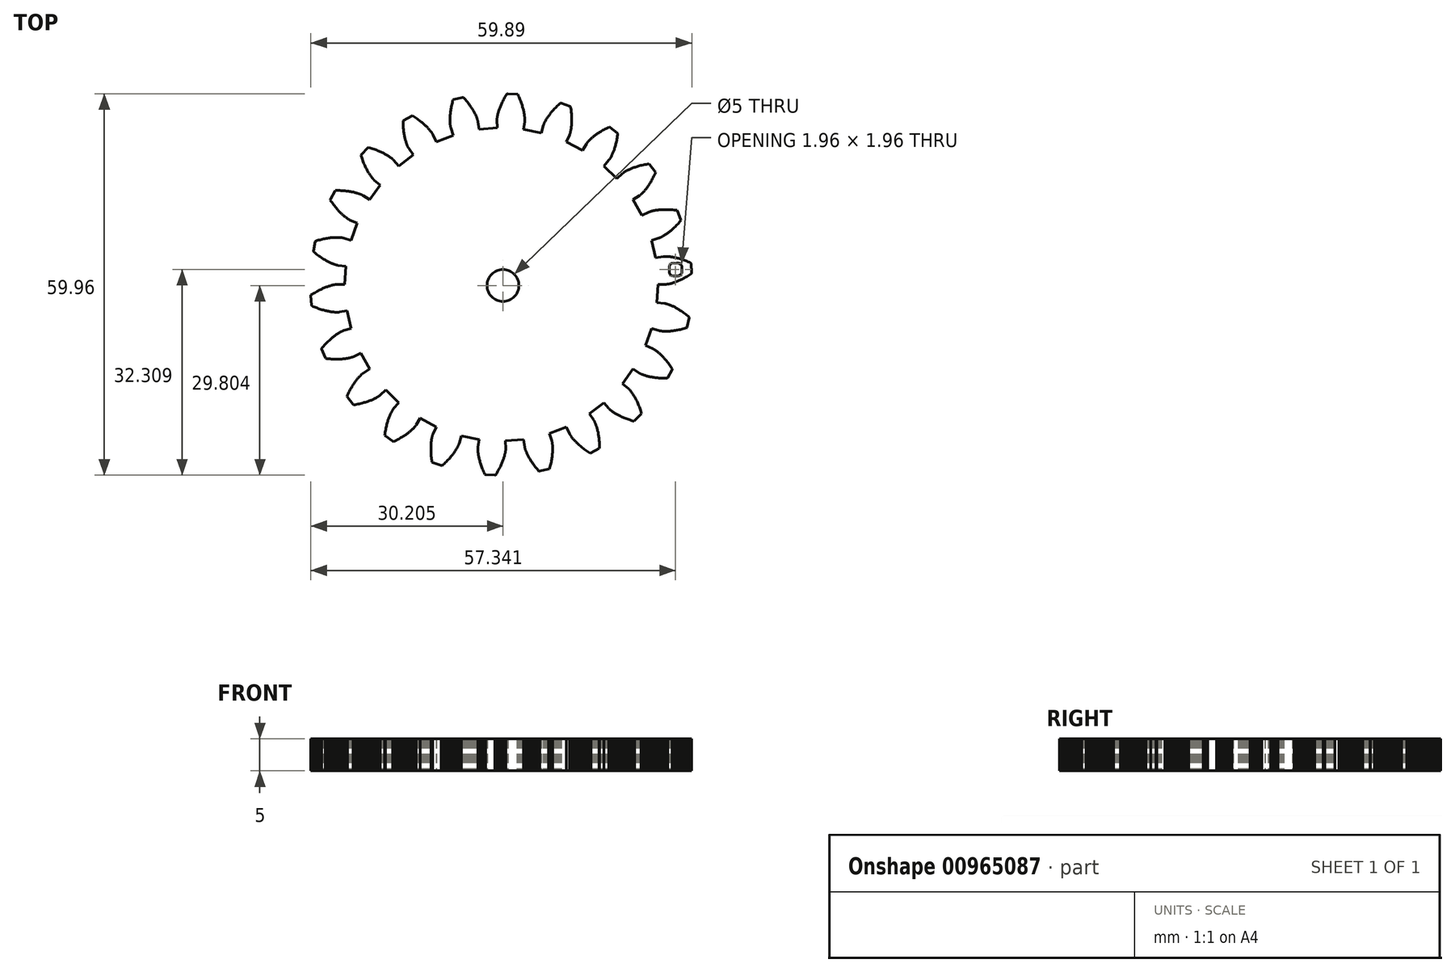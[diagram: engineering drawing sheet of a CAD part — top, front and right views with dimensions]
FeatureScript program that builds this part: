
annotation { "Feature Type Name" : "Feature", "Feature Type Description" : "" }
export const myFeature = defineFeature(function(context is Context, id is Id, definition is map)
    precondition{}
    {
        {
            var Q0;
            Q0=qCreatedBy(makeId("Top.planeOp"),FACE);
            var sketch = newSketch(context, id + "F0", { "sketchPlane" : qUnion([Q0])});
            skLineSegment(sketch, "E0", {"start": v(26.57, 2.43) * mm, "end": v(27.79, 2.43) * mm});
            skLineSegment(sketch, "E1", {"start": v(27.79, 2.43) * mm, "end": v(27.8, 2.43) * mm});
            skLineSegment(sketch, "E2", {"start": v(27.8, 2.43) * mm, "end": v(27.81, 2.43) * mm});
            skLineSegment(sketch, "E3", {"start": v(27.81, 2.43) * mm, "end": v(27.84, 2.43) * mm});
            skLineSegment(sketch, "E4", {"start": v(27.84, 2.43) * mm, "end": v(27.87, 2.43) * mm});
            skLineSegment(sketch, "E5", {"start": v(27.87, 2.43) * mm, "end": v(27.9, 2.44) * mm});
            skLineSegment(sketch, "E6", {"start": v(27.9, 2.44) * mm, "end": v(27.95, 2.44) * mm});
            skLineSegment(sketch, "E7", {"start": v(27.95, 2.44) * mm, "end": v(28, 2.45) * mm});
            skLineSegment(sketch, "E8", {"start": v(28, 2.45) * mm, "end": v(28.05, 2.46) * mm});
            skLineSegment(sketch, "E9", {"start": v(28.05, 2.46) * mm, "end": v(28.11, 2.47) * mm});
            skLineSegment(sketch, "E10", {"start": v(28.11, 2.47) * mm, "end": v(28.18, 2.48) * mm});
            skLineSegment(sketch, "E11", {"start": v(28.18, 2.48) * mm, "end": v(28.25, 2.5) * mm});
            skLineSegment(sketch, "E12", {"start": v(28.25, 2.5) * mm, "end": v(28.33, 2.5) * mm});
            skLineSegment(sketch, "E13", {"start": v(28.33, 2.5) * mm, "end": v(28.42, 2.53) * mm});
            skLineSegment(sketch, "E14", {"start": v(28.42, 2.53) * mm, "end": v(28.51, 2.55) * mm});
            skLineSegment(sketch, "E15", {"start": v(28.51, 2.55) * mm, "end": v(28.61, 2.57) * mm});
            skLineSegment(sketch, "E16", {"start": v(28.61, 2.57) * mm, "end": v(28.72, 2.6) * mm});
            skLineSegment(sketch, "E17", {"start": v(28.72, 2.6) * mm, "end": v(28.83, 2.63) * mm});
            skLineSegment(sketch, "E18", {"start": v(28.83, 2.63) * mm, "end": v(28.94, 2.67) * mm});
            skLineSegment(sketch, "E19", {"start": v(28.94, 2.67) * mm, "end": v(29.06, 2.7) * mm});
            skLineSegment(sketch, "E20", {"start": v(29.06, 2.7) * mm, "end": v(29.19, 2.75) * mm});
            skLineSegment(sketch, "E21", {"start": v(29.19, 2.75) * mm, "end": v(29.32, 2.8) * mm});
            skLineSegment(sketch, "E22", {"start": v(29.32, 2.8) * mm, "end": v(29.46, 2.85) * mm});
            skLineSegment(sketch, "E23", {"start": v(29.46, 2.85) * mm, "end": v(29.6, 2.9) * mm});
            skLineSegment(sketch, "E24", {"start": v(29.6, 2.9) * mm, "end": v(29.75, 2.97) * mm});
            skLineSegment(sketch, "E25", {"start": v(29.75, 2.97) * mm, "end": v(29.9, 3.03) * mm});
            skLineSegment(sketch, "E26", {"start": v(29.9, 3.03) * mm, "end": v(30.06, 3.1) * mm});
            skLineSegment(sketch, "E27", {"start": v(30.06, 3.1) * mm, "end": v(30.22, 3.18) * mm});
            skLineSegment(sketch, "E28", {"start": v(30.22, 3.18) * mm, "end": v(30.4, 3.26) * mm});
            skLineSegment(sketch, "E29", {"start": v(30.4, 3.26) * mm, "end": v(30.56, 3.35) * mm});
            skLineSegment(sketch, "E30", {"start": v(30.56, 3.35) * mm, "end": v(30.74, 3.44) * mm});
            skLineSegment(sketch, "E31", {"start": v(30.74, 3.44) * mm, "end": v(30.92, 3.54) * mm});
            skLineSegment(sketch, "E32", {"start": v(30.92, 3.54) * mm, "end": v(31.1, 3.64) * mm});
            skLineSegment(sketch, "E33", {"start": v(31.1, 3.64) * mm, "end": v(31.3, 3.76) * mm});
            skLineSegment(sketch, "E34", {"start": v(31.3, 3.76) * mm, "end": v(31.48, 3.87) * mm});
            skLineSegment(sketch, "E35", {"start": v(31.48, 3.87) * mm, "end": v(31.68, 4) * mm});
            skLineSegment(sketch, "E36", {"start": v(31.68, 4) * mm, "end": v(31.88, 4.13) * mm});
            skLineSegment(sketch, "E37", {"start": v(31.88, 4.13) * mm, "end": v(31.89, 4.25) * mm});
            skLineSegment(sketch, "E38", {"start": v(31.89, 4.25) * mm, "end": v(31.76, 5.69) * mm});
            skLineSegment(sketch, "E39", {"start": v(31.76, 5.69) * mm, "end": v(31.74, 5.81) * mm});
            skLineSegment(sketch, "E40", {"start": v(31.74, 5.81) * mm, "end": v(31.52, 5.9) * mm});
            skLineSegment(sketch, "E41", {"start": v(31.52, 5.9) * mm, "end": v(31.3, 6) * mm});
            skLineSegment(sketch, "E42", {"start": v(31.3, 6) * mm, "end": v(31.1, 6.08) * mm});
            skLineSegment(sketch, "E43", {"start": v(31.1, 6.08) * mm, "end": v(30.9, 6.16) * mm});
            skLineSegment(sketch, "E44", {"start": v(30.9, 6.16) * mm, "end": v(30.7, 6.23) * mm});
            skLineSegment(sketch, "E45", {"start": v(30.7, 6.23) * mm, "end": v(30.5, 6.3) * mm});
            skLineSegment(sketch, "E46", {"start": v(30.5, 6.3) * mm, "end": v(30.3, 6.36) * mm});
            skLineSegment(sketch, "E47", {"start": v(30.3, 6.36) * mm, "end": v(30.12, 6.41) * mm});
            skLineSegment(sketch, "E48", {"start": v(30.12, 6.41) * mm, "end": v(29.94, 6.47) * mm});
            skLineSegment(sketch, "E49", {"start": v(29.94, 6.47) * mm, "end": v(29.77, 6.51) * mm});
            skLineSegment(sketch, "E50", {"start": v(29.77, 6.51) * mm, "end": v(29.6, 6.56) * mm});
            skLineSegment(sketch, "E51", {"start": v(29.6, 6.56) * mm, "end": v(29.44, 6.6) * mm});
            skLineSegment(sketch, "E52", {"start": v(29.44, 6.6) * mm, "end": v(29.29, 6.63) * mm});
            skLineSegment(sketch, "E53", {"start": v(29.29, 6.63) * mm, "end": v(29.14, 6.66) * mm});
            skLineSegment(sketch, "E54", {"start": v(29.14, 6.66) * mm, "end": v(29, 6.7) * mm});
            skLineSegment(sketch, "E55", {"start": v(29, 6.7) * mm, "end": v(28.85, 6.71) * mm});
            skLineSegment(sketch, "E56", {"start": v(28.85, 6.71) * mm, "end": v(28.72, 6.74) * mm});
            skLineSegment(sketch, "E57", {"start": v(28.72, 6.74) * mm, "end": v(28.6, 6.75) * mm});
            skLineSegment(sketch, "E58", {"start": v(28.6, 6.75) * mm, "end": v(28.47, 6.77) * mm});
            skLineSegment(sketch, "E59", {"start": v(28.47, 6.77) * mm, "end": v(28.36, 6.78) * mm});
            skLineSegment(sketch, "E60", {"start": v(28.36, 6.78) * mm, "end": v(28.25, 6.8) * mm});
            skLineSegment(sketch, "E61", {"start": v(28.25, 6.8) * mm, "end": v(28.15, 6.8) * mm});
            skLineSegment(sketch, "E62", {"start": v(28.15, 6.8) * mm, "end": v(28.06, 6.8) * mm});
            skLineSegment(sketch, "E63", {"start": v(28.06, 6.8) * mm, "end": v(27.97, 6.8) * mm});
            skLineSegment(sketch, "E64", {"start": v(27.97, 6.8) * mm, "end": v(27.89, 6.81) * mm});
            skLineSegment(sketch, "E65", {"start": v(27.89, 6.81) * mm, "end": v(27.81, 6.81) * mm});
            skLineSegment(sketch, "E66", {"start": v(27.81, 6.81) * mm, "end": v(27.74, 6.81) * mm});
            skLineSegment(sketch, "E67", {"start": v(27.74, 6.81) * mm, "end": v(27.68, 6.81) * mm});
            skLineSegment(sketch, "E68", {"start": v(27.68, 6.81) * mm, "end": v(27.62, 6.8) * mm});
            skLineSegment(sketch, "E69", {"start": v(27.62, 6.8) * mm, "end": v(27.57, 6.8) * mm});
            skLineSegment(sketch, "E70", {"start": v(27.57, 6.8) * mm, "end": v(27.53, 6.8) * mm});
            skLineSegment(sketch, "E71", {"start": v(27.53, 6.8) * mm, "end": v(27.5, 6.8) * mm});
            skLineSegment(sketch, "E72", {"start": v(27.5, 6.8) * mm, "end": v(27.47, 6.8) * mm});
            skLineSegment(sketch, "E73", {"start": v(27.47, 6.8) * mm, "end": v(27.44, 6.8) * mm});
            skLineSegment(sketch, "E74", {"start": v(27.44, 6.8) * mm, "end": v(27.43, 6.8) * mm});
            skLineSegment(sketch, "E75", {"start": v(27.43, 6.8) * mm, "end": v(27.42, 6.8) * mm});
            skLineSegment(sketch, "E76", {"start": v(27.42, 6.8) * mm, "end": v(26.21, 6.59) * mm});
            skLineSegment(sketch, "E77", {"start": v(26.21, 6.59) * mm, "end": v(25.57, 9.37) * mm});
            skLineSegment(sketch, "E78", {"start": v(25.57, 9.37) * mm, "end": v(26.74, 9.71) * mm});
            skLineSegment(sketch, "E79", {"start": v(26.74, 9.71) * mm, "end": v(26.75, 9.72) * mm});
            skLineSegment(sketch, "E80", {"start": v(26.75, 9.72) * mm, "end": v(26.76, 9.72) * mm});
            skLineSegment(sketch, "E81", {"start": v(26.76, 9.72) * mm, "end": v(26.79, 9.73) * mm});
            skLineSegment(sketch, "E82", {"start": v(26.79, 9.73) * mm, "end": v(26.81, 9.74) * mm});
            skLineSegment(sketch, "E83", {"start": v(26.81, 9.74) * mm, "end": v(26.85, 9.75) * mm});
            skLineSegment(sketch, "E84", {"start": v(26.85, 9.75) * mm, "end": v(26.89, 9.77) * mm});
            skLineSegment(sketch, "E85", {"start": v(26.89, 9.77) * mm, "end": v(26.93, 9.79) * mm});
            skLineSegment(sketch, "E86", {"start": v(26.93, 9.79) * mm, "end": v(26.99, 9.81) * mm});
            skLineSegment(sketch, "E87", {"start": v(26.99, 9.81) * mm, "end": v(27.04, 9.84) * mm});
            skLineSegment(sketch, "E88", {"start": v(27.04, 9.84) * mm, "end": v(27.1, 9.87) * mm});
            skLineSegment(sketch, "E89", {"start": v(27.1, 9.87) * mm, "end": v(27.17, 9.9) * mm});
            skLineSegment(sketch, "E90", {"start": v(27.17, 9.9) * mm, "end": v(27.24, 9.94) * mm});
            skLineSegment(sketch, "E91", {"start": v(27.24, 9.94) * mm, "end": v(27.32, 9.98) * mm});
            skLineSegment(sketch, "E92", {"start": v(27.32, 9.98) * mm, "end": v(27.4, 10.03) * mm});
            skLineSegment(sketch, "E93", {"start": v(27.4, 10.03) * mm, "end": v(27.5, 10.08) * mm});
            skLineSegment(sketch, "E94", {"start": v(27.5, 10.08) * mm, "end": v(27.58, 10.14) * mm});
            skLineSegment(sketch, "E95", {"start": v(27.58, 10.14) * mm, "end": v(27.68, 10.2) * mm});
            skLineSegment(sketch, "E96", {"start": v(27.68, 10.2) * mm, "end": v(27.78, 10.27) * mm});
            skLineSegment(sketch, "E97", {"start": v(27.78, 10.27) * mm, "end": v(27.89, 10.34) * mm});
            skLineSegment(sketch, "E98", {"start": v(27.89, 10.34) * mm, "end": v(28, 10.41) * mm});
            skLineSegment(sketch, "E99", {"start": v(28, 10.41) * mm, "end": v(28.1, 10.5) * mm});
            skLineSegment(sketch, "E100", {"start": v(28.1, 10.5) * mm, "end": v(28.23, 10.58) * mm});
            skLineSegment(sketch, "E101", {"start": v(28.23, 10.58) * mm, "end": v(28.35, 10.68) * mm});
            skLineSegment(sketch, "E102", {"start": v(28.35, 10.68) * mm, "end": v(28.47, 10.78) * mm});
            skLineSegment(sketch, "E103", {"start": v(28.47, 10.78) * mm, "end": v(28.6, 10.89) * mm});
            skLineSegment(sketch, "E104", {"start": v(28.6, 10.89) * mm, "end": v(28.73, 11) * mm});
            skLineSegment(sketch, "E105", {"start": v(28.73, 11) * mm, "end": v(28.87, 11.12) * mm});
            skLineSegment(sketch, "E106", {"start": v(28.87, 11.12) * mm, "end": v(29, 11.24) * mm});
            skLineSegment(sketch, "E107", {"start": v(29, 11.24) * mm, "end": v(29.15, 11.37) * mm});
            skLineSegment(sketch, "E108", {"start": v(29.15, 11.37) * mm, "end": v(29.29, 11.51) * mm});
            skLineSegment(sketch, "E109", {"start": v(29.29, 11.51) * mm, "end": v(29.43, 11.66) * mm});
            skLineSegment(sketch, "E110", {"start": v(29.43, 11.66) * mm, "end": v(29.58, 11.81) * mm});
            skLineSegment(sketch, "E111", {"start": v(29.58, 11.81) * mm, "end": v(29.73, 11.97) * mm});
            skLineSegment(sketch, "E112", {"start": v(29.73, 11.97) * mm, "end": v(29.88, 12.14) * mm});
            skLineSegment(sketch, "E113", {"start": v(29.88, 12.14) * mm, "end": v(30.03, 12.31) * mm});
            skLineSegment(sketch, "E114", {"start": v(30.03, 12.31) * mm, "end": v(30.19, 12.5) * mm});
            skLineSegment(sketch, "E115", {"start": v(30.19, 12.5) * mm, "end": v(30.16, 12.62) * mm});
            skLineSegment(sketch, "E116", {"start": v(30.16, 12.62) * mm, "end": v(29.64, 13.96) * mm});
            skLineSegment(sketch, "E117", {"start": v(29.64, 13.96) * mm, "end": v(29.58, 14.07) * mm});
            skLineSegment(sketch, "E118", {"start": v(29.58, 14.07) * mm, "end": v(29.34, 14.1) * mm});
            skLineSegment(sketch, "E119", {"start": v(29.34, 14.1) * mm, "end": v(29.1, 14.12) * mm});
            skLineSegment(sketch, "E120", {"start": v(29.1, 14.12) * mm, "end": v(28.89, 14.14) * mm});
            skLineSegment(sketch, "E121", {"start": v(28.89, 14.14) * mm, "end": v(28.67, 14.16) * mm});
            skLineSegment(sketch, "E122", {"start": v(28.67, 14.16) * mm, "end": v(28.46, 14.17) * mm});
            skLineSegment(sketch, "E123", {"start": v(28.46, 14.17) * mm, "end": v(28.25, 14.18) * mm});
            skLineSegment(sketch, "E124", {"start": v(28.25, 14.18) * mm, "end": v(28.05, 14.2) * mm});
            skLineSegment(sketch, "E125", {"start": v(28.05, 14.2) * mm, "end": v(27.86, 14.2) * mm});
            skLineSegment(sketch, "E126", {"start": v(27.86, 14.2) * mm, "end": v(27.67, 14.2) * mm});
            skLineSegment(sketch, "E127", {"start": v(27.67, 14.2) * mm, "end": v(27.5, 14.19) * mm});
            skLineSegment(sketch, "E128", {"start": v(27.5, 14.19) * mm, "end": v(27.32, 14.18) * mm});
            skLineSegment(sketch, "E129", {"start": v(27.32, 14.18) * mm, "end": v(27.15, 14.18) * mm});
            skLineSegment(sketch, "E130", {"start": v(27.15, 14.18) * mm, "end": v(27, 14.17) * mm});
            skLineSegment(sketch, "E131", {"start": v(27, 14.17) * mm, "end": v(26.84, 14.15) * mm});
            skLineSegment(sketch, "E132", {"start": v(26.84, 14.15) * mm, "end": v(26.7, 14.14) * mm});
            skLineSegment(sketch, "E133", {"start": v(26.7, 14.14) * mm, "end": v(26.56, 14.12) * mm});
            skLineSegment(sketch, "E134", {"start": v(26.56, 14.12) * mm, "end": v(26.42, 14.1) * mm});
            skLineSegment(sketch, "E135", {"start": v(26.42, 14.1) * mm, "end": v(26.3, 14.09) * mm});
            skLineSegment(sketch, "E136", {"start": v(26.3, 14.09) * mm, "end": v(26.18, 14.07) * mm});
            skLineSegment(sketch, "E137", {"start": v(26.18, 14.07) * mm, "end": v(26.06, 14.05) * mm});
            skLineSegment(sketch, "E138", {"start": v(26.06, 14.05) * mm, "end": v(25.96, 14.03) * mm});
            skLineSegment(sketch, "E139", {"start": v(25.96, 14.03) * mm, "end": v(25.86, 14) * mm});
            skLineSegment(sketch, "E140", {"start": v(25.86, 14) * mm, "end": v(25.77, 13.99) * mm});
            skLineSegment(sketch, "E141", {"start": v(25.77, 13.99) * mm, "end": v(25.68, 13.96) * mm});
            skLineSegment(sketch, "E142", {"start": v(25.68, 13.96) * mm, "end": v(25.6, 13.94) * mm});
            skLineSegment(sketch, "E143", {"start": v(25.6, 13.94) * mm, "end": v(25.53, 13.92) * mm});
            skLineSegment(sketch, "E144", {"start": v(25.53, 13.92) * mm, "end": v(25.46, 13.9) * mm});
            skLineSegment(sketch, "E145", {"start": v(25.46, 13.9) * mm, "end": v(25.4, 13.89) * mm});
            skLineSegment(sketch, "E146", {"start": v(25.4, 13.89) * mm, "end": v(25.35, 13.87) * mm});
            skLineSegment(sketch, "E147", {"start": v(25.35, 13.87) * mm, "end": v(25.3, 13.85) * mm});
            skLineSegment(sketch, "E148", {"start": v(25.3, 13.85) * mm, "end": v(25.26, 13.84) * mm});
            skLineSegment(sketch, "E149", {"start": v(25.26, 13.84) * mm, "end": v(25.23, 13.82) * mm});
            skLineSegment(sketch, "E150", {"start": v(25.23, 13.82) * mm, "end": v(25.2, 13.81) * mm});
            skLineSegment(sketch, "E151", {"start": v(25.2, 13.81) * mm, "end": v(25.18, 13.8) * mm});
            skLineSegment(sketch, "E152", {"start": v(25.18, 13.8) * mm, "end": v(25.16, 13.8) * mm});
            skLineSegment(sketch, "E153", {"start": v(25.16, 13.8) * mm, "end": v(25.15, 13.8) * mm});
            skLineSegment(sketch, "E154", {"start": v(25.15, 13.8) * mm, "end": v(24.06, 13.26) * mm});
            skLineSegment(sketch, "E155", {"start": v(24.06, 13.26) * mm, "end": v(22.66, 15.74) * mm});
            skLineSegment(sketch, "E156", {"start": v(22.66, 15.74) * mm, "end": v(23.68, 16.4) * mm});
            skLineSegment(sketch, "E157", {"start": v(23.68, 16.4) * mm, "end": v(23.7, 16.4) * mm});
            skLineSegment(sketch, "E158", {"start": v(23.7, 16.4) * mm, "end": v(23.7, 16.42) * mm});
            skLineSegment(sketch, "E159", {"start": v(23.7, 16.42) * mm, "end": v(23.72, 16.43) * mm});
            skLineSegment(sketch, "E160", {"start": v(23.72, 16.43) * mm, "end": v(23.75, 16.45) * mm});
            skLineSegment(sketch, "E161", {"start": v(23.75, 16.45) * mm, "end": v(23.78, 16.47) * mm});
            skLineSegment(sketch, "E162", {"start": v(23.78, 16.47) * mm, "end": v(23.81, 16.5) * mm});
            skLineSegment(sketch, "E163", {"start": v(23.81, 16.5) * mm, "end": v(23.85, 16.53) * mm});
            skLineSegment(sketch, "E164", {"start": v(23.85, 16.53) * mm, "end": v(23.9, 16.57) * mm});
            skLineSegment(sketch, "E165", {"start": v(23.9, 16.57) * mm, "end": v(23.94, 16.6) * mm});
            skLineSegment(sketch, "E166", {"start": v(23.94, 16.6) * mm, "end": v(23.99, 16.66) * mm});
            skLineSegment(sketch, "E167", {"start": v(23.99, 16.66) * mm, "end": v(24.04, 16.7) * mm});
            skLineSegment(sketch, "E168", {"start": v(24.04, 16.7) * mm, "end": v(24.1, 16.76) * mm});
            skLineSegment(sketch, "E169", {"start": v(24.1, 16.76) * mm, "end": v(24.16, 16.83) * mm});
            skLineSegment(sketch, "E170", {"start": v(24.16, 16.83) * mm, "end": v(24.23, 16.9) * mm});
            skLineSegment(sketch, "E171", {"start": v(24.23, 16.9) * mm, "end": v(24.3, 16.97) * mm});
            skLineSegment(sketch, "E172", {"start": v(24.3, 16.97) * mm, "end": v(24.37, 17.05) * mm});
            skLineSegment(sketch, "E173", {"start": v(24.37, 17.05) * mm, "end": v(24.45, 17.14) * mm});
            skLineSegment(sketch, "E174", {"start": v(24.45, 17.14) * mm, "end": v(24.53, 17.23) * mm});
            skLineSegment(sketch, "E175", {"start": v(24.53, 17.23) * mm, "end": v(24.6, 17.33) * mm});
            skLineSegment(sketch, "E176", {"start": v(24.6, 17.33) * mm, "end": v(24.7, 17.43) * mm});
            skLineSegment(sketch, "E177", {"start": v(24.7, 17.43) * mm, "end": v(24.78, 17.54) * mm});
            skLineSegment(sketch, "E178", {"start": v(24.78, 17.54) * mm, "end": v(24.86, 17.66) * mm});
            skLineSegment(sketch, "E179", {"start": v(24.86, 17.66) * mm, "end": v(24.95, 17.78) * mm});
            skLineSegment(sketch, "E180", {"start": v(24.95, 17.78) * mm, "end": v(25.05, 17.92) * mm});
            skLineSegment(sketch, "E181", {"start": v(25.05, 17.92) * mm, "end": v(25.14, 18.05) * mm});
            skLineSegment(sketch, "E182", {"start": v(25.14, 18.05) * mm, "end": v(25.23, 18.2) * mm});
            skLineSegment(sketch, "E183", {"start": v(25.23, 18.2) * mm, "end": v(25.33, 18.35) * mm});
            skLineSegment(sketch, "E184", {"start": v(25.33, 18.35) * mm, "end": v(25.43, 18.51) * mm});
            skLineSegment(sketch, "E185", {"start": v(25.43, 18.51) * mm, "end": v(25.52, 18.68) * mm});
            skLineSegment(sketch, "E186", {"start": v(25.52, 18.68) * mm, "end": v(25.62, 18.85) * mm});
            skLineSegment(sketch, "E187", {"start": v(25.62, 18.85) * mm, "end": v(25.72, 19.03) * mm});
            skLineSegment(sketch, "E188", {"start": v(25.72, 19.03) * mm, "end": v(25.82, 19.22) * mm});
            skLineSegment(sketch, "E189", {"start": v(25.82, 19.22) * mm, "end": v(25.92, 19.41) * mm});
            skLineSegment(sketch, "E190", {"start": v(25.92, 19.41) * mm, "end": v(26.01, 19.62) * mm});
            skLineSegment(sketch, "E191", {"start": v(26.01, 19.62) * mm, "end": v(26.11, 19.83) * mm});
            skLineSegment(sketch, "E192", {"start": v(26.11, 19.83) * mm, "end": v(26.2, 20.04) * mm});
            skLineSegment(sketch, "E193", {"start": v(26.2, 20.04) * mm, "end": v(26.15, 20.15) * mm});
            skLineSegment(sketch, "E194", {"start": v(26.15, 20.15) * mm, "end": v(25.27, 21.3) * mm});
            skLineSegment(sketch, "E195", {"start": v(25.27, 21.3) * mm, "end": v(25.18, 21.38) * mm});
            skLineSegment(sketch, "E196", {"start": v(25.18, 21.38) * mm, "end": v(24.94, 21.34) * mm});
            skLineSegment(sketch, "E197", {"start": v(24.94, 21.34) * mm, "end": v(24.71, 21.3) * mm});
            skLineSegment(sketch, "E198", {"start": v(24.71, 21.3) * mm, "end": v(24.5, 21.26) * mm});
            skLineSegment(sketch, "E199", {"start": v(24.5, 21.26) * mm, "end": v(24.28, 21.22) * mm});
            skLineSegment(sketch, "E200", {"start": v(24.28, 21.22) * mm, "end": v(24.07, 21.17) * mm});
            skLineSegment(sketch, "E201", {"start": v(24.07, 21.17) * mm, "end": v(23.87, 21.12) * mm});
            skLineSegment(sketch, "E202", {"start": v(23.87, 21.12) * mm, "end": v(23.68, 21.07) * mm});
            skLineSegment(sketch, "E203", {"start": v(23.68, 21.07) * mm, "end": v(23.5, 21.02) * mm});
            skLineSegment(sketch, "E204", {"start": v(23.5, 21.02) * mm, "end": v(23.32, 20.97) * mm});
            skLineSegment(sketch, "E205", {"start": v(23.32, 20.97) * mm, "end": v(23.15, 20.91) * mm});
            skLineSegment(sketch, "E206", {"start": v(23.15, 20.91) * mm, "end": v(22.98, 20.86) * mm});
            skLineSegment(sketch, "E207", {"start": v(22.98, 20.86) * mm, "end": v(22.82, 20.8) * mm});
            skLineSegment(sketch, "E208", {"start": v(22.82, 20.8) * mm, "end": v(22.67, 20.75) * mm});
            skLineSegment(sketch, "E209", {"start": v(22.67, 20.75) * mm, "end": v(22.53, 20.7) * mm});
            skLineSegment(sketch, "E210", {"start": v(22.53, 20.7) * mm, "end": v(22.4, 20.64) * mm});
            skLineSegment(sketch, "E211", {"start": v(22.4, 20.64) * mm, "end": v(22.26, 20.58) * mm});
            skLineSegment(sketch, "E212", {"start": v(22.26, 20.58) * mm, "end": v(22.14, 20.53) * mm});
            skLineSegment(sketch, "E213", {"start": v(22.14, 20.53) * mm, "end": v(22.03, 20.48) * mm});
            skLineSegment(sketch, "E214", {"start": v(22.03, 20.48) * mm, "end": v(21.92, 20.43) * mm});
            skLineSegment(sketch, "E215", {"start": v(21.92, 20.43) * mm, "end": v(21.81, 20.37) * mm});
            skLineSegment(sketch, "E216", {"start": v(21.81, 20.37) * mm, "end": v(21.72, 20.32) * mm});
            skLineSegment(sketch, "E217", {"start": v(21.72, 20.32) * mm, "end": v(21.63, 20.28) * mm});
            skLineSegment(sketch, "E218", {"start": v(21.63, 20.28) * mm, "end": v(21.55, 20.23) * mm});
            skLineSegment(sketch, "E219", {"start": v(21.55, 20.23) * mm, "end": v(21.47, 20.19) * mm});
            skLineSegment(sketch, "E220", {"start": v(21.47, 20.19) * mm, "end": v(21.4, 20.14) * mm});
            skLineSegment(sketch, "E221", {"start": v(21.4, 20.14) * mm, "end": v(21.33, 20.1) * mm});
            skLineSegment(sketch, "E222", {"start": v(21.33, 20.1) * mm, "end": v(21.28, 20.07) * mm});
            skLineSegment(sketch, "E223", {"start": v(21.28, 20.07) * mm, "end": v(21.22, 20.03) * mm});
            skLineSegment(sketch, "E224", {"start": v(21.22, 20.03) * mm, "end": v(21.18, 20) * mm});
            skLineSegment(sketch, "E225", {"start": v(21.18, 20) * mm, "end": v(21.14, 19.97) * mm});
            skLineSegment(sketch, "E226", {"start": v(21.14, 19.97) * mm, "end": v(21.1, 19.95) * mm});
            skLineSegment(sketch, "E227", {"start": v(21.1, 19.95) * mm, "end": v(21.08, 19.92) * mm});
            skLineSegment(sketch, "E228", {"start": v(21.08, 19.92) * mm, "end": v(21.05, 19.9) * mm});
            skLineSegment(sketch, "E229", {"start": v(21.05, 19.9) * mm, "end": v(21.03, 19.9) * mm});
            skLineSegment(sketch, "E230", {"start": v(21.03, 19.9) * mm, "end": v(21.02, 19.88) * mm});
            skLineSegment(sketch, "E231", {"start": v(21.02, 19.88) * mm, "end": v(21.01, 19.87) * mm});
            skLineSegment(sketch, "E232", {"start": v(21.01, 19.87) * mm, "end": v(20.11, 19.05) * mm});
            skLineSegment(sketch, "E233", {"start": v(20.11, 19.05) * mm, "end": v(18.07, 21.04) * mm});
            skLineSegment(sketch, "E234", {"start": v(18.07, 21.04) * mm, "end": v(18.87, 21.96) * mm});
            skLineSegment(sketch, "E235", {"start": v(18.87, 21.96) * mm, "end": v(18.87, 21.97) * mm});
            skLineSegment(sketch, "E236", {"start": v(18.87, 21.97) * mm, "end": v(18.88, 21.98) * mm});
            skLineSegment(sketch, "E237", {"start": v(18.88, 21.98) * mm, "end": v(18.9, 22) * mm});
            skLineSegment(sketch, "E238", {"start": v(18.9, 22) * mm, "end": v(18.91, 22.03) * mm});
            skLineSegment(sketch, "E239", {"start": v(18.91, 22.03) * mm, "end": v(18.94, 22.06) * mm});
            skLineSegment(sketch, "E240", {"start": v(18.94, 22.06) * mm, "end": v(18.96, 22.1) * mm});
            skLineSegment(sketch, "E241", {"start": v(18.96, 22.1) * mm, "end": v(18.99, 22.13) * mm});
            skLineSegment(sketch, "E242", {"start": v(18.99, 22.13) * mm, "end": v(19.02, 22.18) * mm});
            skLineSegment(sketch, "E243", {"start": v(19.02, 22.18) * mm, "end": v(19.05, 22.23) * mm});
            skLineSegment(sketch, "E244", {"start": v(19.05, 22.23) * mm, "end": v(19.09, 22.3) * mm});
            skLineSegment(sketch, "E245", {"start": v(19.09, 22.3) * mm, "end": v(19.13, 22.36) * mm});
            skLineSegment(sketch, "E246", {"start": v(19.13, 22.36) * mm, "end": v(19.17, 22.43) * mm});
            skLineSegment(sketch, "E247", {"start": v(19.17, 22.43) * mm, "end": v(19.2, 22.5) * mm});
            skLineSegment(sketch, "E248", {"start": v(19.2, 22.5) * mm, "end": v(19.25, 22.59) * mm});
            skLineSegment(sketch, "E249", {"start": v(19.25, 22.59) * mm, "end": v(19.3, 22.68) * mm});
            skLineSegment(sketch, "E250", {"start": v(19.3, 22.68) * mm, "end": v(19.35, 22.78) * mm});
            skLineSegment(sketch, "E251", {"start": v(19.35, 22.78) * mm, "end": v(19.4, 22.88) * mm});
            skLineSegment(sketch, "E252", {"start": v(19.4, 22.88) * mm, "end": v(19.44, 23) * mm});
            skLineSegment(sketch, "E253", {"start": v(19.44, 23) * mm, "end": v(19.5, 23.1) * mm});
            skLineSegment(sketch, "E254", {"start": v(19.5, 23.1) * mm, "end": v(19.54, 23.23) * mm});
            skLineSegment(sketch, "E255", {"start": v(19.54, 23.23) * mm, "end": v(19.6, 23.36) * mm});
            skLineSegment(sketch, "E256", {"start": v(19.6, 23.36) * mm, "end": v(19.65, 23.5) * mm});
            skLineSegment(sketch, "E257", {"start": v(19.65, 23.5) * mm, "end": v(19.7, 23.65) * mm});
            skLineSegment(sketch, "E258", {"start": v(19.7, 23.65) * mm, "end": v(19.75, 23.8) * mm});
            skLineSegment(sketch, "E259", {"start": v(19.75, 23.8) * mm, "end": v(19.8, 23.96) * mm});
            skLineSegment(sketch, "E260", {"start": v(19.8, 23.96) * mm, "end": v(19.85, 24.12) * mm});
            skLineSegment(sketch, "E261", {"start": v(19.85, 24.12) * mm, "end": v(19.9, 24.3) * mm});
            skLineSegment(sketch, "E262", {"start": v(19.9, 24.3) * mm, "end": v(19.94, 24.48) * mm});
            skLineSegment(sketch, "E263", {"start": v(19.94, 24.48) * mm, "end": v(20, 24.66) * mm});
            skLineSegment(sketch, "E264", {"start": v(20, 24.66) * mm, "end": v(20.04, 24.86) * mm});
            skLineSegment(sketch, "E265", {"start": v(20.04, 24.86) * mm, "end": v(20.08, 25.06) * mm});
            skLineSegment(sketch, "E266", {"start": v(20.08, 25.06) * mm, "end": v(20.12, 25.27) * mm});
            skLineSegment(sketch, "E267", {"start": v(20.12, 25.27) * mm, "end": v(20.16, 25.48) * mm});
            skLineSegment(sketch, "E268", {"start": v(20.16, 25.48) * mm, "end": v(20.2, 25.7) * mm});
            skLineSegment(sketch, "E269", {"start": v(20.2, 25.7) * mm, "end": v(20.23, 25.93) * mm});
            skLineSegment(sketch, "E270", {"start": v(20.23, 25.93) * mm, "end": v(20.26, 26.17) * mm});
            skLineSegment(sketch, "E271", {"start": v(20.26, 26.17) * mm, "end": v(20.17, 26.25) * mm});
            skLineSegment(sketch, "E272", {"start": v(20.17, 26.25) * mm, "end": v(19, 27.1) * mm});
            skLineSegment(sketch, "E273", {"start": v(19, 27.1) * mm, "end": v(18.9, 27.16) * mm});
            skLineSegment(sketch, "E274", {"start": v(18.9, 27.16) * mm, "end": v(18.68, 27.06) * mm});
            skLineSegment(sketch, "E275", {"start": v(18.68, 27.06) * mm, "end": v(18.47, 26.96) * mm});
            skLineSegment(sketch, "E276", {"start": v(18.47, 26.96) * mm, "end": v(18.28, 26.85) * mm});
            skLineSegment(sketch, "E277", {"start": v(18.28, 26.85) * mm, "end": v(18.08, 26.75) * mm});
            skLineSegment(sketch, "E278", {"start": v(18.08, 26.75) * mm, "end": v(17.9, 26.65) * mm});
            skLineSegment(sketch, "E279", {"start": v(17.9, 26.65) * mm, "end": v(17.72, 26.54) * mm});
            skLineSegment(sketch, "E280", {"start": v(17.72, 26.54) * mm, "end": v(17.55, 26.44) * mm});
            skLineSegment(sketch, "E281", {"start": v(17.55, 26.44) * mm, "end": v(17.39, 26.34) * mm});
            skLineSegment(sketch, "E282", {"start": v(17.39, 26.34) * mm, "end": v(17.23, 26.24) * mm});
            skLineSegment(sketch, "E283", {"start": v(17.23, 26.24) * mm, "end": v(17.08, 26.14) * mm});
            skLineSegment(sketch, "E284", {"start": v(17.08, 26.14) * mm, "end": v(16.94, 26.04) * mm});
            skLineSegment(sketch, "E285", {"start": v(16.94, 26.04) * mm, "end": v(16.8, 25.94) * mm});
            skLineSegment(sketch, "E286", {"start": v(16.8, 25.94) * mm, "end": v(16.67, 25.85) * mm});
            skLineSegment(sketch, "E287", {"start": v(16.67, 25.85) * mm, "end": v(16.55, 25.75) * mm});
            skLineSegment(sketch, "E288", {"start": v(16.55, 25.75) * mm, "end": v(16.44, 25.66) * mm});
            skLineSegment(sketch, "E289", {"start": v(16.44, 25.66) * mm, "end": v(16.33, 25.57) * mm});
            skLineSegment(sketch, "E290", {"start": v(16.33, 25.57) * mm, "end": v(16.22, 25.49) * mm});
            skLineSegment(sketch, "E291", {"start": v(16.22, 25.49) * mm, "end": v(16.13, 25.4) * mm});
            skLineSegment(sketch, "E292", {"start": v(16.13, 25.4) * mm, "end": v(16.04, 25.32) * mm});
            skLineSegment(sketch, "E293", {"start": v(16.04, 25.32) * mm, "end": v(15.95, 25.25) * mm});
            skLineSegment(sketch, "E294", {"start": v(15.95, 25.25) * mm, "end": v(15.88, 25.17) * mm});
            skLineSegment(sketch, "E295", {"start": v(15.88, 25.17) * mm, "end": v(15.8, 25.1) * mm});
            skLineSegment(sketch, "E296", {"start": v(15.8, 25.1) * mm, "end": v(15.74, 25.03) * mm});
            skLineSegment(sketch, "E297", {"start": v(15.74, 25.03) * mm, "end": v(15.68, 24.97) * mm});
            skLineSegment(sketch, "E298", {"start": v(15.68, 24.97) * mm, "end": v(15.62, 24.9) * mm});
            skLineSegment(sketch, "E299", {"start": v(15.62, 24.9) * mm, "end": v(15.57, 24.85) * mm});
            skLineSegment(sketch, "E300", {"start": v(15.57, 24.85) * mm, "end": v(15.52, 24.8) * mm});
            skLineSegment(sketch, "E301", {"start": v(15.52, 24.8) * mm, "end": v(15.48, 24.75) * mm});
            skLineSegment(sketch, "E302", {"start": v(15.48, 24.75) * mm, "end": v(15.45, 24.7) * mm});
            skLineSegment(sketch, "E303", {"start": v(15.45, 24.7) * mm, "end": v(15.42, 24.67) * mm});
            skLineSegment(sketch, "E304", {"start": v(15.42, 24.67) * mm, "end": v(15.4, 24.64) * mm});
            skLineSegment(sketch, "E305", {"start": v(15.4, 24.64) * mm, "end": v(15.37, 24.6) * mm});
            skLineSegment(sketch, "E306", {"start": v(15.37, 24.6) * mm, "end": v(15.35, 24.58) * mm});
            skLineSegment(sketch, "E307", {"start": v(15.35, 24.58) * mm, "end": v(15.34, 24.56) * mm});
            skLineSegment(sketch, "E308", {"start": v(15.34, 24.56) * mm, "end": v(15.33, 24.55) * mm});
            skLineSegment(sketch, "E309", {"start": v(15.33, 24.55) * mm, "end": v(15.33, 24.54) * mm});
            skLineSegment(sketch, "E310", {"start": v(15.33, 24.54) * mm, "end": v(14.7, 23.5) * mm});
            skLineSegment(sketch, "E311", {"start": v(14.7, 23.5) * mm, "end": v(12.17, 24.83) * mm});
            skLineSegment(sketch, "E312", {"start": v(12.17, 24.83) * mm, "end": v(12.68, 25.94) * mm});
            skLineSegment(sketch, "E313", {"start": v(12.68, 25.94) * mm, "end": v(12.68, 25.95) * mm});
            skLineSegment(sketch, "E314", {"start": v(12.68, 25.95) * mm, "end": v(12.69, 25.97) * mm});
            skLineSegment(sketch, "E315", {"start": v(12.69, 25.97) * mm, "end": v(12.7, 25.99) * mm});
            skLineSegment(sketch, "E316", {"start": v(12.7, 25.99) * mm, "end": v(12.7, 26.02) * mm});
            skLineSegment(sketch, "E317", {"start": v(12.7, 26.02) * mm, "end": v(12.72, 26.05) * mm});
            skLineSegment(sketch, "E318", {"start": v(12.72, 26.05) * mm, "end": v(12.73, 26.1) * mm});
            skLineSegment(sketch, "E319", {"start": v(12.73, 26.1) * mm, "end": v(12.75, 26.14) * mm});
            skLineSegment(sketch, "E320", {"start": v(12.75, 26.14) * mm, "end": v(12.76, 26.2) * mm});
            skLineSegment(sketch, "E321", {"start": v(12.76, 26.2) * mm, "end": v(12.78, 26.25) * mm});
            skLineSegment(sketch, "E322", {"start": v(12.78, 26.25) * mm, "end": v(12.8, 26.32) * mm});
            skLineSegment(sketch, "E323", {"start": v(12.8, 26.32) * mm, "end": v(12.82, 26.4) * mm});
            skLineSegment(sketch, "E324", {"start": v(12.82, 26.4) * mm, "end": v(12.83, 26.47) * mm});
            skLineSegment(sketch, "E325", {"start": v(12.83, 26.47) * mm, "end": v(12.85, 26.56) * mm});
            skLineSegment(sketch, "E326", {"start": v(12.85, 26.56) * mm, "end": v(12.87, 26.65) * mm});
            skLineSegment(sketch, "E327", {"start": v(12.87, 26.65) * mm, "end": v(12.9, 26.75) * mm});
            skLineSegment(sketch, "E328", {"start": v(12.9, 26.75) * mm, "end": v(12.9, 26.86) * mm});
            skLineSegment(sketch, "E329", {"start": v(12.9, 26.86) * mm, "end": v(12.92, 26.97) * mm});
            skLineSegment(sketch, "E330", {"start": v(12.92, 26.97) * mm, "end": v(12.94, 27.1) * mm});
            skLineSegment(sketch, "E331", {"start": v(12.94, 27.1) * mm, "end": v(12.96, 27.22) * mm});
            skLineSegment(sketch, "E332", {"start": v(12.96, 27.22) * mm, "end": v(12.97, 27.35) * mm});
            skLineSegment(sketch, "E333", {"start": v(12.97, 27.35) * mm, "end": v(12.98, 27.49) * mm});
            skLineSegment(sketch, "E334", {"start": v(12.98, 27.49) * mm, "end": v(13, 27.64) * mm});
            skLineSegment(sketch, "E335", {"start": v(13, 27.64) * mm, "end": v(13, 27.8) * mm});
            skLineSegment(sketch, "E336", {"start": v(13, 27.8) * mm, "end": v(13, 27.95) * mm});
            skLineSegment(sketch, "E337", {"start": v(13, 27.95) * mm, "end": v(13, 28.12) * mm});
            skLineSegment(sketch, "E338", {"start": v(13, 28.12) * mm, "end": v(13.01, 28.29) * mm});
            skLineSegment(sketch, "E339", {"start": v(13.01, 28.29) * mm, "end": v(13, 28.47) * mm});
            skLineSegment(sketch, "E340", {"start": v(13, 28.47) * mm, "end": v(13, 28.66) * mm});
            skLineSegment(sketch, "E341", {"start": v(13, 28.66) * mm, "end": v(13, 28.85) * mm});
            skLineSegment(sketch, "E342", {"start": v(13, 28.85) * mm, "end": v(12.98, 29.05) * mm});
            skLineSegment(sketch, "E343", {"start": v(12.98, 29.05) * mm, "end": v(12.97, 29.25) * mm});
            skLineSegment(sketch, "E344", {"start": v(12.97, 29.25) * mm, "end": v(12.95, 29.46) * mm});
            skLineSegment(sketch, "E345", {"start": v(12.95, 29.46) * mm, "end": v(12.93, 29.68) * mm});
            skLineSegment(sketch, "E346", {"start": v(12.93, 29.68) * mm, "end": v(12.9, 29.9) * mm});
            skLineSegment(sketch, "E347", {"start": v(12.9, 29.9) * mm, "end": v(12.87, 30.13) * mm});
            skLineSegment(sketch, "E348", {"start": v(12.87, 30.13) * mm, "end": v(12.83, 30.37) * mm});
            skLineSegment(sketch, "E349", {"start": v(12.83, 30.37) * mm, "end": v(12.72, 30.43) * mm});
            skLineSegment(sketch, "E350", {"start": v(12.72, 30.43) * mm, "end": v(11.37, 30.91) * mm});
            skLineSegment(sketch, "E351", {"start": v(11.37, 30.91) * mm, "end": v(11.24, 30.94) * mm});
            skLineSegment(sketch, "E352", {"start": v(11.24, 30.94) * mm, "end": v(11.07, 30.78) * mm});
            skLineSegment(sketch, "E353", {"start": v(11.07, 30.78) * mm, "end": v(10.9, 30.62) * mm});
            skLineSegment(sketch, "E354", {"start": v(10.9, 30.62) * mm, "end": v(10.73, 30.47) * mm});
            skLineSegment(sketch, "E355", {"start": v(10.73, 30.47) * mm, "end": v(10.58, 30.31) * mm});
            skLineSegment(sketch, "E356", {"start": v(10.58, 30.31) * mm, "end": v(10.43, 30.16) * mm});
            skLineSegment(sketch, "E357", {"start": v(10.43, 30.16) * mm, "end": v(10.29, 30.01) * mm});
            skLineSegment(sketch, "E358", {"start": v(10.29, 30.01) * mm, "end": v(10.15, 29.87) * mm});
            skLineSegment(sketch, "E359", {"start": v(10.15, 29.87) * mm, "end": v(10.02, 29.72) * mm});
            skLineSegment(sketch, "E360", {"start": v(10.02, 29.72) * mm, "end": v(9.9, 29.58) * mm});
            skLineSegment(sketch, "E361", {"start": v(9.9, 29.58) * mm, "end": v(9.79, 29.44) * mm});
            skLineSegment(sketch, "E362", {"start": v(9.79, 29.44) * mm, "end": v(9.68, 29.3) * mm});
            skLineSegment(sketch, "E363", {"start": v(9.68, 29.3) * mm, "end": v(9.58, 29.18) * mm});
            skLineSegment(sketch, "E364", {"start": v(9.58, 29.18) * mm, "end": v(9.48, 29.05) * mm});
            skLineSegment(sketch, "E365", {"start": v(9.48, 29.05) * mm, "end": v(9.39, 28.93) * mm});
            skLineSegment(sketch, "E366", {"start": v(9.39, 28.93) * mm, "end": v(9.3, 28.8) * mm});
            skLineSegment(sketch, "E367", {"start": v(9.3, 28.8) * mm, "end": v(9.22, 28.7) * mm});
            skLineSegment(sketch, "E368", {"start": v(9.22, 28.7) * mm, "end": v(9.15, 28.58) * mm});
            skLineSegment(sketch, "E369", {"start": v(9.15, 28.58) * mm, "end": v(9.08, 28.47) * mm});
            skLineSegment(sketch, "E370", {"start": v(9.08, 28.47) * mm, "end": v(9.02, 28.37) * mm});
            skLineSegment(sketch, "E371", {"start": v(9.02, 28.37) * mm, "end": v(8.96, 28.27) * mm});
            skLineSegment(sketch, "E372", {"start": v(8.96, 28.27) * mm, "end": v(8.9, 28.18) * mm});
            skLineSegment(sketch, "E373", {"start": v(8.9, 28.18) * mm, "end": v(8.85, 28.09) * mm});
            skLineSegment(sketch, "E374", {"start": v(8.85, 28.09) * mm, "end": v(8.81, 28) * mm});
            skLineSegment(sketch, "E375", {"start": v(8.81, 28) * mm, "end": v(8.77, 27.93) * mm});
            skLineSegment(sketch, "E376", {"start": v(8.77, 27.93) * mm, "end": v(8.73, 27.85) * mm});
            skLineSegment(sketch, "E377", {"start": v(8.73, 27.85) * mm, "end": v(8.7, 27.78) * mm});
            skLineSegment(sketch, "E378", {"start": v(8.7, 27.78) * mm, "end": v(8.67, 27.72) * mm});
            skLineSegment(sketch, "E379", {"start": v(8.67, 27.72) * mm, "end": v(8.65, 27.66) * mm});
            skLineSegment(sketch, "E380", {"start": v(8.65, 27.66) * mm, "end": v(8.63, 27.61) * mm});
            skLineSegment(sketch, "E381", {"start": v(8.63, 27.61) * mm, "end": v(8.6, 27.57) * mm});
            skLineSegment(sketch, "E382", {"start": v(8.6, 27.57) * mm, "end": v(8.6, 27.53) * mm});
            skLineSegment(sketch, "E383", {"start": v(8.6, 27.53) * mm, "end": v(8.58, 27.5) * mm});
            skLineSegment(sketch, "E384", {"start": v(8.58, 27.5) * mm, "end": v(8.57, 27.46) * mm});
            skLineSegment(sketch, "E385", {"start": v(8.57, 27.46) * mm, "end": v(8.56, 27.44) * mm});
            skLineSegment(sketch, "E386", {"start": v(8.56, 27.44) * mm, "end": v(8.56, 27.42) * mm});
            skLineSegment(sketch, "E387", {"start": v(8.56, 27.42) * mm, "end": v(8.55, 27.42) * mm});
            skLineSegment(sketch, "E388", {"start": v(8.55, 27.42) * mm, "end": v(8.24, 26.24) * mm});
            skLineSegment(sketch, "E389", {"start": v(8.24, 26.24) * mm, "end": v(5.44, 26.8) * mm});
            skLineSegment(sketch, "E390", {"start": v(5.44, 26.8) * mm, "end": v(5.62, 28.01) * mm});
            skLineSegment(sketch, "E391", {"start": v(5.62, 28.01) * mm, "end": v(5.62, 28.02) * mm});
            skLineSegment(sketch, "E392", {"start": v(5.62, 28.02) * mm, "end": v(5.62, 28.04) * mm});
            skLineSegment(sketch, "E393", {"start": v(5.62, 28.04) * mm, "end": v(5.62, 28.06) * mm});
            skLineSegment(sketch, "E394", {"start": v(5.62, 28.06) * mm, "end": v(5.63, 28.1) * mm});
            skLineSegment(sketch, "E395", {"start": v(5.63, 28.1) * mm, "end": v(5.63, 28.13) * mm});
            skLineSegment(sketch, "E396", {"start": v(5.63, 28.13) * mm, "end": v(5.63, 28.17) * mm});
            skLineSegment(sketch, "E397", {"start": v(5.63, 28.17) * mm, "end": v(5.63, 28.22) * mm});
            skLineSegment(sketch, "E398", {"start": v(5.63, 28.22) * mm, "end": v(5.63, 28.28) * mm});
            skLineSegment(sketch, "E399", {"start": v(5.63, 28.28) * mm, "end": v(5.63, 28.34) * mm});
            skLineSegment(sketch, "E400", {"start": v(5.63, 28.34) * mm, "end": v(5.63, 28.4) * mm});
            skLineSegment(sketch, "E401", {"start": v(5.63, 28.4) * mm, "end": v(5.62, 28.48) * mm});
            skLineSegment(sketch, "E402", {"start": v(5.62, 28.48) * mm, "end": v(5.62, 28.57) * mm});
            skLineSegment(sketch, "E403", {"start": v(5.62, 28.57) * mm, "end": v(5.61, 28.65) * mm});
            skLineSegment(sketch, "E404", {"start": v(5.61, 28.65) * mm, "end": v(5.6, 28.75) * mm});
            skLineSegment(sketch, "E405", {"start": v(5.6, 28.75) * mm, "end": v(5.6, 28.85) * mm});
            skLineSegment(sketch, "E406", {"start": v(5.6, 28.85) * mm, "end": v(5.58, 28.96) * mm});
            skLineSegment(sketch, "E407", {"start": v(5.58, 28.96) * mm, "end": v(5.57, 29.07) * mm});
            skLineSegment(sketch, "E408", {"start": v(5.57, 29.07) * mm, "end": v(5.55, 29.2) * mm});
            skLineSegment(sketch, "E409", {"start": v(5.55, 29.2) * mm, "end": v(5.53, 29.32) * mm});
            skLineSegment(sketch, "E410", {"start": v(5.53, 29.32) * mm, "end": v(5.5, 29.45) * mm});
            skLineSegment(sketch, "E411", {"start": v(5.5, 29.45) * mm, "end": v(5.47, 29.59) * mm});
            skLineSegment(sketch, "E412", {"start": v(5.47, 29.59) * mm, "end": v(5.44, 29.73) * mm});
            skLineSegment(sketch, "E413", {"start": v(5.44, 29.73) * mm, "end": v(5.4, 29.88) * mm});
            skLineSegment(sketch, "E414", {"start": v(5.4, 29.88) * mm, "end": v(5.37, 30.03) * mm});
            skLineSegment(sketch, "E415", {"start": v(5.37, 30.03) * mm, "end": v(5.32, 30.2) * mm});
            skLineSegment(sketch, "E416", {"start": v(5.32, 30.2) * mm, "end": v(5.28, 30.36) * mm});
            skLineSegment(sketch, "E417", {"start": v(5.28, 30.36) * mm, "end": v(5.22, 30.53) * mm});
            skLineSegment(sketch, "E418", {"start": v(5.22, 30.53) * mm, "end": v(5.17, 30.7) * mm});
            skLineSegment(sketch, "E419", {"start": v(5.17, 30.7) * mm, "end": v(5.1, 30.9) * mm});
            skLineSegment(sketch, "E420", {"start": v(5.1, 30.9) * mm, "end": v(5.04, 31.08) * mm});
            skLineSegment(sketch, "E421", {"start": v(5.04, 31.08) * mm, "end": v(4.97, 31.27) * mm});
            skLineSegment(sketch, "E422", {"start": v(4.97, 31.27) * mm, "end": v(4.89, 31.47) * mm});
            skLineSegment(sketch, "E423", {"start": v(4.89, 31.47) * mm, "end": v(4.8, 31.67) * mm});
            skLineSegment(sketch, "E424", {"start": v(4.8, 31.67) * mm, "end": v(4.72, 31.88) * mm});
            skLineSegment(sketch, "E425", {"start": v(4.72, 31.88) * mm, "end": v(4.62, 32.09) * mm});
            skLineSegment(sketch, "E426", {"start": v(4.62, 32.09) * mm, "end": v(4.52, 32.3) * mm});
            skLineSegment(sketch, "E427", {"start": v(4.52, 32.3) * mm, "end": v(4.4, 32.33) * mm});
            skLineSegment(sketch, "E428", {"start": v(4.4, 32.33) * mm, "end": v(2.96, 32.41) * mm});
            skLineSegment(sketch, "E429", {"start": v(2.96, 32.41) * mm, "end": v(2.83, 32.4) * mm});
            skLineSegment(sketch, "E430", {"start": v(2.83, 32.4) * mm, "end": v(2.7, 32.2) * mm});
            skLineSegment(sketch, "E431", {"start": v(2.7, 32.2) * mm, "end": v(2.6, 32) * mm});
            skLineSegment(sketch, "E432", {"start": v(2.6, 32) * mm, "end": v(2.48, 31.8) * mm});
            skLineSegment(sketch, "E433", {"start": v(2.48, 31.8) * mm, "end": v(2.37, 31.62) * mm});
            skLineSegment(sketch, "E434", {"start": v(2.37, 31.62) * mm, "end": v(2.27, 31.43) * mm});
            skLineSegment(sketch, "E435", {"start": v(2.27, 31.43) * mm, "end": v(2.18, 31.25) * mm});
            skLineSegment(sketch, "E436", {"start": v(2.18, 31.25) * mm, "end": v(2.1, 31.07) * mm});
            skLineSegment(sketch, "E437", {"start": v(2.1, 31.07) * mm, "end": v(2, 30.9) * mm});
            skLineSegment(sketch, "E438", {"start": v(2, 30.9) * mm, "end": v(1.93, 30.72) * mm});
            skLineSegment(sketch, "E439", {"start": v(1.93, 30.72) * mm, "end": v(1.86, 30.56) * mm});
            skLineSegment(sketch, "E440", {"start": v(1.86, 30.56) * mm, "end": v(1.8, 30.4) * mm});
            skLineSegment(sketch, "E441", {"start": v(1.8, 30.4) * mm, "end": v(1.73, 30.25) * mm});
            skLineSegment(sketch, "E442", {"start": v(1.73, 30.25) * mm, "end": v(1.67, 30.1) * mm});
            skLineSegment(sketch, "E443", {"start": v(1.67, 30.1) * mm, "end": v(1.62, 29.95) * mm});
            skLineSegment(sketch, "E444", {"start": v(1.62, 29.95) * mm, "end": v(1.57, 29.81) * mm});
            skLineSegment(sketch, "E445", {"start": v(1.57, 29.81) * mm, "end": v(1.53, 29.68) * mm});
            skLineSegment(sketch, "E446", {"start": v(1.53, 29.68) * mm, "end": v(1.49, 29.55) * mm});
            skLineSegment(sketch, "E447", {"start": v(1.49, 29.55) * mm, "end": v(1.45, 29.43) * mm});
            skLineSegment(sketch, "E448", {"start": v(1.45, 29.43) * mm, "end": v(1.42, 29.31) * mm});
            skLineSegment(sketch, "E449", {"start": v(1.42, 29.31) * mm, "end": v(1.4, 29.2) * mm});
            skLineSegment(sketch, "E450", {"start": v(1.4, 29.2) * mm, "end": v(1.37, 29.1) * mm});
            skLineSegment(sketch, "E451", {"start": v(1.37, 29.1) * mm, "end": v(1.35, 29) * mm});
            skLineSegment(sketch, "E452", {"start": v(1.35, 29) * mm, "end": v(1.33, 28.9) * mm});
            skLineSegment(sketch, "E453", {"start": v(1.33, 28.9) * mm, "end": v(1.31, 28.82) * mm});
            skLineSegment(sketch, "E454", {"start": v(1.31, 28.82) * mm, "end": v(1.3, 28.74) * mm});
            skLineSegment(sketch, "E455", {"start": v(1.3, 28.74) * mm, "end": v(1.28, 28.66) * mm});
            skLineSegment(sketch, "E456", {"start": v(1.28, 28.66) * mm, "end": v(1.27, 28.6) * mm});
            skLineSegment(sketch, "E457", {"start": v(1.27, 28.6) * mm, "end": v(1.27, 28.53) * mm});
            skLineSegment(sketch, "E458", {"start": v(1.27, 28.53) * mm, "end": v(1.26, 28.48) * mm});
            skLineSegment(sketch, "E459", {"start": v(1.26, 28.48) * mm, "end": v(1.26, 28.43) * mm});
            skLineSegment(sketch, "E460", {"start": v(1.26, 28.43) * mm, "end": v(1.25, 28.38) * mm});
            skLineSegment(sketch, "E461", {"start": v(1.25, 28.38) * mm, "end": v(1.25, 28.35) * mm});
            skLineSegment(sketch, "E462", {"start": v(1.25, 28.35) * mm, "end": v(1.25, 28.32) * mm});
            skLineSegment(sketch, "E463", {"start": v(1.25, 28.32) * mm, "end": v(1.25, 28.3) * mm});
            skLineSegment(sketch, "E464", {"start": v(1.25, 28.3) * mm, "end": v(1.25, 28.28) * mm});
            skLineSegment(sketch, "E465", {"start": v(1.25, 28.28) * mm, "end": v(1.25, 28.27) * mm});
            skLineSegment(sketch, "E466", {"start": v(1.25, 28.27) * mm, "end": v(1.28, 27.05) * mm});
            skLineSegment(sketch, "E467", {"start": v(1.28, 27.05) * mm, "end": v(-1.56, 26.8) * mm});
            skLineSegment(sketch, "E468", {"start": v(-1.56, 26.8) * mm, "end": v(-1.74, 28.01) * mm});
            skLineSegment(sketch, "E469", {"start": v(-1.74, 28.01) * mm, "end": v(-1.74, 28.02) * mm});
            skLineSegment(sketch, "E470", {"start": v(-1.74, 28.02) * mm, "end": v(-1.74, 28.04) * mm});
            skLineSegment(sketch, "E471", {"start": v(-1.74, 28.04) * mm, "end": v(-1.75, 28.06) * mm});
            skLineSegment(sketch, "E472", {"start": v(-1.75, 28.06) * mm, "end": v(-1.75, 28.1) * mm});
            skLineSegment(sketch, "E473", {"start": v(-1.75, 28.1) * mm, "end": v(-1.76, 28.13) * mm});
            skLineSegment(sketch, "E474", {"start": v(-1.76, 28.13) * mm, "end": v(-1.77, 28.17) * mm});
            skLineSegment(sketch, "E475", {"start": v(-1.77, 28.17) * mm, "end": v(-1.79, 28.22) * mm});
            skLineSegment(sketch, "E476", {"start": v(-1.79, 28.22) * mm, "end": v(-1.8, 28.27) * mm});
            skLineSegment(sketch, "E477", {"start": v(-1.8, 28.27) * mm, "end": v(-1.82, 28.33) * mm});
            skLineSegment(sketch, "E478", {"start": v(-1.82, 28.33) * mm, "end": v(-1.84, 28.4) * mm});
            skLineSegment(sketch, "E479", {"start": v(-1.84, 28.4) * mm, "end": v(-1.86, 28.47) * mm});
            skLineSegment(sketch, "E480", {"start": v(-1.86, 28.47) * mm, "end": v(-1.9, 28.54) * mm});
            skLineSegment(sketch, "E481", {"start": v(-1.9, 28.54) * mm, "end": v(-1.92, 28.63) * mm});
            skLineSegment(sketch, "E482", {"start": v(-1.92, 28.63) * mm, "end": v(-1.96, 28.72) * mm});
            skLineSegment(sketch, "E483", {"start": v(-1.96, 28.72) * mm, "end": v(-2, 28.8) * mm});
            skLineSegment(sketch, "E484", {"start": v(-2, 28.8) * mm, "end": v(-2.04, 28.9) * mm});
            skLineSegment(sketch, "E485", {"start": v(-2.04, 28.9) * mm, "end": v(-2.09, 29.01) * mm});
            skLineSegment(sketch, "E486", {"start": v(-2.09, 29.01) * mm, "end": v(-2.14, 29.12) * mm});
            skLineSegment(sketch, "E487", {"start": v(-2.14, 29.12) * mm, "end": v(-2.2, 29.24) * mm});
            skLineSegment(sketch, "E488", {"start": v(-2.2, 29.24) * mm, "end": v(-2.25, 29.36) * mm});
            skLineSegment(sketch, "E489", {"start": v(-2.25, 29.36) * mm, "end": v(-2.32, 29.48) * mm});
            skLineSegment(sketch, "E490", {"start": v(-2.32, 29.48) * mm, "end": v(-2.4, 29.61) * mm});
            skLineSegment(sketch, "E491", {"start": v(-2.4, 29.61) * mm, "end": v(-2.47, 29.74) * mm});
            skLineSegment(sketch, "E492", {"start": v(-2.47, 29.74) * mm, "end": v(-2.55, 29.88) * mm});
            skLineSegment(sketch, "E493", {"start": v(-2.55, 29.88) * mm, "end": v(-2.63, 30.02) * mm});
            skLineSegment(sketch, "E494", {"start": v(-2.63, 30.02) * mm, "end": v(-2.73, 30.17) * mm});
            skLineSegment(sketch, "E495", {"start": v(-2.73, 30.17) * mm, "end": v(-2.83, 30.32) * mm});
            skLineSegment(sketch, "E496", {"start": v(-2.83, 30.32) * mm, "end": v(-2.93, 30.47) * mm});
            skLineSegment(sketch, "E497", {"start": v(-2.93, 30.47) * mm, "end": v(-3.04, 30.63) * mm});
            skLineSegment(sketch, "E498", {"start": v(-3.04, 30.63) * mm, "end": v(-3.16, 30.8) * mm});
            skLineSegment(sketch, "E499", {"start": v(-3.16, 30.8) * mm, "end": v(-3.28, 30.96) * mm});
            skLineSegment(sketch, "E500", {"start": v(-3.28, 30.96) * mm, "end": v(-3.41, 31.12) * mm});
            skLineSegment(sketch, "E501", {"start": v(-3.41, 31.12) * mm, "end": v(-3.55, 31.3) * mm});
            skLineSegment(sketch, "E502", {"start": v(-3.55, 31.3) * mm, "end": v(-3.7, 31.47) * mm});
            skLineSegment(sketch, "E503", {"start": v(-3.7, 31.47) * mm, "end": v(-3.84, 31.64) * mm});
            skLineSegment(sketch, "E504", {"start": v(-3.84, 31.64) * mm, "end": v(-4, 31.82) * mm});
            skLineSegment(sketch, "E505", {"start": v(-4, 31.82) * mm, "end": v(-4.13, 31.81) * mm});
            skLineSegment(sketch, "E506", {"start": v(-4.13, 31.81) * mm, "end": v(-5.53, 31.49) * mm});
            skLineSegment(sketch, "E507", {"start": v(-5.53, 31.49) * mm, "end": v(-5.65, 31.44) * mm});
            skLineSegment(sketch, "E508", {"start": v(-5.65, 31.44) * mm, "end": v(-5.7, 31.21) * mm});
            skLineSegment(sketch, "E509", {"start": v(-5.7, 31.21) * mm, "end": v(-5.77, 30.99) * mm});
            skLineSegment(sketch, "E510", {"start": v(-5.77, 30.99) * mm, "end": v(-5.82, 30.77) * mm});
            skLineSegment(sketch, "E511", {"start": v(-5.82, 30.77) * mm, "end": v(-5.87, 30.56) * mm});
            skLineSegment(sketch, "E512", {"start": v(-5.87, 30.56) * mm, "end": v(-5.91, 30.35) * mm});
            skLineSegment(sketch, "E513", {"start": v(-5.91, 30.35) * mm, "end": v(-5.95, 30.15) * mm});
            skLineSegment(sketch, "E514", {"start": v(-5.95, 30.15) * mm, "end": v(-5.98, 29.95) * mm});
            skLineSegment(sketch, "E515", {"start": v(-5.98, 29.95) * mm, "end": v(-6.01, 29.76) * mm});
            skLineSegment(sketch, "E516", {"start": v(-6.01, 29.76) * mm, "end": v(-6.04, 29.58) * mm});
            skLineSegment(sketch, "E517", {"start": v(-6.04, 29.58) * mm, "end": v(-6.06, 29.4) * mm});
            skLineSegment(sketch, "E518", {"start": v(-6.06, 29.4) * mm, "end": v(-6.08, 29.22) * mm});
            skLineSegment(sketch, "E519", {"start": v(-6.08, 29.22) * mm, "end": v(-6.1, 29.06) * mm});
            skLineSegment(sketch, "E520", {"start": v(-6.1, 29.06) * mm, "end": v(-6.1, 28.9) * mm});
            skLineSegment(sketch, "E521", {"start": v(-6.1, 28.9) * mm, "end": v(-6.12, 28.75) * mm});
            skLineSegment(sketch, "E522", {"start": v(-6.12, 28.75) * mm, "end": v(-6.13, 28.6) * mm});
            skLineSegment(sketch, "E523", {"start": v(-6.13, 28.6) * mm, "end": v(-6.13, 28.46) * mm});
            skLineSegment(sketch, "E524", {"start": v(-6.13, 28.46) * mm, "end": v(-6.13, 28.33) * mm});
            skLineSegment(sketch, "E525", {"start": v(-6.13, 28.33) * mm, "end": v(-6.13, 28.2) * mm});
            skLineSegment(sketch, "E526", {"start": v(-6.13, 28.2) * mm, "end": v(-6.13, 28.08) * mm});
            skLineSegment(sketch, "E527", {"start": v(-6.13, 28.08) * mm, "end": v(-6.13, 27.96) * mm});
            skLineSegment(sketch, "E528", {"start": v(-6.13, 27.96) * mm, "end": v(-6.12, 27.85) * mm});
            skLineSegment(sketch, "E529", {"start": v(-6.12, 27.85) * mm, "end": v(-6.11, 27.75) * mm});
            skLineSegment(sketch, "E530", {"start": v(-6.11, 27.75) * mm, "end": v(-6.1, 27.66) * mm});
            skLineSegment(sketch, "E531", {"start": v(-6.1, 27.66) * mm, "end": v(-6.1, 27.57) * mm});
            skLineSegment(sketch, "E532", {"start": v(-6.1, 27.57) * mm, "end": v(-6.09, 27.49) * mm});
            skLineSegment(sketch, "E533", {"start": v(-6.09, 27.49) * mm, "end": v(-6.08, 27.41) * mm});
            skLineSegment(sketch, "E534", {"start": v(-6.08, 27.41) * mm, "end": v(-6.07, 27.35) * mm});
            skLineSegment(sketch, "E535", {"start": v(-6.07, 27.35) * mm, "end": v(-6.06, 27.28) * mm});
            skLineSegment(sketch, "E536", {"start": v(-6.06, 27.28) * mm, "end": v(-6.05, 27.23) * mm});
            skLineSegment(sketch, "E537", {"start": v(-6.05, 27.23) * mm, "end": v(-6.04, 27.18) * mm});
            skLineSegment(sketch, "E538", {"start": v(-6.04, 27.18) * mm, "end": v(-6.03, 27.14) * mm});
            skLineSegment(sketch, "E539", {"start": v(-6.03, 27.14) * mm, "end": v(-6.02, 27.1) * mm});
            skLineSegment(sketch, "E540", {"start": v(-6.02, 27.1) * mm, "end": v(-6.02, 27.07) * mm});
            skLineSegment(sketch, "E541", {"start": v(-6.02, 27.07) * mm, "end": v(-6.01, 27.05) * mm});
            skLineSegment(sketch, "E542", {"start": v(-6.01, 27.05) * mm, "end": v(-6, 27.03) * mm});
            skLineSegment(sketch, "E543", {"start": v(-6, 27.03) * mm, "end": v(-6, 27.02) * mm});
            skLineSegment(sketch, "E544", {"start": v(-6, 27.02) * mm, "end": v(-5.63, 25.86) * mm});
            skLineSegment(sketch, "E545", {"start": v(-5.63, 25.86) * mm, "end": v(-8.29, 24.83) * mm});
            skLineSegment(sketch, "E546", {"start": v(-8.29, 24.83) * mm, "end": v(-8.8, 25.94) * mm});
            skLineSegment(sketch, "E547", {"start": v(-8.8, 25.94) * mm, "end": v(-8.8, 25.95) * mm});
            skLineSegment(sketch, "E548", {"start": v(-8.8, 25.95) * mm, "end": v(-8.8, 25.96) * mm});
            skLineSegment(sketch, "E549", {"start": v(-8.8, 25.96) * mm, "end": v(-8.82, 25.99) * mm});
            skLineSegment(sketch, "E550", {"start": v(-8.82, 25.99) * mm, "end": v(-8.83, 26.01) * mm});
            skLineSegment(sketch, "E551", {"start": v(-8.83, 26.01) * mm, "end": v(-8.85, 26.04) * mm});
            skLineSegment(sketch, "E552", {"start": v(-8.85, 26.04) * mm, "end": v(-8.87, 26.08) * mm});
            skLineSegment(sketch, "E553", {"start": v(-8.87, 26.08) * mm, "end": v(-8.9, 26.12) * mm});
            skLineSegment(sketch, "E554", {"start": v(-8.9, 26.12) * mm, "end": v(-8.93, 26.17) * mm});
            skLineSegment(sketch, "E555", {"start": v(-8.93, 26.17) * mm, "end": v(-8.96, 26.22) * mm});
            skLineSegment(sketch, "E556", {"start": v(-8.96, 26.22) * mm, "end": v(-9, 26.28) * mm});
            skLineSegment(sketch, "E557", {"start": v(-9, 26.28) * mm, "end": v(-9.05, 26.34) * mm});
            skLineSegment(sketch, "E558", {"start": v(-9.05, 26.34) * mm, "end": v(-9.1, 26.4) * mm});
            skLineSegment(sketch, "E559", {"start": v(-9.1, 26.4) * mm, "end": v(-9.15, 26.48) * mm});
            skLineSegment(sketch, "E560", {"start": v(-9.15, 26.48) * mm, "end": v(-9.2, 26.55) * mm});
            skLineSegment(sketch, "E561", {"start": v(-9.2, 26.55) * mm, "end": v(-9.27, 26.63) * mm});
            skLineSegment(sketch, "E562", {"start": v(-9.27, 26.63) * mm, "end": v(-9.34, 26.72) * mm});
            skLineSegment(sketch, "E563", {"start": v(-9.34, 26.72) * mm, "end": v(-9.41, 26.8) * mm});
            skLineSegment(sketch, "E564", {"start": v(-9.41, 26.8) * mm, "end": v(-9.5, 26.9) * mm});
            skLineSegment(sketch, "E565", {"start": v(-9.5, 26.9) * mm, "end": v(-9.58, 26.99) * mm});
            skLineSegment(sketch, "E566", {"start": v(-9.58, 26.99) * mm, "end": v(-9.67, 27.08) * mm});
            skLineSegment(sketch, "E567", {"start": v(-9.67, 27.08) * mm, "end": v(-9.77, 27.19) * mm});
            skLineSegment(sketch, "E568", {"start": v(-9.77, 27.19) * mm, "end": v(-9.87, 27.29) * mm});
            skLineSegment(sketch, "E569", {"start": v(-9.87, 27.29) * mm, "end": v(-9.98, 27.4) * mm});
            skLineSegment(sketch, "E570", {"start": v(-9.98, 27.4) * mm, "end": v(-10.1, 27.5) * mm});
            skLineSegment(sketch, "E571", {"start": v(-10.1, 27.5) * mm, "end": v(-10.22, 27.62) * mm});
            skLineSegment(sketch, "E572", {"start": v(-10.22, 27.62) * mm, "end": v(-10.35, 27.73) * mm});
            skLineSegment(sketch, "E573", {"start": v(-10.35, 27.73) * mm, "end": v(-10.49, 27.85) * mm});
            skLineSegment(sketch, "E574", {"start": v(-10.49, 27.85) * mm, "end": v(-10.63, 27.97) * mm});
            skLineSegment(sketch, "E575", {"start": v(-10.63, 27.97) * mm, "end": v(-10.78, 28.09) * mm});
            skLineSegment(sketch, "E576", {"start": v(-10.78, 28.09) * mm, "end": v(-10.94, 28.2) * mm});
            skLineSegment(sketch, "E577", {"start": v(-10.94, 28.2) * mm, "end": v(-11.1, 28.33) * mm});
            skLineSegment(sketch, "E578", {"start": v(-11.1, 28.33) * mm, "end": v(-11.28, 28.45) * mm});
            skLineSegment(sketch, "E579", {"start": v(-11.28, 28.45) * mm, "end": v(-11.46, 28.58) * mm});
            skLineSegment(sketch, "E580", {"start": v(-11.46, 28.58) * mm, "end": v(-11.64, 28.7) * mm});
            skLineSegment(sketch, "E581", {"start": v(-11.64, 28.7) * mm, "end": v(-11.84, 28.83) * mm});
            skLineSegment(sketch, "E582", {"start": v(-11.84, 28.83) * mm, "end": v(-12.04, 28.96) * mm});
            skLineSegment(sketch, "E583", {"start": v(-12.04, 28.96) * mm, "end": v(-12.16, 28.91) * mm});
            skLineSegment(sketch, "E584", {"start": v(-12.16, 28.91) * mm, "end": v(-13.41, 28.2) * mm});
            skLineSegment(sketch, "E585", {"start": v(-13.41, 28.2) * mm, "end": v(-13.51, 28.13) * mm});
            skLineSegment(sketch, "E586", {"start": v(-13.51, 28.13) * mm, "end": v(-13.5, 27.9) * mm});
            skLineSegment(sketch, "E587", {"start": v(-13.5, 27.9) * mm, "end": v(-13.5, 27.66) * mm});
            skLineSegment(sketch, "E588", {"start": v(-13.5, 27.66) * mm, "end": v(-13.49, 27.43) * mm});
            skLineSegment(sketch, "E589", {"start": v(-13.49, 27.43) * mm, "end": v(-13.48, 27.22) * mm});
            skLineSegment(sketch, "E590", {"start": v(-13.48, 27.22) * mm, "end": v(-13.46, 27) * mm});
            skLineSegment(sketch, "E591", {"start": v(-13.46, 27) * mm, "end": v(-13.44, 26.8) * mm});
            skLineSegment(sketch, "E592", {"start": v(-13.44, 26.8) * mm, "end": v(-13.42, 26.6) * mm});
            skLineSegment(sketch, "E593", {"start": v(-13.42, 26.6) * mm, "end": v(-13.4, 26.41) * mm});
            skLineSegment(sketch, "E594", {"start": v(-13.4, 26.41) * mm, "end": v(-13.36, 26.23) * mm});
            skLineSegment(sketch, "E595", {"start": v(-13.36, 26.23) * mm, "end": v(-13.34, 26.05) * mm});
            skLineSegment(sketch, "E596", {"start": v(-13.34, 26.05) * mm, "end": v(-13.3, 25.88) * mm});
            skLineSegment(sketch, "E597", {"start": v(-13.3, 25.88) * mm, "end": v(-13.27, 25.72) * mm});
            skLineSegment(sketch, "E598", {"start": v(-13.27, 25.72) * mm, "end": v(-13.24, 25.56) * mm});
            skLineSegment(sketch, "E599", {"start": v(-13.24, 25.56) * mm, "end": v(-13.2, 25.4) * mm});
            skLineSegment(sketch, "E600", {"start": v(-13.2, 25.4) * mm, "end": v(-13.17, 25.27) * mm});
            skLineSegment(sketch, "E601", {"start": v(-13.17, 25.27) * mm, "end": v(-13.14, 25.13) * mm});
            skLineSegment(sketch, "E602", {"start": v(-13.14, 25.13) * mm, "end": v(-13.1, 25) * mm});
            skLineSegment(sketch, "E603", {"start": v(-13.1, 25) * mm, "end": v(-13.06, 24.88) * mm});
            skLineSegment(sketch, "E604", {"start": v(-13.06, 24.88) * mm, "end": v(-13.03, 24.76) * mm});
            skLineSegment(sketch, "E605", {"start": v(-13.03, 24.76) * mm, "end": v(-13, 24.66) * mm});
            skLineSegment(sketch, "E606", {"start": v(-13, 24.66) * mm, "end": v(-12.96, 24.55) * mm});
            skLineSegment(sketch, "E607", {"start": v(-12.96, 24.55) * mm, "end": v(-12.92, 24.46) * mm});
            skLineSegment(sketch, "E608", {"start": v(-12.92, 24.46) * mm, "end": v(-12.89, 24.37) * mm});
            skLineSegment(sketch, "E609", {"start": v(-12.89, 24.37) * mm, "end": v(-12.86, 24.29) * mm});
            skLineSegment(sketch, "E610", {"start": v(-12.86, 24.29) * mm, "end": v(-12.82, 24.21) * mm});
            skLineSegment(sketch, "E611", {"start": v(-12.82, 24.21) * mm, "end": v(-12.8, 24.14) * mm});
            skLineSegment(sketch, "E612", {"start": v(-12.8, 24.14) * mm, "end": v(-12.76, 24.08) * mm});
            skLineSegment(sketch, "E613", {"start": v(-12.76, 24.08) * mm, "end": v(-12.74, 24.02) * mm});
            skLineSegment(sketch, "E614", {"start": v(-12.74, 24.02) * mm, "end": v(-12.71, 23.97) * mm});
            skLineSegment(sketch, "E615", {"start": v(-12.71, 23.97) * mm, "end": v(-12.7, 23.93) * mm});
            skLineSegment(sketch, "E616", {"start": v(-12.7, 23.93) * mm, "end": v(-12.67, 23.9) * mm});
            skLineSegment(sketch, "E617", {"start": v(-12.67, 23.9) * mm, "end": v(-12.65, 23.86) * mm});
            skLineSegment(sketch, "E618", {"start": v(-12.65, 23.86) * mm, "end": v(-12.64, 23.83) * mm});
            skLineSegment(sketch, "E619", {"start": v(-12.64, 23.83) * mm, "end": v(-12.62, 23.81) * mm});
            skLineSegment(sketch, "E620", {"start": v(-12.62, 23.81) * mm, "end": v(-12.62, 23.8) * mm});
            skLineSegment(sketch, "E621", {"start": v(-12.62, 23.8) * mm, "end": v(-12.61, 23.8) * mm});
            skLineSegment(sketch, "E622", {"start": v(-12.61, 23.8) * mm, "end": v(-11.92, 22.78) * mm});
            skLineSegment(sketch, "E623", {"start": v(-11.92, 22.78) * mm, "end": v(-14.19, 21.04) * mm});
            skLineSegment(sketch, "E624", {"start": v(-14.19, 21.04) * mm, "end": v(-14.98, 21.96) * mm});
            skLineSegment(sketch, "E625", {"start": v(-14.98, 21.96) * mm, "end": v(-15, 21.97) * mm});
            skLineSegment(sketch, "E626", {"start": v(-15, 21.97) * mm, "end": v(-15, 21.98) * mm});
            skLineSegment(sketch, "E627", {"start": v(-15, 21.98) * mm, "end": v(-15.02, 22) * mm});
            skLineSegment(sketch, "E628", {"start": v(-15.02, 22) * mm, "end": v(-15.04, 22.02) * mm});
            skLineSegment(sketch, "E629", {"start": v(-15.04, 22.02) * mm, "end": v(-15.07, 22.05) * mm});
            skLineSegment(sketch, "E630", {"start": v(-15.07, 22.05) * mm, "end": v(-15.1, 22.08) * mm});
            skLineSegment(sketch, "E631", {"start": v(-15.1, 22.08) * mm, "end": v(-15.14, 22.1) * mm});
            skLineSegment(sketch, "E632", {"start": v(-15.14, 22.1) * mm, "end": v(-15.18, 22.15) * mm});
            skLineSegment(sketch, "E633", {"start": v(-15.18, 22.15) * mm, "end": v(-15.22, 22.19) * mm});
            skLineSegment(sketch, "E634", {"start": v(-15.22, 22.19) * mm, "end": v(-15.28, 22.23) * mm});
            skLineSegment(sketch, "E635", {"start": v(-15.28, 22.23) * mm, "end": v(-15.34, 22.28) * mm});
            skLineSegment(sketch, "E636", {"start": v(-15.34, 22.28) * mm, "end": v(-15.4, 22.33) * mm});
            skLineSegment(sketch, "E637", {"start": v(-15.4, 22.33) * mm, "end": v(-15.47, 22.38) * mm});
            skLineSegment(sketch, "E638", {"start": v(-15.47, 22.38) * mm, "end": v(-15.55, 22.44) * mm});
            skLineSegment(sketch, "E639", {"start": v(-15.55, 22.44) * mm, "end": v(-15.63, 22.5) * mm});
            skLineSegment(sketch, "E640", {"start": v(-15.63, 22.5) * mm, "end": v(-15.72, 22.55) * mm});
            skLineSegment(sketch, "E641", {"start": v(-15.72, 22.55) * mm, "end": v(-15.82, 22.62) * mm});
            skLineSegment(sketch, "E642", {"start": v(-15.82, 22.62) * mm, "end": v(-15.92, 22.68) * mm});
            skLineSegment(sketch, "E643", {"start": v(-15.92, 22.68) * mm, "end": v(-16.03, 22.75) * mm});
            skLineSegment(sketch, "E644", {"start": v(-16.03, 22.75) * mm, "end": v(-16.15, 22.81) * mm});
            skLineSegment(sketch, "E645", {"start": v(-16.15, 22.81) * mm, "end": v(-16.27, 22.88) * mm});
            skLineSegment(sketch, "E646", {"start": v(-16.27, 22.88) * mm, "end": v(-16.4, 22.95) * mm});
            skLineSegment(sketch, "E647", {"start": v(-16.4, 22.95) * mm, "end": v(-16.53, 23.03) * mm});
            skLineSegment(sketch, "E648", {"start": v(-16.53, 23.03) * mm, "end": v(-16.68, 23.1) * mm});
            skLineSegment(sketch, "E649", {"start": v(-16.68, 23.1) * mm, "end": v(-16.83, 23.17) * mm});
            skLineSegment(sketch, "E650", {"start": v(-16.83, 23.17) * mm, "end": v(-16.98, 23.24) * mm});
            skLineSegment(sketch, "E651", {"start": v(-16.98, 23.24) * mm, "end": v(-17.15, 23.32) * mm});
            skLineSegment(sketch, "E652", {"start": v(-17.15, 23.32) * mm, "end": v(-17.32, 23.39) * mm});
            skLineSegment(sketch, "E653", {"start": v(-17.32, 23.39) * mm, "end": v(-17.5, 23.46) * mm});
            skLineSegment(sketch, "E654", {"start": v(-17.5, 23.46) * mm, "end": v(-17.68, 23.53) * mm});
            skLineSegment(sketch, "E655", {"start": v(-17.68, 23.53) * mm, "end": v(-17.87, 23.6) * mm});
            skLineSegment(sketch, "E656", {"start": v(-17.87, 23.6) * mm, "end": v(-18.08, 23.68) * mm});
            skLineSegment(sketch, "E657", {"start": v(-18.08, 23.68) * mm, "end": v(-18.28, 23.75) * mm});
            skLineSegment(sketch, "E658", {"start": v(-18.28, 23.75) * mm, "end": v(-18.5, 23.81) * mm});
            skLineSegment(sketch, "E659", {"start": v(-18.5, 23.81) * mm, "end": v(-18.72, 23.88) * mm});
            skLineSegment(sketch, "E660", {"start": v(-18.72, 23.88) * mm, "end": v(-18.95, 23.94) * mm});
            skLineSegment(sketch, "E661", {"start": v(-18.95, 23.94) * mm, "end": v(-19.05, 23.87) * mm});
            skLineSegment(sketch, "E662", {"start": v(-19.05, 23.87) * mm, "end": v(-20.05, 22.84) * mm});
            skLineSegment(sketch, "E663", {"start": v(-20.05, 22.84) * mm, "end": v(-20.13, 22.73) * mm});
            skLineSegment(sketch, "E664", {"start": v(-20.13, 22.73) * mm, "end": v(-20.06, 22.5) * mm});
            skLineSegment(sketch, "E665", {"start": v(-20.06, 22.5) * mm, "end": v(-19.98, 22.29) * mm});
            skLineSegment(sketch, "E666", {"start": v(-19.98, 22.29) * mm, "end": v(-19.9, 22.07) * mm});
            skLineSegment(sketch, "E667", {"start": v(-19.9, 22.07) * mm, "end": v(-19.83, 21.87) * mm});
            skLineSegment(sketch, "E668", {"start": v(-19.83, 21.87) * mm, "end": v(-19.76, 21.67) * mm});
            skLineSegment(sketch, "E669", {"start": v(-19.76, 21.67) * mm, "end": v(-19.68, 21.48) * mm});
            skLineSegment(sketch, "E670", {"start": v(-19.68, 21.48) * mm, "end": v(-19.6, 21.3) * mm});
            skLineSegment(sketch, "E671", {"start": v(-19.6, 21.3) * mm, "end": v(-19.53, 21.12) * mm});
            skLineSegment(sketch, "E672", {"start": v(-19.53, 21.12) * mm, "end": v(-19.45, 20.95) * mm});
            skLineSegment(sketch, "E673", {"start": v(-19.45, 20.95) * mm, "end": v(-19.37, 20.79) * mm});
            skLineSegment(sketch, "E674", {"start": v(-19.37, 20.79) * mm, "end": v(-19.3, 20.63) * mm});
            skLineSegment(sketch, "E675", {"start": v(-19.3, 20.63) * mm, "end": v(-19.22, 20.49) * mm});
            skLineSegment(sketch, "E676", {"start": v(-19.22, 20.49) * mm, "end": v(-19.14, 20.35) * mm});
            skLineSegment(sketch, "E677", {"start": v(-19.14, 20.35) * mm, "end": v(-19.07, 20.21) * mm});
            skLineSegment(sketch, "E678", {"start": v(-19.07, 20.21) * mm, "end": v(-19, 20.08) * mm});
            skLineSegment(sketch, "E679", {"start": v(-19, 20.08) * mm, "end": v(-18.92, 19.96) * mm});
            skLineSegment(sketch, "E680", {"start": v(-18.92, 19.96) * mm, "end": v(-18.85, 19.85) * mm});
            skLineSegment(sketch, "E681", {"start": v(-18.85, 19.85) * mm, "end": v(-18.78, 19.74) * mm});
            skLineSegment(sketch, "E682", {"start": v(-18.78, 19.74) * mm, "end": v(-18.71, 19.64) * mm});
            skLineSegment(sketch, "E683", {"start": v(-18.71, 19.64) * mm, "end": v(-18.65, 19.55) * mm});
            skLineSegment(sketch, "E684", {"start": v(-18.65, 19.55) * mm, "end": v(-18.59, 19.46) * mm});
            skLineSegment(sketch, "E685", {"start": v(-18.59, 19.46) * mm, "end": v(-18.53, 19.38) * mm});
            skLineSegment(sketch, "E686", {"start": v(-18.53, 19.38) * mm, "end": v(-18.47, 19.3) * mm});
            skLineSegment(sketch, "E687", {"start": v(-18.47, 19.3) * mm, "end": v(-18.41, 19.23) * mm});
            skLineSegment(sketch, "E688", {"start": v(-18.41, 19.23) * mm, "end": v(-18.36, 19.17) * mm});
            skLineSegment(sketch, "E689", {"start": v(-18.36, 19.17) * mm, "end": v(-18.31, 19.11) * mm});
            skLineSegment(sketch, "E690", {"start": v(-18.31, 19.11) * mm, "end": v(-18.27, 19.06) * mm});
            skLineSegment(sketch, "E691", {"start": v(-18.27, 19.06) * mm, "end": v(-18.23, 19.01) * mm});
            skLineSegment(sketch, "E692", {"start": v(-18.23, 19.01) * mm, "end": v(-18.19, 18.97) * mm});
            skLineSegment(sketch, "E693", {"start": v(-18.19, 18.97) * mm, "end": v(-18.15, 18.94) * mm});
            skLineSegment(sketch, "E694", {"start": v(-18.15, 18.94) * mm, "end": v(-18.12, 18.9) * mm});
            skLineSegment(sketch, "E695", {"start": v(-18.12, 18.9) * mm, "end": v(-18.1, 18.88) * mm});
            skLineSegment(sketch, "E696", {"start": v(-18.1, 18.88) * mm, "end": v(-18.08, 18.86) * mm});
            skLineSegment(sketch, "E697", {"start": v(-18.08, 18.86) * mm, "end": v(-18.06, 18.84) * mm});
            skLineSegment(sketch, "E698", {"start": v(-18.06, 18.84) * mm, "end": v(-18.05, 18.83) * mm});
            skLineSegment(sketch, "E699", {"start": v(-18.05, 18.83) * mm, "end": v(-18.04, 18.83) * mm});
            skLineSegment(sketch, "E700", {"start": v(-18.04, 18.83) * mm, "end": v(-17.1, 18.05) * mm});
            skLineSegment(sketch, "E701", {"start": v(-17.1, 18.05) * mm, "end": v(-18.78, 15.74) * mm});
            skLineSegment(sketch, "E702", {"start": v(-18.78, 15.74) * mm, "end": v(-19.8, 16.4) * mm});
            skLineSegment(sketch, "E703", {"start": v(-19.8, 16.4) * mm, "end": v(-19.81, 16.4) * mm});
            skLineSegment(sketch, "E704", {"start": v(-19.81, 16.4) * mm, "end": v(-19.83, 16.42) * mm});
            skLineSegment(sketch, "E705", {"start": v(-19.83, 16.42) * mm, "end": v(-19.85, 16.43) * mm});
            skLineSegment(sketch, "E706", {"start": v(-19.85, 16.43) * mm, "end": v(-19.87, 16.44) * mm});
            skLineSegment(sketch, "E707", {"start": v(-19.87, 16.44) * mm, "end": v(-19.9, 16.46) * mm});
            skLineSegment(sketch, "E708", {"start": v(-19.9, 16.46) * mm, "end": v(-19.94, 16.48) * mm});
            skLineSegment(sketch, "E709", {"start": v(-19.94, 16.48) * mm, "end": v(-19.99, 16.5) * mm});
            skLineSegment(sketch, "E710", {"start": v(-19.99, 16.5) * mm, "end": v(-20.04, 16.52) * mm});
            skLineSegment(sketch, "E711", {"start": v(-20.04, 16.52) * mm, "end": v(-20.1, 16.55) * mm});
            skLineSegment(sketch, "E712", {"start": v(-20.1, 16.55) * mm, "end": v(-20.16, 16.58) * mm});
            skLineSegment(sketch, "E713", {"start": v(-20.16, 16.58) * mm, "end": v(-20.23, 16.6) * mm});
            skLineSegment(sketch, "E714", {"start": v(-20.23, 16.6) * mm, "end": v(-20.3, 16.64) * mm});
            skLineSegment(sketch, "E715", {"start": v(-20.3, 16.64) * mm, "end": v(-20.39, 16.67) * mm});
            skLineSegment(sketch, "E716", {"start": v(-20.39, 16.67) * mm, "end": v(-20.48, 16.7) * mm});
            skLineSegment(sketch, "E717", {"start": v(-20.48, 16.7) * mm, "end": v(-20.57, 16.73) * mm});
            skLineSegment(sketch, "E718", {"start": v(-20.57, 16.73) * mm, "end": v(-20.68, 16.76) * mm});
            skLineSegment(sketch, "E719", {"start": v(-20.68, 16.76) * mm, "end": v(-20.79, 16.8) * mm});
            skLineSegment(sketch, "E720", {"start": v(-20.79, 16.8) * mm, "end": v(-20.9, 16.83) * mm});
            skLineSegment(sketch, "E721", {"start": v(-20.9, 16.83) * mm, "end": v(-21.03, 16.86) * mm});
            skLineSegment(sketch, "E722", {"start": v(-21.03, 16.86) * mm, "end": v(-21.16, 16.9) * mm});
            skLineSegment(sketch, "E723", {"start": v(-21.16, 16.9) * mm, "end": v(-21.3, 16.93) * mm});
            skLineSegment(sketch, "E724", {"start": v(-21.3, 16.93) * mm, "end": v(-21.44, 16.96) * mm});
            skLineSegment(sketch, "E725", {"start": v(-21.44, 16.96) * mm, "end": v(-21.59, 16.99) * mm});
            skLineSegment(sketch, "E726", {"start": v(-21.59, 16.99) * mm, "end": v(-21.74, 17.02) * mm});
            skLineSegment(sketch, "E727", {"start": v(-21.74, 17.02) * mm, "end": v(-21.9, 17.04) * mm});
            skLineSegment(sketch, "E728", {"start": v(-21.9, 17.04) * mm, "end": v(-22.08, 17.07) * mm});
            skLineSegment(sketch, "E729", {"start": v(-22.08, 17.07) * mm, "end": v(-22.26, 17.1) * mm});
            skLineSegment(sketch, "E730", {"start": v(-22.26, 17.1) * mm, "end": v(-22.44, 17.11) * mm});
            skLineSegment(sketch, "E731", {"start": v(-22.44, 17.11) * mm, "end": v(-22.63, 17.13) * mm});
            skLineSegment(sketch, "E732", {"start": v(-22.63, 17.13) * mm, "end": v(-22.83, 17.15) * mm});
            skLineSegment(sketch, "E733", {"start": v(-22.83, 17.15) * mm, "end": v(-23.04, 17.16) * mm});
            skLineSegment(sketch, "E734", {"start": v(-23.04, 17.16) * mm, "end": v(-23.25, 17.18) * mm});
            skLineSegment(sketch, "E735", {"start": v(-23.25, 17.18) * mm, "end": v(-23.47, 17.18) * mm});
            skLineSegment(sketch, "E736", {"start": v(-23.47, 17.18) * mm, "end": v(-23.7, 17.19) * mm});
            skLineSegment(sketch, "E737", {"start": v(-23.7, 17.19) * mm, "end": v(-23.92, 17.2) * mm});
            skLineSegment(sketch, "E738", {"start": v(-23.92, 17.2) * mm, "end": v(-24.16, 17.19) * mm});
            skLineSegment(sketch, "E739", {"start": v(-24.16, 17.19) * mm, "end": v(-24.24, 17.09) * mm});
            skLineSegment(sketch, "E740", {"start": v(-24.24, 17.09) * mm, "end": v(-24.9, 15.81) * mm});
            skLineSegment(sketch, "E741", {"start": v(-24.9, 15.81) * mm, "end": v(-24.95, 15.7) * mm});
            skLineSegment(sketch, "E742", {"start": v(-24.95, 15.7) * mm, "end": v(-24.82, 15.5) * mm});
            skLineSegment(sketch, "E743", {"start": v(-24.82, 15.5) * mm, "end": v(-24.69, 15.3) * mm});
            skLineSegment(sketch, "E744", {"start": v(-24.69, 15.3) * mm, "end": v(-24.56, 15.12) * mm});
            skLineSegment(sketch, "E745", {"start": v(-24.56, 15.12) * mm, "end": v(-24.43, 14.95) * mm});
            skLineSegment(sketch, "E746", {"start": v(-24.43, 14.95) * mm, "end": v(-24.3, 14.78) * mm});
            skLineSegment(sketch, "E747", {"start": v(-24.3, 14.78) * mm, "end": v(-24.17, 14.62) * mm});
            skLineSegment(sketch, "E748", {"start": v(-24.17, 14.62) * mm, "end": v(-24.05, 14.46) * mm});
            skLineSegment(sketch, "E749", {"start": v(-24.05, 14.46) * mm, "end": v(-23.92, 14.32) * mm});
            skLineSegment(sketch, "E750", {"start": v(-23.92, 14.32) * mm, "end": v(-23.8, 14.18) * mm});
            skLineSegment(sketch, "E751", {"start": v(-23.8, 14.18) * mm, "end": v(-23.68, 14.04) * mm});
            skLineSegment(sketch, "E752", {"start": v(-23.68, 14.04) * mm, "end": v(-23.56, 13.91) * mm});
            skLineSegment(sketch, "E753", {"start": v(-23.56, 13.91) * mm, "end": v(-23.45, 13.8) * mm});
            skLineSegment(sketch, "E754", {"start": v(-23.45, 13.8) * mm, "end": v(-23.34, 13.68) * mm});
            skLineSegment(sketch, "E755", {"start": v(-23.34, 13.68) * mm, "end": v(-23.23, 13.57) * mm});
            skLineSegment(sketch, "E756", {"start": v(-23.23, 13.57) * mm, "end": v(-23.12, 13.47) * mm});
            skLineSegment(sketch, "E757", {"start": v(-23.12, 13.47) * mm, "end": v(-23.02, 13.38) * mm});
            skLineSegment(sketch, "E758", {"start": v(-23.02, 13.38) * mm, "end": v(-22.92, 13.29) * mm});
            skLineSegment(sketch, "E759", {"start": v(-22.92, 13.29) * mm, "end": v(-22.82, 13.2) * mm});
            skLineSegment(sketch, "E760", {"start": v(-22.82, 13.2) * mm, "end": v(-22.73, 13.13) * mm});
            skLineSegment(sketch, "E761", {"start": v(-22.73, 13.13) * mm, "end": v(-22.64, 13.05) * mm});
            skLineSegment(sketch, "E762", {"start": v(-22.64, 13.05) * mm, "end": v(-22.55, 12.99) * mm});
            skLineSegment(sketch, "E763", {"start": v(-22.55, 12.99) * mm, "end": v(-22.47, 12.93) * mm});
            skLineSegment(sketch, "E764", {"start": v(-22.47, 12.93) * mm, "end": v(-22.4, 12.87) * mm});
            skLineSegment(sketch, "E765", {"start": v(-22.4, 12.87) * mm, "end": v(-22.32, 12.82) * mm});
            skLineSegment(sketch, "E766", {"start": v(-22.32, 12.82) * mm, "end": v(-22.26, 12.77) * mm});
            skLineSegment(sketch, "E767", {"start": v(-22.26, 12.77) * mm, "end": v(-22.2, 12.73) * mm});
            skLineSegment(sketch, "E768", {"start": v(-22.2, 12.73) * mm, "end": v(-22.13, 12.7) * mm});
            skLineSegment(sketch, "E769", {"start": v(-22.13, 12.7) * mm, "end": v(-22.08, 12.66) * mm});
            skLineSegment(sketch, "E770", {"start": v(-22.08, 12.66) * mm, "end": v(-22.03, 12.63) * mm});
            skLineSegment(sketch, "E771", {"start": v(-22.03, 12.63) * mm, "end": v(-22, 12.6) * mm});
            skLineSegment(sketch, "E772", {"start": v(-22, 12.6) * mm, "end": v(-21.95, 12.59) * mm});
            skLineSegment(sketch, "E773", {"start": v(-21.95, 12.59) * mm, "end": v(-21.92, 12.57) * mm});
            skLineSegment(sketch, "E774", {"start": v(-21.92, 12.57) * mm, "end": v(-21.9, 12.56) * mm});
            skLineSegment(sketch, "E775", {"start": v(-21.9, 12.56) * mm, "end": v(-21.87, 12.54) * mm});
            skLineSegment(sketch, "E776", {"start": v(-21.87, 12.54) * mm, "end": v(-21.86, 12.54) * mm});
            skLineSegment(sketch, "E777", {"start": v(-21.86, 12.54) * mm, "end": v(-21.85, 12.53) * mm});
            skLineSegment(sketch, "E778", {"start": v(-21.85, 12.53) * mm, "end": v(-20.73, 12.06) * mm});
            skLineSegment(sketch, "E779", {"start": v(-20.73, 12.06) * mm, "end": v(-21.69, 9.37) * mm});
            skLineSegment(sketch, "E780", {"start": v(-21.69, 9.37) * mm, "end": v(-22.86, 9.71) * mm});
            skLineSegment(sketch, "E781", {"start": v(-22.86, 9.71) * mm, "end": v(-22.87, 9.71) * mm});
            skLineSegment(sketch, "E782", {"start": v(-22.87, 9.71) * mm, "end": v(-22.88, 9.72) * mm});
            skLineSegment(sketch, "E783", {"start": v(-22.88, 9.72) * mm, "end": v(-22.9, 9.72) * mm});
            skLineSegment(sketch, "E784", {"start": v(-22.9, 9.72) * mm, "end": v(-22.94, 9.73) * mm});
            skLineSegment(sketch, "E785", {"start": v(-22.94, 9.73) * mm, "end": v(-22.97, 9.74) * mm});
            skLineSegment(sketch, "E786", {"start": v(-22.97, 9.74) * mm, "end": v(-23.01, 9.75) * mm});
            skLineSegment(sketch, "E787", {"start": v(-23.01, 9.75) * mm, "end": v(-23.06, 9.75) * mm});
            skLineSegment(sketch, "E788", {"start": v(-23.06, 9.75) * mm, "end": v(-23.12, 9.76) * mm});
            skLineSegment(sketch, "E789", {"start": v(-23.12, 9.76) * mm, "end": v(-23.18, 9.77) * mm});
            skLineSegment(sketch, "E790", {"start": v(-23.18, 9.77) * mm, "end": v(-23.25, 9.78) * mm});
            skLineSegment(sketch, "E791", {"start": v(-23.25, 9.78) * mm, "end": v(-23.32, 9.79) * mm});
            skLineSegment(sketch, "E792", {"start": v(-23.32, 9.79) * mm, "end": v(-23.4, 9.8) * mm});
            skLineSegment(sketch, "E793", {"start": v(-23.4, 9.8) * mm, "end": v(-23.5, 9.8) * mm});
            skLineSegment(sketch, "E794", {"start": v(-23.5, 9.8) * mm, "end": v(-23.59, 9.8) * mm});
            skLineSegment(sketch, "E795", {"start": v(-23.59, 9.8) * mm, "end": v(-23.7, 9.8) * mm});
            skLineSegment(sketch, "E796", {"start": v(-23.7, 9.8) * mm, "end": v(-23.8, 9.81) * mm});
            skLineSegment(sketch, "E797", {"start": v(-23.8, 9.81) * mm, "end": v(-23.91, 9.81) * mm});
            skLineSegment(sketch, "E798", {"start": v(-23.91, 9.81) * mm, "end": v(-24.03, 9.8) * mm});
            skLineSegment(sketch, "E799", {"start": v(-24.03, 9.8) * mm, "end": v(-24.16, 9.8) * mm});
            skLineSegment(sketch, "E800", {"start": v(-24.16, 9.8) * mm, "end": v(-24.3, 9.8) * mm});
            skLineSegment(sketch, "E801", {"start": v(-24.3, 9.8) * mm, "end": v(-24.44, 9.8) * mm});
            skLineSegment(sketch, "E802", {"start": v(-24.44, 9.8) * mm, "end": v(-24.58, 9.78) * mm});
            skLineSegment(sketch, "E803", {"start": v(-24.58, 9.78) * mm, "end": v(-24.74, 9.77) * mm});
            skLineSegment(sketch, "E804", {"start": v(-24.74, 9.77) * mm, "end": v(-24.9, 9.75) * mm});
            skLineSegment(sketch, "E805", {"start": v(-24.9, 9.75) * mm, "end": v(-25.06, 9.73) * mm});
            skLineSegment(sketch, "E806", {"start": v(-25.06, 9.73) * mm, "end": v(-25.23, 9.7) * mm});
            skLineSegment(sketch, "E807", {"start": v(-25.23, 9.7) * mm, "end": v(-25.4, 9.68) * mm});
            skLineSegment(sketch, "E808", {"start": v(-25.4, 9.68) * mm, "end": v(-25.6, 9.65) * mm});
            skLineSegment(sketch, "E809", {"start": v(-25.6, 9.65) * mm, "end": v(-25.78, 9.61) * mm});
            skLineSegment(sketch, "E810", {"start": v(-25.78, 9.61) * mm, "end": v(-25.98, 9.57) * mm});
            skLineSegment(sketch, "E811", {"start": v(-25.98, 9.57) * mm, "end": v(-26.18, 9.53) * mm});
            skLineSegment(sketch, "E812", {"start": v(-26.18, 9.53) * mm, "end": v(-26.38, 9.48) * mm});
            skLineSegment(sketch, "E813", {"start": v(-26.38, 9.48) * mm, "end": v(-26.6, 9.43) * mm});
            skLineSegment(sketch, "E814", {"start": v(-26.6, 9.43) * mm, "end": v(-26.81, 9.37) * mm});
            skLineSegment(sketch, "E815", {"start": v(-26.81, 9.37) * mm, "end": v(-27.04, 9.3) * mm});
            skLineSegment(sketch, "E816", {"start": v(-27.04, 9.3) * mm, "end": v(-27.26, 9.24) * mm});
            skLineSegment(sketch, "E817", {"start": v(-27.26, 9.24) * mm, "end": v(-27.3, 9.12) * mm});
            skLineSegment(sketch, "E818", {"start": v(-27.3, 9.12) * mm, "end": v(-27.6, 7.7) * mm});
            skLineSegment(sketch, "E819", {"start": v(-27.6, 7.7) * mm, "end": v(-27.6, 7.58) * mm});
            skLineSegment(sketch, "E820", {"start": v(-27.6, 7.58) * mm, "end": v(-27.42, 7.43) * mm});
            skLineSegment(sketch, "E821", {"start": v(-27.42, 7.43) * mm, "end": v(-27.24, 7.28) * mm});
            skLineSegment(sketch, "E822", {"start": v(-27.24, 7.28) * mm, "end": v(-27.06, 7.14) * mm});
            skLineSegment(sketch, "E823", {"start": v(-27.06, 7.14) * mm, "end": v(-26.89, 7.01) * mm});
            skLineSegment(sketch, "E824", {"start": v(-26.89, 7.01) * mm, "end": v(-26.72, 6.89) * mm});
            skLineSegment(sketch, "E825", {"start": v(-26.72, 6.89) * mm, "end": v(-26.55, 6.77) * mm});
            skLineSegment(sketch, "E826", {"start": v(-26.55, 6.77) * mm, "end": v(-26.38, 6.65) * mm});
            skLineSegment(sketch, "E827", {"start": v(-26.38, 6.65) * mm, "end": v(-26.22, 6.55) * mm});
            skLineSegment(sketch, "E828", {"start": v(-26.22, 6.55) * mm, "end": v(-26.07, 6.45) * mm});
            skLineSegment(sketch, "E829", {"start": v(-26.07, 6.45) * mm, "end": v(-25.91, 6.35) * mm});
            skLineSegment(sketch, "E830", {"start": v(-25.91, 6.35) * mm, "end": v(-25.77, 6.26) * mm});
            skLineSegment(sketch, "E831", {"start": v(-25.77, 6.26) * mm, "end": v(-25.62, 6.18) * mm});
            skLineSegment(sketch, "E832", {"start": v(-25.62, 6.18) * mm, "end": v(-25.48, 6.1) * mm});
            skLineSegment(sketch, "E833", {"start": v(-25.48, 6.1) * mm, "end": v(-25.35, 6.03) * mm});
            skLineSegment(sketch, "E834", {"start": v(-25.35, 6.03) * mm, "end": v(-25.22, 5.96) * mm});
            skLineSegment(sketch, "E835", {"start": v(-25.22, 5.96) * mm, "end": v(-25.09, 5.9) * mm});
            skLineSegment(sketch, "E836", {"start": v(-25.09, 5.9) * mm, "end": v(-24.97, 5.84) * mm});
            skLineSegment(sketch, "E837", {"start": v(-24.97, 5.84) * mm, "end": v(-24.85, 5.8) * mm});
            skLineSegment(sketch, "E838", {"start": v(-24.85, 5.8) * mm, "end": v(-24.74, 5.74) * mm});
            skLineSegment(sketch, "E839", {"start": v(-24.74, 5.74) * mm, "end": v(-24.64, 5.7) * mm});
            skLineSegment(sketch, "E840", {"start": v(-24.64, 5.7) * mm, "end": v(-24.53, 5.66) * mm});
            skLineSegment(sketch, "E841", {"start": v(-24.53, 5.66) * mm, "end": v(-24.44, 5.62) * mm});
            skLineSegment(sketch, "E842", {"start": v(-24.44, 5.62) * mm, "end": v(-24.35, 5.6) * mm});
            skLineSegment(sketch, "E843", {"start": v(-24.35, 5.6) * mm, "end": v(-24.27, 5.56) * mm});
            skLineSegment(sketch, "E844", {"start": v(-24.27, 5.56) * mm, "end": v(-24.19, 5.54) * mm});
            skLineSegment(sketch, "E845", {"start": v(-24.19, 5.54) * mm, "end": v(-24.12, 5.51) * mm});
            skLineSegment(sketch, "E846", {"start": v(-24.12, 5.51) * mm, "end": v(-24.05, 5.5) * mm});
            skLineSegment(sketch, "E847", {"start": v(-24.05, 5.5) * mm, "end": v(-24, 5.48) * mm});
            skLineSegment(sketch, "E848", {"start": v(-24, 5.48) * mm, "end": v(-23.94, 5.46) * mm});
            skLineSegment(sketch, "E849", {"start": v(-23.94, 5.46) * mm, "end": v(-23.89, 5.45) * mm});
            skLineSegment(sketch, "E850", {"start": v(-23.89, 5.45) * mm, "end": v(-23.85, 5.44) * mm});
            skLineSegment(sketch, "E851", {"start": v(-23.85, 5.44) * mm, "end": v(-23.81, 5.44) * mm});
            skLineSegment(sketch, "E852", {"start": v(-23.81, 5.44) * mm, "end": v(-23.78, 5.43) * mm});
            skLineSegment(sketch, "E853", {"start": v(-23.78, 5.43) * mm, "end": v(-23.76, 5.43) * mm});
            skLineSegment(sketch, "E854", {"start": v(-23.76, 5.43) * mm, "end": v(-23.74, 5.42) * mm});
            skLineSegment(sketch, "E855", {"start": v(-23.74, 5.42) * mm, "end": v(-23.73, 5.42) * mm});
            skLineSegment(sketch, "E856", {"start": v(-23.73, 5.42) * mm, "end": v(-22.52, 5.28) * mm});
            skLineSegment(sketch, "E857", {"start": v(-22.52, 5.28) * mm, "end": v(-22.68, 2.43) * mm});
            skLineSegment(sketch, "E858", {"start": v(-22.68, 2.43) * mm, "end": v(-23.9, 2.43) * mm});
            skLineSegment(sketch, "E859", {"start": v(-23.9, 2.43) * mm, "end": v(-23.92, 2.43) * mm});
            skLineSegment(sketch, "E860", {"start": v(-23.92, 2.43) * mm, "end": v(-23.93, 2.43) * mm});
            skLineSegment(sketch, "E861", {"start": v(-23.93, 2.43) * mm, "end": v(-23.96, 2.43) * mm});
            skLineSegment(sketch, "E862", {"start": v(-23.96, 2.43) * mm, "end": v(-23.99, 2.43) * mm});
            skLineSegment(sketch, "E863", {"start": v(-23.99, 2.43) * mm, "end": v(-24.02, 2.42) * mm});
            skLineSegment(sketch, "E864", {"start": v(-24.02, 2.42) * mm, "end": v(-24.06, 2.42) * mm});
            skLineSegment(sketch, "E865", {"start": v(-24.06, 2.42) * mm, "end": v(-24.11, 2.41) * mm});
            skLineSegment(sketch, "E866", {"start": v(-24.11, 2.41) * mm, "end": v(-24.17, 2.4) * mm});
            skLineSegment(sketch, "E867", {"start": v(-24.17, 2.4) * mm, "end": v(-24.23, 2.4) * mm});
            skLineSegment(sketch, "E868", {"start": v(-24.23, 2.4) * mm, "end": v(-24.3, 2.38) * mm});
            skLineSegment(sketch, "E869", {"start": v(-24.3, 2.38) * mm, "end": v(-24.37, 2.37) * mm});
            skLineSegment(sketch, "E870", {"start": v(-24.37, 2.37) * mm, "end": v(-24.45, 2.35) * mm});
            skLineSegment(sketch, "E871", {"start": v(-24.45, 2.35) * mm, "end": v(-24.54, 2.33) * mm});
            skLineSegment(sketch, "E872", {"start": v(-24.54, 2.33) * mm, "end": v(-24.63, 2.31) * mm});
            skLineSegment(sketch, "E873", {"start": v(-24.63, 2.31) * mm, "end": v(-24.73, 2.29) * mm});
            skLineSegment(sketch, "E874", {"start": v(-24.73, 2.29) * mm, "end": v(-24.84, 2.26) * mm});
            skLineSegment(sketch, "E875", {"start": v(-24.84, 2.26) * mm, "end": v(-24.94, 2.23) * mm});
            skLineSegment(sketch, "E876", {"start": v(-24.94, 2.23) * mm, "end": v(-25.06, 2.2) * mm});
            skLineSegment(sketch, "E877", {"start": v(-25.06, 2.2) * mm, "end": v(-25.18, 2.15) * mm});
            skLineSegment(sketch, "E878", {"start": v(-25.18, 2.15) * mm, "end": v(-25.3, 2.11) * mm});
            skLineSegment(sketch, "E879", {"start": v(-25.3, 2.11) * mm, "end": v(-25.44, 2.06) * mm});
            skLineSegment(sketch, "E880", {"start": v(-25.44, 2.06) * mm, "end": v(-25.58, 2.01) * mm});
            skLineSegment(sketch, "E881", {"start": v(-25.58, 2.01) * mm, "end": v(-25.72, 1.96) * mm});
            skLineSegment(sketch, "E882", {"start": v(-25.72, 1.96) * mm, "end": v(-25.87, 1.9) * mm});
            skLineSegment(sketch, "E883", {"start": v(-25.87, 1.9) * mm, "end": v(-26.02, 1.83) * mm});
            skLineSegment(sketch, "E884", {"start": v(-26.02, 1.83) * mm, "end": v(-26.18, 1.76) * mm});
            skLineSegment(sketch, "E885", {"start": v(-26.18, 1.76) * mm, "end": v(-26.34, 1.68) * mm});
            skLineSegment(sketch, "E886", {"start": v(-26.34, 1.68) * mm, "end": v(-26.51, 1.6) * mm});
            skLineSegment(sketch, "E887", {"start": v(-26.51, 1.6) * mm, "end": v(-26.68, 1.51) * mm});
            skLineSegment(sketch, "E888", {"start": v(-26.68, 1.51) * mm, "end": v(-26.86, 1.42) * mm});
            skLineSegment(sketch, "E889", {"start": v(-26.86, 1.42) * mm, "end": v(-27.04, 1.32) * mm});
            skLineSegment(sketch, "E890", {"start": v(-27.04, 1.32) * mm, "end": v(-27.22, 1.22) * mm});
            skLineSegment(sketch, "E891", {"start": v(-27.22, 1.22) * mm, "end": v(-27.41, 1.1) * mm});
            skLineSegment(sketch, "E892", {"start": v(-27.41, 1.1) * mm, "end": v(-27.6, 0.99) * mm});
            skLineSegment(sketch, "E893", {"start": v(-27.6, 0.99) * mm, "end": v(-27.8, 0.86) * mm});
            skLineSegment(sketch, "E894", {"start": v(-27.8, 0.86) * mm, "end": v(-28, 0.73) * mm});
            skLineSegment(sketch, "E895", {"start": v(-28, 0.73) * mm, "end": v(-28, 0.6) * mm});
            skLineSegment(sketch, "E896", {"start": v(-28, 0.6) * mm, "end": v(-27.88, -0.83) * mm});
            skLineSegment(sketch, "E897", {"start": v(-27.88, -0.83) * mm, "end": v(-27.85, -0.95) * mm});
            skLineSegment(sketch, "E898", {"start": v(-27.85, -0.95) * mm, "end": v(-27.64, -1.05) * mm});
            skLineSegment(sketch, "E899", {"start": v(-27.64, -1.05) * mm, "end": v(-27.42, -1.13) * mm});
            skLineSegment(sketch, "E900", {"start": v(-27.42, -1.13) * mm, "end": v(-27.21, -1.22) * mm});
            skLineSegment(sketch, "E901", {"start": v(-27.21, -1.22) * mm, "end": v(-27, -1.3) * mm});
            skLineSegment(sketch, "E902", {"start": v(-27, -1.3) * mm, "end": v(-26.81, -1.37) * mm});
            skLineSegment(sketch, "E903", {"start": v(-26.81, -1.37) * mm, "end": v(-26.62, -1.43) * mm});
            skLineSegment(sketch, "E904", {"start": v(-26.62, -1.43) * mm, "end": v(-26.43, -1.5) * mm});
            skLineSegment(sketch, "E905", {"start": v(-26.43, -1.5) * mm, "end": v(-26.24, -1.55) * mm});
            skLineSegment(sketch, "E906", {"start": v(-26.24, -1.55) * mm, "end": v(-26.06, -1.6) * mm});
            skLineSegment(sketch, "E907", {"start": v(-26.06, -1.6) * mm, "end": v(-25.9, -1.65) * mm});
            skLineSegment(sketch, "E908", {"start": v(-25.9, -1.65) * mm, "end": v(-25.72, -1.7) * mm});
            skLineSegment(sketch, "E909", {"start": v(-25.72, -1.7) * mm, "end": v(-25.56, -1.74) * mm});
            skLineSegment(sketch, "E910", {"start": v(-25.56, -1.74) * mm, "end": v(-25.4, -1.77) * mm});
            skLineSegment(sketch, "E911", {"start": v(-25.4, -1.77) * mm, "end": v(-25.25, -1.8) * mm});
            skLineSegment(sketch, "E912", {"start": v(-25.25, -1.8) * mm, "end": v(-25.11, -1.83) * mm});
            skLineSegment(sketch, "E913", {"start": v(-25.11, -1.83) * mm, "end": v(-24.97, -1.85) * mm});
            skLineSegment(sketch, "E914", {"start": v(-24.97, -1.85) * mm, "end": v(-24.84, -1.87) * mm});
            skLineSegment(sketch, "E915", {"start": v(-24.84, -1.87) * mm, "end": v(-24.71, -1.9) * mm});
            skLineSegment(sketch, "E916", {"start": v(-24.71, -1.9) * mm, "end": v(-24.6, -1.9) * mm});
            skLineSegment(sketch, "E917", {"start": v(-24.6, -1.9) * mm, "end": v(-24.48, -1.92) * mm});
            skLineSegment(sketch, "E918", {"start": v(-24.48, -1.92) * mm, "end": v(-24.37, -1.93) * mm});
            skLineSegment(sketch, "E919", {"start": v(-24.37, -1.93) * mm, "end": v(-24.27, -1.94) * mm});
            skLineSegment(sketch, "E920", {"start": v(-24.27, -1.94) * mm, "end": v(-24.18, -1.94) * mm});
            skLineSegment(sketch, "E921", {"start": v(-24.18, -1.94) * mm, "end": v(-24.09, -1.95) * mm});
            skLineSegment(sketch, "E922", {"start": v(-24.09, -1.95) * mm, "end": v(-24, -1.95) * mm});
            skLineSegment(sketch, "E923", {"start": v(-24, -1.95) * mm, "end": v(-23.93, -1.95) * mm});
            skLineSegment(sketch, "E924", {"start": v(-23.93, -1.95) * mm, "end": v(-23.86, -1.95) * mm});
            skLineSegment(sketch, "E925", {"start": v(-23.86, -1.95) * mm, "end": v(-23.8, -1.95) * mm});
            skLineSegment(sketch, "E926", {"start": v(-23.8, -1.95) * mm, "end": v(-23.74, -1.95) * mm});
            skLineSegment(sketch, "E927", {"start": v(-23.74, -1.95) * mm, "end": v(-23.7, -1.95) * mm});
            skLineSegment(sketch, "E928", {"start": v(-23.7, -1.95) * mm, "end": v(-23.65, -1.94) * mm});
            skLineSegment(sketch, "E929", {"start": v(-23.65, -1.94) * mm, "end": v(-23.61, -1.94) * mm});
            skLineSegment(sketch, "E930", {"start": v(-23.61, -1.94) * mm, "end": v(-23.58, -1.94) * mm});
            skLineSegment(sketch, "E931", {"start": v(-23.58, -1.94) * mm, "end": v(-23.56, -1.94) * mm});
            skLineSegment(sketch, "E932", {"start": v(-23.56, -1.94) * mm, "end": v(-23.54, -1.93) * mm});
            skLineSegment(sketch, "E933", {"start": v(-23.54, -1.93) * mm, "end": v(-23.53, -1.93) * mm});
            skLineSegment(sketch, "E934", {"start": v(-23.53, -1.93) * mm, "end": v(-22.33, -1.73) * mm});
            skLineSegment(sketch, "E935", {"start": v(-22.33, -1.73) * mm, "end": v(-21.69, -4.5) * mm});
            skLineSegment(sketch, "E936", {"start": v(-21.69, -4.5) * mm, "end": v(-22.86, -4.85) * mm});
            skLineSegment(sketch, "E937", {"start": v(-22.86, -4.85) * mm, "end": v(-22.87, -4.85) * mm});
            skLineSegment(sketch, "E938", {"start": v(-22.87, -4.85) * mm, "end": v(-22.88, -4.86) * mm});
            skLineSegment(sketch, "E939", {"start": v(-22.88, -4.86) * mm, "end": v(-22.9, -4.87) * mm});
            skLineSegment(sketch, "E940", {"start": v(-22.9, -4.87) * mm, "end": v(-22.93, -4.88) * mm});
            skLineSegment(sketch, "E941", {"start": v(-22.93, -4.88) * mm, "end": v(-22.97, -4.9) * mm});
            skLineSegment(sketch, "E942", {"start": v(-22.97, -4.9) * mm, "end": v(-23, -4.9) * mm});
            skLineSegment(sketch, "E943", {"start": v(-23, -4.9) * mm, "end": v(-23.05, -4.93) * mm});
            skLineSegment(sketch, "E944", {"start": v(-23.05, -4.93) * mm, "end": v(-23.1, -4.95) * mm});
            skLineSegment(sketch, "E945", {"start": v(-23.1, -4.95) * mm, "end": v(-23.16, -4.98) * mm});
            skLineSegment(sketch, "E946", {"start": v(-23.16, -4.98) * mm, "end": v(-23.22, -5) * mm});
            skLineSegment(sketch, "E947", {"start": v(-23.22, -5) * mm, "end": v(-23.3, -5.04) * mm});
            skLineSegment(sketch, "E948", {"start": v(-23.3, -5.04) * mm, "end": v(-23.36, -5.08) * mm});
            skLineSegment(sketch, "E949", {"start": v(-23.36, -5.08) * mm, "end": v(-23.44, -5.12) * mm});
            skLineSegment(sketch, "E950", {"start": v(-23.44, -5.12) * mm, "end": v(-23.52, -5.17) * mm});
            skLineSegment(sketch, "E951", {"start": v(-23.52, -5.17) * mm, "end": v(-23.61, -5.22) * mm});
            skLineSegment(sketch, "E952", {"start": v(-23.61, -5.22) * mm, "end": v(-23.7, -5.28) * mm});
            skLineSegment(sketch, "E953", {"start": v(-23.7, -5.28) * mm, "end": v(-23.8, -5.34) * mm});
            skLineSegment(sketch, "E954", {"start": v(-23.8, -5.34) * mm, "end": v(-23.9, -5.4) * mm});
            skLineSegment(sketch, "E955", {"start": v(-23.9, -5.4) * mm, "end": v(-24, -5.48) * mm});
            skLineSegment(sketch, "E956", {"start": v(-24, -5.48) * mm, "end": v(-24.12, -5.55) * mm});
            skLineSegment(sketch, "E957", {"start": v(-24.12, -5.55) * mm, "end": v(-24.23, -5.64) * mm});
            skLineSegment(sketch, "E958", {"start": v(-24.23, -5.64) * mm, "end": v(-24.35, -5.72) * mm});
            skLineSegment(sketch, "E959", {"start": v(-24.35, -5.72) * mm, "end": v(-24.47, -5.82) * mm});
            skLineSegment(sketch, "E960", {"start": v(-24.47, -5.82) * mm, "end": v(-24.6, -5.92) * mm});
            skLineSegment(sketch, "E961", {"start": v(-24.6, -5.92) * mm, "end": v(-24.72, -6.02) * mm});
            skLineSegment(sketch, "E962", {"start": v(-24.72, -6.02) * mm, "end": v(-24.85, -6.14) * mm});
            skLineSegment(sketch, "E963", {"start": v(-24.85, -6.14) * mm, "end": v(-24.99, -6.26) * mm});
            skLineSegment(sketch, "E964", {"start": v(-24.99, -6.26) * mm, "end": v(-25.12, -6.38) * mm});
            skLineSegment(sketch, "E965", {"start": v(-25.12, -6.38) * mm, "end": v(-25.26, -6.51) * mm});
            skLineSegment(sketch, "E966", {"start": v(-25.26, -6.51) * mm, "end": v(-25.4, -6.65) * mm});
            skLineSegment(sketch, "E967", {"start": v(-25.4, -6.65) * mm, "end": v(-25.55, -6.8) * mm});
            skLineSegment(sketch, "E968", {"start": v(-25.55, -6.8) * mm, "end": v(-25.7, -6.95) * mm});
            skLineSegment(sketch, "E969", {"start": v(-25.7, -6.95) * mm, "end": v(-25.85, -7.11) * mm});
            skLineSegment(sketch, "E970", {"start": v(-25.85, -7.11) * mm, "end": v(-26, -7.28) * mm});
            skLineSegment(sketch, "E971", {"start": v(-26, -7.28) * mm, "end": v(-26.15, -7.45) * mm});
            skLineSegment(sketch, "E972", {"start": v(-26.15, -7.45) * mm, "end": v(-26.3, -7.63) * mm});
            skLineSegment(sketch, "E973", {"start": v(-26.3, -7.63) * mm, "end": v(-26.28, -7.75) * mm});
            skLineSegment(sketch, "E974", {"start": v(-26.28, -7.75) * mm, "end": v(-25.76, -9.1) * mm});
            skLineSegment(sketch, "E975", {"start": v(-25.76, -9.1) * mm, "end": v(-25.7, -9.2) * mm});
            skLineSegment(sketch, "E976", {"start": v(-25.7, -9.2) * mm, "end": v(-25.46, -9.24) * mm});
            skLineSegment(sketch, "E977", {"start": v(-25.46, -9.24) * mm, "end": v(-25.23, -9.26) * mm});
            skLineSegment(sketch, "E978", {"start": v(-25.23, -9.26) * mm, "end": v(-25, -9.28) * mm});
            skLineSegment(sketch, "E979", {"start": v(-25, -9.28) * mm, "end": v(-24.79, -9.3) * mm});
            skLineSegment(sketch, "E980", {"start": v(-24.79, -9.3) * mm, "end": v(-24.58, -9.31) * mm});
            skLineSegment(sketch, "E981", {"start": v(-24.58, -9.31) * mm, "end": v(-24.37, -9.32) * mm});
            skLineSegment(sketch, "E982", {"start": v(-24.37, -9.32) * mm, "end": v(-24.17, -9.33) * mm});
            skLineSegment(sketch, "E983", {"start": v(-24.17, -9.33) * mm, "end": v(-23.98, -9.33) * mm});
            skLineSegment(sketch, "E984", {"start": v(-23.98, -9.33) * mm, "end": v(-23.8, -9.33) * mm});
            skLineSegment(sketch, "E985", {"start": v(-23.8, -9.33) * mm, "end": v(-23.61, -9.33) * mm});
            skLineSegment(sketch, "E986", {"start": v(-23.61, -9.33) * mm, "end": v(-23.44, -9.32) * mm});
            skLineSegment(sketch, "E987", {"start": v(-23.44, -9.32) * mm, "end": v(-23.27, -9.31) * mm});
            skLineSegment(sketch, "E988", {"start": v(-23.27, -9.31) * mm, "end": v(-23.11, -9.3) * mm});
            skLineSegment(sketch, "E989", {"start": v(-23.11, -9.3) * mm, "end": v(-22.96, -9.3) * mm});
            skLineSegment(sketch, "E990", {"start": v(-22.96, -9.3) * mm, "end": v(-22.81, -9.28) * mm});
            skLineSegment(sketch, "E991", {"start": v(-22.81, -9.28) * mm, "end": v(-22.67, -9.26) * mm});
            skLineSegment(sketch, "E992", {"start": v(-22.67, -9.26) * mm, "end": v(-22.54, -9.25) * mm});
            skLineSegment(sketch, "E993", {"start": v(-22.54, -9.25) * mm, "end": v(-22.42, -9.23) * mm});
            skLineSegment(sketch, "E994", {"start": v(-22.42, -9.23) * mm, "end": v(-22.3, -9.2) * mm});
            skLineSegment(sketch, "E995", {"start": v(-22.3, -9.2) * mm, "end": v(-22.18, -9.19) * mm});
            skLineSegment(sketch, "E996", {"start": v(-22.18, -9.19) * mm, "end": v(-22.08, -9.17) * mm});
            skLineSegment(sketch, "E997", {"start": v(-22.08, -9.17) * mm, "end": v(-21.98, -9.15) * mm});
            skLineSegment(sketch, "E998", {"start": v(-21.98, -9.15) * mm, "end": v(-21.89, -9.13) * mm});
            skLineSegment(sketch, "E999", {"start": v(-21.89, -9.13) * mm, "end": v(-21.8, -9.1) * mm});
            skLineSegment(sketch, "E1000", {"start": v(-21.8, -9.1) * mm, "end": v(-21.72, -9.08) * mm});
            skLineSegment(sketch, "E1001", {"start": v(-21.72, -9.08) * mm, "end": v(-21.65, -9.06) * mm});
            skLineSegment(sketch, "E1002", {"start": v(-21.65, -9.06) * mm, "end": v(-21.58, -9.04) * mm});
            skLineSegment(sketch, "E1003", {"start": v(-21.58, -9.04) * mm, "end": v(-21.52, -9.02) * mm});
            skLineSegment(sketch, "E1004", {"start": v(-21.52, -9.02) * mm, "end": v(-21.47, -9) * mm});
            skLineSegment(sketch, "E1005", {"start": v(-21.47, -9) * mm, "end": v(-21.42, -9) * mm});
            skLineSegment(sketch, "E1006", {"start": v(-21.42, -9) * mm, "end": v(-21.38, -8.98) * mm});
            skLineSegment(sketch, "E1007", {"start": v(-21.38, -8.98) * mm, "end": v(-21.35, -8.96) * mm});
            skLineSegment(sketch, "E1008", {"start": v(-21.35, -8.96) * mm, "end": v(-21.32, -8.95) * mm});
            skLineSegment(sketch, "E1009", {"start": v(-21.32, -8.95) * mm, "end": v(-21.3, -8.94) * mm});
            skLineSegment(sketch, "E1010", {"start": v(-21.3, -8.94) * mm, "end": v(-21.28, -8.94) * mm});
            skLineSegment(sketch, "E1011", {"start": v(-21.28, -8.94) * mm, "end": v(-21.27, -8.93) * mm});
            skLineSegment(sketch, "E1012", {"start": v(-21.27, -8.93) * mm, "end": v(-20.18, -8.4) * mm});
            skLineSegment(sketch, "E1013", {"start": v(-20.18, -8.4) * mm, "end": v(-18.78, -10.88) * mm});
            skLineSegment(sketch, "E1014", {"start": v(-18.78, -10.88) * mm, "end": v(-19.8, -11.54) * mm});
            skLineSegment(sketch, "E1015", {"start": v(-19.8, -11.54) * mm, "end": v(-19.81, -11.55) * mm});
            skLineSegment(sketch, "E1016", {"start": v(-19.81, -11.55) * mm, "end": v(-19.82, -11.56) * mm});
            skLineSegment(sketch, "E1017", {"start": v(-19.82, -11.56) * mm, "end": v(-19.84, -11.57) * mm});
            skLineSegment(sketch, "E1018", {"start": v(-19.84, -11.57) * mm, "end": v(-19.87, -11.6) * mm});
            skLineSegment(sketch, "E1019", {"start": v(-19.87, -11.6) * mm, "end": v(-19.9, -11.61) * mm});
            skLineSegment(sketch, "E1020", {"start": v(-19.9, -11.61) * mm, "end": v(-19.93, -11.64) * mm});
            skLineSegment(sketch, "E1021", {"start": v(-19.93, -11.64) * mm, "end": v(-19.97, -11.67) * mm});
            skLineSegment(sketch, "E1022", {"start": v(-19.97, -11.67) * mm, "end": v(-20.01, -11.7) * mm});
            skLineSegment(sketch, "E1023", {"start": v(-20.01, -11.7) * mm, "end": v(-20.06, -11.75) * mm});
            skLineSegment(sketch, "E1024", {"start": v(-20.06, -11.75) * mm, "end": v(-20.1, -11.8) * mm});
            skLineSegment(sketch, "E1025", {"start": v(-20.1, -11.8) * mm, "end": v(-20.16, -11.85) * mm});
            skLineSegment(sketch, "E1026", {"start": v(-20.16, -11.85) * mm, "end": v(-20.22, -11.9) * mm});
            skLineSegment(sketch, "E1027", {"start": v(-20.22, -11.9) * mm, "end": v(-20.28, -11.97) * mm});
            skLineSegment(sketch, "E1028", {"start": v(-20.28, -11.97) * mm, "end": v(-20.35, -12.03) * mm});
            skLineSegment(sketch, "E1029", {"start": v(-20.35, -12.03) * mm, "end": v(-20.42, -12.1) * mm});
            skLineSegment(sketch, "E1030", {"start": v(-20.42, -12.1) * mm, "end": v(-20.5, -12.19) * mm});
            skLineSegment(sketch, "E1031", {"start": v(-20.5, -12.19) * mm, "end": v(-20.57, -12.28) * mm});
            skLineSegment(sketch, "E1032", {"start": v(-20.57, -12.28) * mm, "end": v(-20.65, -12.37) * mm});
            skLineSegment(sketch, "E1033", {"start": v(-20.65, -12.37) * mm, "end": v(-20.73, -12.47) * mm});
            skLineSegment(sketch, "E1034", {"start": v(-20.73, -12.47) * mm, "end": v(-20.81, -12.57) * mm});
            skLineSegment(sketch, "E1035", {"start": v(-20.81, -12.57) * mm, "end": v(-20.9, -12.68) * mm});
            skLineSegment(sketch, "E1036", {"start": v(-20.9, -12.68) * mm, "end": v(-20.98, -12.8) * mm});
            skLineSegment(sketch, "E1037", {"start": v(-20.98, -12.8) * mm, "end": v(-21.07, -12.92) * mm});
            skLineSegment(sketch, "E1038", {"start": v(-21.07, -12.92) * mm, "end": v(-21.17, -13.06) * mm});
            skLineSegment(sketch, "E1039", {"start": v(-21.17, -13.06) * mm, "end": v(-21.26, -13.2) * mm});
            skLineSegment(sketch, "E1040", {"start": v(-21.26, -13.2) * mm, "end": v(-21.35, -13.34) * mm});
            skLineSegment(sketch, "E1041", {"start": v(-21.35, -13.34) * mm, "end": v(-21.45, -13.5) * mm});
            skLineSegment(sketch, "E1042", {"start": v(-21.45, -13.5) * mm, "end": v(-21.55, -13.65) * mm});
            skLineSegment(sketch, "E1043", {"start": v(-21.55, -13.65) * mm, "end": v(-21.64, -13.82) * mm});
            skLineSegment(sketch, "E1044", {"start": v(-21.64, -13.82) * mm, "end": v(-21.74, -13.99) * mm});
            skLineSegment(sketch, "E1045", {"start": v(-21.74, -13.99) * mm, "end": v(-21.84, -14.17) * mm});
            skLineSegment(sketch, "E1046", {"start": v(-21.84, -14.17) * mm, "end": v(-21.94, -14.36) * mm});
            skLineSegment(sketch, "E1047", {"start": v(-21.94, -14.36) * mm, "end": v(-22.04, -14.55) * mm});
            skLineSegment(sketch, "E1048", {"start": v(-22.04, -14.55) * mm, "end": v(-22.13, -14.76) * mm});
            skLineSegment(sketch, "E1049", {"start": v(-22.13, -14.76) * mm, "end": v(-22.23, -14.97) * mm});
            skLineSegment(sketch, "E1050", {"start": v(-22.23, -14.97) * mm, "end": v(-22.33, -15.18) * mm});
            skLineSegment(sketch, "E1051", {"start": v(-22.33, -15.18) * mm, "end": v(-22.27, -15.3) * mm});
            skLineSegment(sketch, "E1052", {"start": v(-22.27, -15.3) * mm, "end": v(-21.39, -16.43) * mm});
            skLineSegment(sketch, "E1053", {"start": v(-21.39, -16.43) * mm, "end": v(-21.3, -16.52) * mm});
            skLineSegment(sketch, "E1054", {"start": v(-21.3, -16.52) * mm, "end": v(-21.06, -16.48) * mm});
            skLineSegment(sketch, "E1055", {"start": v(-21.06, -16.48) * mm, "end": v(-20.83, -16.44) * mm});
            skLineSegment(sketch, "E1056", {"start": v(-20.83, -16.44) * mm, "end": v(-20.61, -16.4) * mm});
            skLineSegment(sketch, "E1057", {"start": v(-20.61, -16.4) * mm, "end": v(-20.4, -16.36) * mm});
            skLineSegment(sketch, "E1058", {"start": v(-20.4, -16.36) * mm, "end": v(-20.2, -16.3) * mm});
            skLineSegment(sketch, "E1059", {"start": v(-20.2, -16.3) * mm, "end": v(-20, -16.26) * mm});
            skLineSegment(sketch, "E1060", {"start": v(-20, -16.26) * mm, "end": v(-19.8, -16.2) * mm});
            skLineSegment(sketch, "E1061", {"start": v(-19.8, -16.2) * mm, "end": v(-19.61, -16.16) * mm});
            skLineSegment(sketch, "E1062", {"start": v(-19.61, -16.16) * mm, "end": v(-19.44, -16.1) * mm});
            skLineSegment(sketch, "E1063", {"start": v(-19.44, -16.1) * mm, "end": v(-19.26, -16.05) * mm});
            skLineSegment(sketch, "E1064", {"start": v(-19.26, -16.05) * mm, "end": v(-19.1, -16) * mm});
            skLineSegment(sketch, "E1065", {"start": v(-19.1, -16) * mm, "end": v(-18.94, -15.94) * mm});
            skLineSegment(sketch, "E1066", {"start": v(-18.94, -15.94) * mm, "end": v(-18.8, -15.89) * mm});
            skLineSegment(sketch, "E1067", {"start": v(-18.8, -15.89) * mm, "end": v(-18.65, -15.83) * mm});
            skLineSegment(sketch, "E1068", {"start": v(-18.65, -15.83) * mm, "end": v(-18.51, -15.78) * mm});
            skLineSegment(sketch, "E1069", {"start": v(-18.51, -15.78) * mm, "end": v(-18.38, -15.72) * mm});
            skLineSegment(sketch, "E1070", {"start": v(-18.38, -15.72) * mm, "end": v(-18.26, -15.67) * mm});
            skLineSegment(sketch, "E1071", {"start": v(-18.26, -15.67) * mm, "end": v(-18.14, -15.62) * mm});
            skLineSegment(sketch, "E1072", {"start": v(-18.14, -15.62) * mm, "end": v(-18.04, -15.56) * mm});
            skLineSegment(sketch, "E1073", {"start": v(-18.04, -15.56) * mm, "end": v(-17.93, -15.51) * mm});
            skLineSegment(sketch, "E1074", {"start": v(-17.93, -15.51) * mm, "end": v(-17.84, -15.46) * mm});
            skLineSegment(sketch, "E1075", {"start": v(-17.84, -15.46) * mm, "end": v(-17.75, -15.42) * mm});
            skLineSegment(sketch, "E1076", {"start": v(-17.75, -15.42) * mm, "end": v(-17.67, -15.37) * mm});
            skLineSegment(sketch, "E1077", {"start": v(-17.67, -15.37) * mm, "end": v(-17.59, -15.33) * mm});
            skLineSegment(sketch, "E1078", {"start": v(-17.59, -15.33) * mm, "end": v(-17.52, -15.28) * mm});
            skLineSegment(sketch, "E1079", {"start": v(-17.52, -15.28) * mm, "end": v(-17.45, -15.24) * mm});
            skLineSegment(sketch, "E1080", {"start": v(-17.45, -15.24) * mm, "end": v(-17.4, -15.2) * mm});
            skLineSegment(sketch, "E1081", {"start": v(-17.4, -15.2) * mm, "end": v(-17.34, -15.17) * mm});
            skLineSegment(sketch, "E1082", {"start": v(-17.34, -15.17) * mm, "end": v(-17.3, -15.14) * mm});
            skLineSegment(sketch, "E1083", {"start": v(-17.3, -15.14) * mm, "end": v(-17.26, -15.11) * mm});
            skLineSegment(sketch, "E1084", {"start": v(-17.26, -15.11) * mm, "end": v(-17.22, -15.09) * mm});
            skLineSegment(sketch, "E1085", {"start": v(-17.22, -15.09) * mm, "end": v(-17.2, -15.06) * mm});
            skLineSegment(sketch, "E1086", {"start": v(-17.2, -15.06) * mm, "end": v(-17.17, -15.04) * mm});
            skLineSegment(sketch, "E1087", {"start": v(-17.17, -15.04) * mm, "end": v(-17.15, -15.03) * mm});
            skLineSegment(sketch, "E1088", {"start": v(-17.15, -15.03) * mm, "end": v(-17.14, -15.02) * mm});
            skLineSegment(sketch, "E1089", {"start": v(-17.14, -15.02) * mm, "end": v(-17.13, -15.01) * mm});
            skLineSegment(sketch, "E1090", {"start": v(-17.13, -15.01) * mm, "end": v(-16.23, -14.19) * mm});
            skLineSegment(sketch, "E1091", {"start": v(-16.23, -14.19) * mm, "end": v(-14.19, -16.18) * mm});
            skLineSegment(sketch, "E1092", {"start": v(-14.19, -16.18) * mm, "end": v(-14.98, -17.1) * mm});
            skLineSegment(sketch, "E1093", {"start": v(-14.98, -17.1) * mm, "end": v(-15, -17.11) * mm});
            skLineSegment(sketch, "E1094", {"start": v(-15, -17.11) * mm, "end": v(-15, -17.12) * mm});
            skLineSegment(sketch, "E1095", {"start": v(-15, -17.12) * mm, "end": v(-15.02, -17.14) * mm});
            skLineSegment(sketch, "E1096", {"start": v(-15.02, -17.14) * mm, "end": v(-15.03, -17.17) * mm});
            skLineSegment(sketch, "E1097", {"start": v(-15.03, -17.17) * mm, "end": v(-15.06, -17.2) * mm});
            skLineSegment(sketch, "E1098", {"start": v(-15.06, -17.2) * mm, "end": v(-15.08, -17.23) * mm});
            skLineSegment(sketch, "E1099", {"start": v(-15.08, -17.23) * mm, "end": v(-15.1, -17.27) * mm});
            skLineSegment(sketch, "E1100", {"start": v(-15.1, -17.27) * mm, "end": v(-15.14, -17.32) * mm});
            skLineSegment(sketch, "E1101", {"start": v(-15.14, -17.32) * mm, "end": v(-15.17, -17.37) * mm});
            skLineSegment(sketch, "E1102", {"start": v(-15.17, -17.37) * mm, "end": v(-15.2, -17.43) * mm});
            skLineSegment(sketch, "E1103", {"start": v(-15.2, -17.43) * mm, "end": v(-15.25, -17.5) * mm});
            skLineSegment(sketch, "E1104", {"start": v(-15.25, -17.5) * mm, "end": v(-15.29, -17.57) * mm});
            skLineSegment(sketch, "E1105", {"start": v(-15.29, -17.57) * mm, "end": v(-15.33, -17.64) * mm});
            skLineSegment(sketch, "E1106", {"start": v(-15.33, -17.64) * mm, "end": v(-15.37, -17.73) * mm});
            skLineSegment(sketch, "E1107", {"start": v(-15.37, -17.73) * mm, "end": v(-15.42, -17.82) * mm});
            skLineSegment(sketch, "E1108", {"start": v(-15.42, -17.82) * mm, "end": v(-15.46, -17.92) * mm});
            skLineSegment(sketch, "E1109", {"start": v(-15.46, -17.92) * mm, "end": v(-15.51, -18.02) * mm});
            skLineSegment(sketch, "E1110", {"start": v(-15.51, -18.02) * mm, "end": v(-15.56, -18.13) * mm});
            skLineSegment(sketch, "E1111", {"start": v(-15.56, -18.13) * mm, "end": v(-15.61, -18.25) * mm});
            skLineSegment(sketch, "E1112", {"start": v(-15.61, -18.25) * mm, "end": v(-15.66, -18.37) * mm});
            skLineSegment(sketch, "E1113", {"start": v(-15.66, -18.37) * mm, "end": v(-15.71, -18.5) * mm});
            skLineSegment(sketch, "E1114", {"start": v(-15.71, -18.5) * mm, "end": v(-15.76, -18.64) * mm});
            skLineSegment(sketch, "E1115", {"start": v(-15.76, -18.64) * mm, "end": v(-15.82, -18.79) * mm});
            skLineSegment(sketch, "E1116", {"start": v(-15.82, -18.79) * mm, "end": v(-15.87, -18.94) * mm});
            skLineSegment(sketch, "E1117", {"start": v(-15.87, -18.94) * mm, "end": v(-15.92, -19.1) * mm});
            skLineSegment(sketch, "E1118", {"start": v(-15.92, -19.1) * mm, "end": v(-15.97, -19.26) * mm});
            skLineSegment(sketch, "E1119", {"start": v(-15.97, -19.26) * mm, "end": v(-16.02, -19.44) * mm});
            skLineSegment(sketch, "E1120", {"start": v(-16.02, -19.44) * mm, "end": v(-16.06, -19.62) * mm});
            skLineSegment(sketch, "E1121", {"start": v(-16.06, -19.62) * mm, "end": v(-16.11, -19.8) * mm});
            skLineSegment(sketch, "E1122", {"start": v(-16.11, -19.8) * mm, "end": v(-16.16, -20) * mm});
            skLineSegment(sketch, "E1123", {"start": v(-16.16, -20) * mm, "end": v(-16.2, -20.2) * mm});
            skLineSegment(sketch, "E1124", {"start": v(-16.2, -20.2) * mm, "end": v(-16.24, -20.4) * mm});
            skLineSegment(sketch, "E1125", {"start": v(-16.24, -20.4) * mm, "end": v(-16.28, -20.62) * mm});
            skLineSegment(sketch, "E1126", {"start": v(-16.28, -20.62) * mm, "end": v(-16.32, -20.84) * mm});
            skLineSegment(sketch, "E1127", {"start": v(-16.32, -20.84) * mm, "end": v(-16.35, -21.07) * mm});
            skLineSegment(sketch, "E1128", {"start": v(-16.35, -21.07) * mm, "end": v(-16.38, -21.3) * mm});
            skLineSegment(sketch, "E1129", {"start": v(-16.38, -21.3) * mm, "end": v(-16.3, -21.4) * mm});
            skLineSegment(sketch, "E1130", {"start": v(-16.3, -21.4) * mm, "end": v(-15.13, -22.24) * mm});
            skLineSegment(sketch, "E1131", {"start": v(-15.13, -22.24) * mm, "end": v(-15.02, -22.3) * mm});
            skLineSegment(sketch, "E1132", {"start": v(-15.02, -22.3) * mm, "end": v(-14.8, -22.2) * mm});
            skLineSegment(sketch, "E1133", {"start": v(-14.8, -22.2) * mm, "end": v(-14.6, -22.1) * mm});
            skLineSegment(sketch, "E1134", {"start": v(-14.6, -22.1) * mm, "end": v(-14.4, -22) * mm});
            skLineSegment(sketch, "E1135", {"start": v(-14.4, -22) * mm, "end": v(-14.2, -21.89) * mm});
            skLineSegment(sketch, "E1136", {"start": v(-14.2, -21.89) * mm, "end": v(-14.02, -21.79) * mm});
            skLineSegment(sketch, "E1137", {"start": v(-14.02, -21.79) * mm, "end": v(-13.84, -21.68) * mm});
            skLineSegment(sketch, "E1138", {"start": v(-13.84, -21.68) * mm, "end": v(-13.67, -21.58) * mm});
            skLineSegment(sketch, "E1139", {"start": v(-13.67, -21.58) * mm, "end": v(-13.5, -21.48) * mm});
            skLineSegment(sketch, "E1140", {"start": v(-13.5, -21.48) * mm, "end": v(-13.35, -21.38) * mm});
            skLineSegment(sketch, "E1141", {"start": v(-13.35, -21.38) * mm, "end": v(-13.2, -21.28) * mm});
            skLineSegment(sketch, "E1142", {"start": v(-13.2, -21.28) * mm, "end": v(-13.06, -21.18) * mm});
            skLineSegment(sketch, "E1143", {"start": v(-13.06, -21.18) * mm, "end": v(-12.92, -21.08) * mm});
            skLineSegment(sketch, "E1144", {"start": v(-12.92, -21.08) * mm, "end": v(-12.8, -20.99) * mm});
            skLineSegment(sketch, "E1145", {"start": v(-12.8, -20.99) * mm, "end": v(-12.67, -20.9) * mm});
            skLineSegment(sketch, "E1146", {"start": v(-12.67, -20.9) * mm, "end": v(-12.55, -20.8) * mm});
            skLineSegment(sketch, "E1147", {"start": v(-12.55, -20.8) * mm, "end": v(-12.45, -20.71) * mm});
            skLineSegment(sketch, "E1148", {"start": v(-12.45, -20.71) * mm, "end": v(-12.34, -20.63) * mm});
            skLineSegment(sketch, "E1149", {"start": v(-12.34, -20.63) * mm, "end": v(-12.25, -20.54) * mm});
            skLineSegment(sketch, "E1150", {"start": v(-12.25, -20.54) * mm, "end": v(-12.16, -20.46) * mm});
            skLineSegment(sketch, "E1151", {"start": v(-12.16, -20.46) * mm, "end": v(-12.07, -20.39) * mm});
            skLineSegment(sketch, "E1152", {"start": v(-12.07, -20.39) * mm, "end": v(-12, -20.31) * mm});
            skLineSegment(sketch, "E1153", {"start": v(-12, -20.31) * mm, "end": v(-11.92, -20.24) * mm});
            skLineSegment(sketch, "E1154", {"start": v(-11.92, -20.24) * mm, "end": v(-11.86, -20.17) * mm});
            skLineSegment(sketch, "E1155", {"start": v(-11.86, -20.17) * mm, "end": v(-11.8, -20.1) * mm});
            skLineSegment(sketch, "E1156", {"start": v(-11.8, -20.1) * mm, "end": v(-11.74, -20.05) * mm});
            skLineSegment(sketch, "E1157", {"start": v(-11.74, -20.05) * mm, "end": v(-11.69, -20) * mm});
            skLineSegment(sketch, "E1158", {"start": v(-11.69, -20) * mm, "end": v(-11.64, -19.94) * mm});
            skLineSegment(sketch, "E1159", {"start": v(-11.64, -19.94) * mm, "end": v(-11.6, -19.9) * mm});
            skLineSegment(sketch, "E1160", {"start": v(-11.6, -19.9) * mm, "end": v(-11.57, -19.85) * mm});
            skLineSegment(sketch, "E1161", {"start": v(-11.57, -19.85) * mm, "end": v(-11.54, -19.8) * mm});
            skLineSegment(sketch, "E1162", {"start": v(-11.54, -19.8) * mm, "end": v(-11.51, -19.77) * mm});
            skLineSegment(sketch, "E1163", {"start": v(-11.51, -19.77) * mm, "end": v(-11.5, -19.75) * mm});
            skLineSegment(sketch, "E1164", {"start": v(-11.5, -19.75) * mm, "end": v(-11.47, -19.72) * mm});
            skLineSegment(sketch, "E1165", {"start": v(-11.47, -19.72) * mm, "end": v(-11.46, -19.7) * mm});
            skLineSegment(sketch, "E1166", {"start": v(-11.46, -19.7) * mm, "end": v(-11.45, -19.69) * mm});
            skLineSegment(sketch, "E1167", {"start": v(-11.45, -19.69) * mm, "end": v(-11.45, -19.68) * mm});
            skLineSegment(sketch, "E1168", {"start": v(-11.45, -19.68) * mm, "end": v(-10.81, -18.63) * mm});
            skLineSegment(sketch, "E1169", {"start": v(-10.81, -18.63) * mm, "end": v(-8.29, -19.97) * mm});
            skLineSegment(sketch, "E1170", {"start": v(-8.29, -19.97) * mm, "end": v(-8.8, -21.08) * mm});
            skLineSegment(sketch, "E1171", {"start": v(-8.8, -21.08) * mm, "end": v(-8.8, -21.09) * mm});
            skLineSegment(sketch, "E1172", {"start": v(-8.8, -21.09) * mm, "end": v(-8.8, -21.1) * mm});
            skLineSegment(sketch, "E1173", {"start": v(-8.8, -21.1) * mm, "end": v(-8.82, -21.13) * mm});
            skLineSegment(sketch, "E1174", {"start": v(-8.82, -21.13) * mm, "end": v(-8.83, -21.15) * mm});
            skLineSegment(sketch, "E1175", {"start": v(-8.83, -21.15) * mm, "end": v(-8.84, -21.19) * mm});
            skLineSegment(sketch, "E1176", {"start": v(-8.84, -21.19) * mm, "end": v(-8.85, -21.23) * mm});
            skLineSegment(sketch, "E1177", {"start": v(-8.85, -21.23) * mm, "end": v(-8.87, -21.28) * mm});
            skLineSegment(sketch, "E1178", {"start": v(-8.87, -21.28) * mm, "end": v(-8.88, -21.33) * mm});
            skLineSegment(sketch, "E1179", {"start": v(-8.88, -21.33) * mm, "end": v(-8.9, -21.4) * mm});
            skLineSegment(sketch, "E1180", {"start": v(-8.9, -21.4) * mm, "end": v(-8.92, -21.46) * mm});
            skLineSegment(sketch, "E1181", {"start": v(-8.92, -21.46) * mm, "end": v(-8.94, -21.53) * mm});
            skLineSegment(sketch, "E1182", {"start": v(-8.94, -21.53) * mm, "end": v(-8.95, -21.61) * mm});
            skLineSegment(sketch, "E1183", {"start": v(-8.95, -21.61) * mm, "end": v(-8.97, -21.7) * mm});
            skLineSegment(sketch, "E1184", {"start": v(-8.97, -21.7) * mm, "end": v(-9, -21.79) * mm});
            skLineSegment(sketch, "E1185", {"start": v(-9, -21.79) * mm, "end": v(-9, -21.89) * mm});
            skLineSegment(sketch, "E1186", {"start": v(-9, -21.89) * mm, "end": v(-9.03, -22) * mm});
            skLineSegment(sketch, "E1187", {"start": v(-9.03, -22) * mm, "end": v(-9.04, -22.1) * mm});
            skLineSegment(sketch, "E1188", {"start": v(-9.04, -22.1) * mm, "end": v(-9.06, -22.23) * mm});
            skLineSegment(sketch, "E1189", {"start": v(-9.06, -22.23) * mm, "end": v(-9.08, -22.36) * mm});
            skLineSegment(sketch, "E1190", {"start": v(-9.08, -22.36) * mm, "end": v(-9.09, -22.49) * mm});
            skLineSegment(sketch, "E1191", {"start": v(-9.09, -22.49) * mm, "end": v(-9.1, -22.63) * mm});
            skLineSegment(sketch, "E1192", {"start": v(-9.1, -22.63) * mm, "end": v(-9.11, -22.78) * mm});
            skLineSegment(sketch, "E1193", {"start": v(-9.11, -22.78) * mm, "end": v(-9.12, -22.93) * mm});
            skLineSegment(sketch, "E1194", {"start": v(-9.12, -22.93) * mm, "end": v(-9.13, -23.09) * mm});
            skLineSegment(sketch, "E1195", {"start": v(-9.13, -23.09) * mm, "end": v(-9.13, -23.26) * mm});
            skLineSegment(sketch, "E1196", {"start": v(-9.13, -23.26) * mm, "end": v(-9.13, -23.43) * mm});
            skLineSegment(sketch, "E1197", {"start": v(-9.13, -23.43) * mm, "end": v(-9.13, -23.6) * mm});
            skLineSegment(sketch, "E1198", {"start": v(-9.13, -23.6) * mm, "end": v(-9.12, -23.8) * mm});
            skLineSegment(sketch, "E1199", {"start": v(-9.12, -23.8) * mm, "end": v(-9.12, -23.99) * mm});
            skLineSegment(sketch, "E1200", {"start": v(-9.12, -23.99) * mm, "end": v(-9.1, -24.19) * mm});
            skLineSegment(sketch, "E1201", {"start": v(-9.1, -24.19) * mm, "end": v(-9.09, -24.4) * mm});
            skLineSegment(sketch, "E1202", {"start": v(-9.09, -24.4) * mm, "end": v(-9.07, -24.6) * mm});
            skLineSegment(sketch, "E1203", {"start": v(-9.07, -24.6) * mm, "end": v(-9.05, -24.82) * mm});
            skLineSegment(sketch, "E1204", {"start": v(-9.05, -24.82) * mm, "end": v(-9.02, -25.04) * mm});
            skLineSegment(sketch, "E1205", {"start": v(-9.02, -25.04) * mm, "end": v(-8.99, -25.27) * mm});
            skLineSegment(sketch, "E1206", {"start": v(-8.99, -25.27) * mm, "end": v(-8.95, -25.5) * mm});
            skLineSegment(sketch, "E1207", {"start": v(-8.95, -25.5) * mm, "end": v(-8.84, -25.57) * mm});
            skLineSegment(sketch, "E1208", {"start": v(-8.84, -25.57) * mm, "end": v(-7.49, -26.05) * mm});
            skLineSegment(sketch, "E1209", {"start": v(-7.49, -26.05) * mm, "end": v(-7.36, -26.08) * mm});
            skLineSegment(sketch, "E1210", {"start": v(-7.36, -26.08) * mm, "end": v(-7.18, -25.92) * mm});
            skLineSegment(sketch, "E1211", {"start": v(-7.18, -25.92) * mm, "end": v(-7.01, -25.76) * mm});
            skLineSegment(sketch, "E1212", {"start": v(-7.01, -25.76) * mm, "end": v(-6.85, -25.6) * mm});
            skLineSegment(sketch, "E1213", {"start": v(-6.85, -25.6) * mm, "end": v(-6.7, -25.45) * mm});
            skLineSegment(sketch, "E1214", {"start": v(-6.7, -25.45) * mm, "end": v(-6.55, -25.3) * mm});
            skLineSegment(sketch, "E1215", {"start": v(-6.55, -25.3) * mm, "end": v(-6.4, -25.15) * mm});
            skLineSegment(sketch, "E1216", {"start": v(-6.4, -25.15) * mm, "end": v(-6.27, -25) * mm});
            skLineSegment(sketch, "E1217", {"start": v(-6.27, -25) * mm, "end": v(-6.14, -24.86) * mm});
            skLineSegment(sketch, "E1218", {"start": v(-6.14, -24.86) * mm, "end": v(-6.02, -24.72) * mm});
            skLineSegment(sketch, "E1219", {"start": v(-6.02, -24.72) * mm, "end": v(-5.9, -24.58) * mm});
            skLineSegment(sketch, "E1220", {"start": v(-5.9, -24.58) * mm, "end": v(-5.8, -24.45) * mm});
            skLineSegment(sketch, "E1221", {"start": v(-5.8, -24.45) * mm, "end": v(-5.7, -24.32) * mm});
            skLineSegment(sketch, "E1222", {"start": v(-5.7, -24.32) * mm, "end": v(-5.6, -24.19) * mm});
            skLineSegment(sketch, "E1223", {"start": v(-5.6, -24.19) * mm, "end": v(-5.5, -24.07) * mm});
            skLineSegment(sketch, "E1224", {"start": v(-5.5, -24.07) * mm, "end": v(-5.42, -23.95) * mm});
            skLineSegment(sketch, "E1225", {"start": v(-5.42, -23.95) * mm, "end": v(-5.34, -23.83) * mm});
            skLineSegment(sketch, "E1226", {"start": v(-5.34, -23.83) * mm, "end": v(-5.27, -23.72) * mm});
            skLineSegment(sketch, "E1227", {"start": v(-5.27, -23.72) * mm, "end": v(-5.2, -23.61) * mm});
            skLineSegment(sketch, "E1228", {"start": v(-5.2, -23.61) * mm, "end": v(-5.14, -23.5) * mm});
            skLineSegment(sketch, "E1229", {"start": v(-5.14, -23.5) * mm, "end": v(-5.08, -23.4) * mm});
            skLineSegment(sketch, "E1230", {"start": v(-5.08, -23.4) * mm, "end": v(-5.02, -23.32) * mm});
            skLineSegment(sketch, "E1231", {"start": v(-5.02, -23.32) * mm, "end": v(-4.97, -23.23) * mm});
            skLineSegment(sketch, "E1232", {"start": v(-4.97, -23.23) * mm, "end": v(-4.93, -23.14) * mm});
            skLineSegment(sketch, "E1233", {"start": v(-4.93, -23.14) * mm, "end": v(-4.89, -23.06) * mm});
            skLineSegment(sketch, "E1234", {"start": v(-4.89, -23.06) * mm, "end": v(-4.85, -23) * mm});
            skLineSegment(sketch, "E1235", {"start": v(-4.85, -23) * mm, "end": v(-4.82, -22.92) * mm});
            skLineSegment(sketch, "E1236", {"start": v(-4.82, -22.92) * mm, "end": v(-4.8, -22.86) * mm});
            skLineSegment(sketch, "E1237", {"start": v(-4.8, -22.86) * mm, "end": v(-4.77, -22.8) * mm});
            skLineSegment(sketch, "E1238", {"start": v(-4.77, -22.8) * mm, "end": v(-4.75, -22.75) * mm});
            skLineSegment(sketch, "E1239", {"start": v(-4.75, -22.75) * mm, "end": v(-4.73, -22.7) * mm});
            skLineSegment(sketch, "E1240", {"start": v(-4.73, -22.7) * mm, "end": v(-4.71, -22.67) * mm});
            skLineSegment(sketch, "E1241", {"start": v(-4.71, -22.67) * mm, "end": v(-4.7, -22.63) * mm});
            skLineSegment(sketch, "E1242", {"start": v(-4.7, -22.63) * mm, "end": v(-4.69, -22.6) * mm});
            skLineSegment(sketch, "E1243", {"start": v(-4.69, -22.6) * mm, "end": v(-4.68, -22.58) * mm});
            skLineSegment(sketch, "E1244", {"start": v(-4.68, -22.58) * mm, "end": v(-4.68, -22.56) * mm});
            skLineSegment(sketch, "E1245", {"start": v(-4.68, -22.56) * mm, "end": v(-4.67, -22.55) * mm});
            skLineSegment(sketch, "E1246", {"start": v(-4.67, -22.55) * mm, "end": v(-4.36, -21.37) * mm});
            skLineSegment(sketch, "E1247", {"start": v(-4.36, -21.37) * mm, "end": v(-1.56, -21.94) * mm});
            skLineSegment(sketch, "E1248", {"start": v(-1.56, -21.94) * mm, "end": v(-1.74, -23.15) * mm});
            skLineSegment(sketch, "E1249", {"start": v(-1.74, -23.15) * mm, "end": v(-1.74, -23.16) * mm});
            skLineSegment(sketch, "E1250", {"start": v(-1.74, -23.16) * mm, "end": v(-1.74, -23.18) * mm});
            skLineSegment(sketch, "E1251", {"start": v(-1.74, -23.18) * mm, "end": v(-1.74, -23.2) * mm});
            skLineSegment(sketch, "E1252", {"start": v(-1.74, -23.2) * mm, "end": v(-1.74, -23.23) * mm});
            skLineSegment(sketch, "E1253", {"start": v(-1.74, -23.23) * mm, "end": v(-1.75, -23.27) * mm});
            skLineSegment(sketch, "E1254", {"start": v(-1.75, -23.27) * mm, "end": v(-1.75, -23.31) * mm});
            skLineSegment(sketch, "E1255", {"start": v(-1.75, -23.31) * mm, "end": v(-1.75, -23.36) * mm});
            skLineSegment(sketch, "E1256", {"start": v(-1.75, -23.36) * mm, "end": v(-1.75, -23.42) * mm});
            skLineSegment(sketch, "E1257", {"start": v(-1.75, -23.42) * mm, "end": v(-1.75, -23.48) * mm});
            skLineSegment(sketch, "E1258", {"start": v(-1.75, -23.48) * mm, "end": v(-1.75, -23.55) * mm});
            skLineSegment(sketch, "E1259", {"start": v(-1.75, -23.55) * mm, "end": v(-1.74, -23.62) * mm});
            skLineSegment(sketch, "E1260", {"start": v(-1.74, -23.62) * mm, "end": v(-1.74, -23.7) * mm});
            skLineSegment(sketch, "E1261", {"start": v(-1.74, -23.7) * mm, "end": v(-1.73, -23.8) * mm});
            skLineSegment(sketch, "E1262", {"start": v(-1.73, -23.8) * mm, "end": v(-1.72, -23.89) * mm});
            skLineSegment(sketch, "E1263", {"start": v(-1.72, -23.89) * mm, "end": v(-1.71, -23.99) * mm});
            skLineSegment(sketch, "E1264", {"start": v(-1.71, -23.99) * mm, "end": v(-1.7, -24.1) * mm});
            skLineSegment(sketch, "E1265", {"start": v(-1.7, -24.1) * mm, "end": v(-1.69, -24.21) * mm});
            skLineSegment(sketch, "E1266", {"start": v(-1.69, -24.21) * mm, "end": v(-1.67, -24.33) * mm});
            skLineSegment(sketch, "E1267", {"start": v(-1.67, -24.33) * mm, "end": v(-1.65, -24.46) * mm});
            skLineSegment(sketch, "E1268", {"start": v(-1.65, -24.46) * mm, "end": v(-1.62, -24.59) * mm});
            skLineSegment(sketch, "E1269", {"start": v(-1.62, -24.59) * mm, "end": v(-1.6, -24.72) * mm});
            skLineSegment(sketch, "E1270", {"start": v(-1.6, -24.72) * mm, "end": v(-1.56, -24.87) * mm});
            skLineSegment(sketch, "E1271", {"start": v(-1.56, -24.87) * mm, "end": v(-1.53, -25.02) * mm});
            skLineSegment(sketch, "E1272", {"start": v(-1.53, -25.02) * mm, "end": v(-1.49, -25.17) * mm});
            skLineSegment(sketch, "E1273", {"start": v(-1.49, -25.17) * mm, "end": v(-1.44, -25.33) * mm});
            skLineSegment(sketch, "E1274", {"start": v(-1.44, -25.33) * mm, "end": v(-1.4, -25.5) * mm});
            skLineSegment(sketch, "E1275", {"start": v(-1.4, -25.5) * mm, "end": v(-1.34, -25.67) * mm});
            skLineSegment(sketch, "E1276", {"start": v(-1.34, -25.67) * mm, "end": v(-1.29, -25.85) * mm});
            skLineSegment(sketch, "E1277", {"start": v(-1.29, -25.85) * mm, "end": v(-1.23, -26.03) * mm});
            skLineSegment(sketch, "E1278", {"start": v(-1.23, -26.03) * mm, "end": v(-1.16, -26.22) * mm});
            skLineSegment(sketch, "E1279", {"start": v(-1.16, -26.22) * mm, "end": v(-1.09, -26.41) * mm});
            skLineSegment(sketch, "E1280", {"start": v(-1.09, -26.41) * mm, "end": v(-1, -26.6) * mm});
            skLineSegment(sketch, "E1281", {"start": v(-1, -26.6) * mm, "end": v(-0.93, -26.81) * mm});
            skLineSegment(sketch, "E1282", {"start": v(-0.93, -26.81) * mm, "end": v(-0.84, -27.02) * mm});
            skLineSegment(sketch, "E1283", {"start": v(-0.84, -27.02) * mm, "end": v(-0.74, -27.23) * mm});
            skLineSegment(sketch, "E1284", {"start": v(-0.74, -27.23) * mm, "end": v(-0.64, -27.44) * mm});
            skLineSegment(sketch, "E1285", {"start": v(-0.64, -27.44) * mm, "end": v(-0.52, -27.47) * mm});
            skLineSegment(sketch, "E1286", {"start": v(-0.52, -27.47) * mm, "end": v(0.92, -27.55) * mm});
            skLineSegment(sketch, "E1287", {"start": v(0.92, -27.55) * mm, "end": v(1.05, -27.54) * mm});
            skLineSegment(sketch, "E1288", {"start": v(1.05, -27.54) * mm, "end": v(1.17, -27.34) * mm});
            skLineSegment(sketch, "E1289", {"start": v(1.17, -27.34) * mm, "end": v(1.3, -27.14) * mm});
            skLineSegment(sketch, "E1290", {"start": v(1.3, -27.14) * mm, "end": v(1.4, -26.95) * mm});
            skLineSegment(sketch, "E1291", {"start": v(1.4, -26.95) * mm, "end": v(1.5, -26.76) * mm});
            skLineSegment(sketch, "E1292", {"start": v(1.5, -26.76) * mm, "end": v(1.6, -26.57) * mm});
            skLineSegment(sketch, "E1293", {"start": v(1.6, -26.57) * mm, "end": v(1.7, -26.39) * mm});
            skLineSegment(sketch, "E1294", {"start": v(1.7, -26.39) * mm, "end": v(1.8, -26.2) * mm});
            skLineSegment(sketch, "E1295", {"start": v(1.8, -26.2) * mm, "end": v(1.87, -26.03) * mm});
            skLineSegment(sketch, "E1296", {"start": v(1.87, -26.03) * mm, "end": v(1.95, -25.86) * mm});
            skLineSegment(sketch, "E1297", {"start": v(1.95, -25.86) * mm, "end": v(2.02, -25.7) * mm});
            skLineSegment(sketch, "E1298", {"start": v(2.02, -25.7) * mm, "end": v(2.09, -25.54) * mm});
            skLineSegment(sketch, "E1299", {"start": v(2.09, -25.54) * mm, "end": v(2.15, -25.38) * mm});
            skLineSegment(sketch, "E1300", {"start": v(2.15, -25.38) * mm, "end": v(2.2, -25.23) * mm});
            skLineSegment(sketch, "E1301", {"start": v(2.2, -25.23) * mm, "end": v(2.26, -25.1) * mm});
            skLineSegment(sketch, "E1302", {"start": v(2.26, -25.1) * mm, "end": v(2.3, -24.95) * mm});
            skLineSegment(sketch, "E1303", {"start": v(2.3, -24.95) * mm, "end": v(2.35, -24.82) * mm});
            skLineSegment(sketch, "E1304", {"start": v(2.35, -24.82) * mm, "end": v(2.4, -24.69) * mm});
            skLineSegment(sketch, "E1305", {"start": v(2.4, -24.69) * mm, "end": v(2.43, -24.57) * mm});
            skLineSegment(sketch, "E1306", {"start": v(2.43, -24.57) * mm, "end": v(2.46, -24.45) * mm});
            skLineSegment(sketch, "E1307", {"start": v(2.46, -24.45) * mm, "end": v(2.49, -24.34) * mm});
            skLineSegment(sketch, "E1308", {"start": v(2.49, -24.34) * mm, "end": v(2.51, -24.24) * mm});
            skLineSegment(sketch, "E1309", {"start": v(2.51, -24.24) * mm, "end": v(2.53, -24.14) * mm});
            skLineSegment(sketch, "E1310", {"start": v(2.53, -24.14) * mm, "end": v(2.55, -24.04) * mm});
            skLineSegment(sketch, "E1311", {"start": v(2.55, -24.04) * mm, "end": v(2.57, -23.96) * mm});
            skLineSegment(sketch, "E1312", {"start": v(2.57, -23.96) * mm, "end": v(2.58, -23.88) * mm});
            skLineSegment(sketch, "E1313", {"start": v(2.58, -23.88) * mm, "end": v(2.6, -23.8) * mm});
            skLineSegment(sketch, "E1314", {"start": v(2.6, -23.8) * mm, "end": v(2.6, -23.73) * mm});
            skLineSegment(sketch, "E1315", {"start": v(2.6, -23.73) * mm, "end": v(2.61, -23.67) * mm});
            skLineSegment(sketch, "E1316", {"start": v(2.61, -23.67) * mm, "end": v(2.62, -23.61) * mm});
            skLineSegment(sketch, "E1317", {"start": v(2.62, -23.61) * mm, "end": v(2.62, -23.57) * mm});
            skLineSegment(sketch, "E1318", {"start": v(2.62, -23.57) * mm, "end": v(2.63, -23.52) * mm});
            skLineSegment(sketch, "E1319", {"start": v(2.63, -23.52) * mm, "end": v(2.63, -23.49) * mm});
            skLineSegment(sketch, "E1320", {"start": v(2.63, -23.49) * mm, "end": v(2.63, -23.46) * mm});
            skLineSegment(sketch, "E1321", {"start": v(2.63, -23.46) * mm, "end": v(2.63, -23.43) * mm});
            skLineSegment(sketch, "E1322", {"start": v(2.63, -23.43) * mm, "end": v(2.63, -23.42) * mm});
            skLineSegment(sketch, "E1323", {"start": v(2.63, -23.42) * mm, "end": v(2.63, -23.4) * mm});
            skLineSegment(sketch, "E1324", {"start": v(2.63, -23.4) * mm, "end": v(2.6, -22.19) * mm});
            skLineSegment(sketch, "E1325", {"start": v(2.6, -22.19) * mm, "end": v(5.44, -21.94) * mm});
            skLineSegment(sketch, "E1326", {"start": v(5.44, -21.94) * mm, "end": v(5.62, -23.15) * mm});
            skLineSegment(sketch, "E1327", {"start": v(5.62, -23.15) * mm, "end": v(5.62, -23.16) * mm});
            skLineSegment(sketch, "E1328", {"start": v(5.62, -23.16) * mm, "end": v(5.62, -23.18) * mm});
            skLineSegment(sketch, "E1329", {"start": v(5.62, -23.18) * mm, "end": v(5.63, -23.2) * mm});
            skLineSegment(sketch, "E1330", {"start": v(5.63, -23.2) * mm, "end": v(5.63, -23.23) * mm});
            skLineSegment(sketch, "E1331", {"start": v(5.63, -23.23) * mm, "end": v(5.64, -23.27) * mm});
            skLineSegment(sketch, "E1332", {"start": v(5.64, -23.27) * mm, "end": v(5.65, -23.3) * mm});
            skLineSegment(sketch, "E1333", {"start": v(5.65, -23.3) * mm, "end": v(5.67, -23.36) * mm});
            skLineSegment(sketch, "E1334", {"start": v(5.67, -23.36) * mm, "end": v(5.68, -23.4) * mm});
            skLineSegment(sketch, "E1335", {"start": v(5.68, -23.4) * mm, "end": v(5.7, -23.47) * mm});
            skLineSegment(sketch, "E1336", {"start": v(5.7, -23.47) * mm, "end": v(5.72, -23.53) * mm});
            skLineSegment(sketch, "E1337", {"start": v(5.72, -23.53) * mm, "end": v(5.75, -23.6) * mm});
            skLineSegment(sketch, "E1338", {"start": v(5.75, -23.6) * mm, "end": v(5.77, -23.68) * mm});
            skLineSegment(sketch, "E1339", {"start": v(5.77, -23.68) * mm, "end": v(5.8, -23.77) * mm});
            skLineSegment(sketch, "E1340", {"start": v(5.8, -23.77) * mm, "end": v(5.84, -23.86) * mm});
            skLineSegment(sketch, "E1341", {"start": v(5.84, -23.86) * mm, "end": v(5.88, -23.95) * mm});
            skLineSegment(sketch, "E1342", {"start": v(5.88, -23.95) * mm, "end": v(5.92, -24.05) * mm});
            skLineSegment(sketch, "E1343", {"start": v(5.92, -24.05) * mm, "end": v(5.97, -24.15) * mm});
            skLineSegment(sketch, "E1344", {"start": v(5.97, -24.15) * mm, "end": v(6.02, -24.26) * mm});
            skLineSegment(sketch, "E1345", {"start": v(6.02, -24.26) * mm, "end": v(6.07, -24.38) * mm});
            skLineSegment(sketch, "E1346", {"start": v(6.07, -24.38) * mm, "end": v(6.13, -24.5) * mm});
            skLineSegment(sketch, "E1347", {"start": v(6.13, -24.5) * mm, "end": v(6.2, -24.62) * mm});
            skLineSegment(sketch, "E1348", {"start": v(6.2, -24.62) * mm, "end": v(6.27, -24.75) * mm});
            skLineSegment(sketch, "E1349", {"start": v(6.27, -24.75) * mm, "end": v(6.35, -24.88) * mm});
            skLineSegment(sketch, "E1350", {"start": v(6.35, -24.88) * mm, "end": v(6.43, -25.02) * mm});
            skLineSegment(sketch, "E1351", {"start": v(6.43, -25.02) * mm, "end": v(6.52, -25.16) * mm});
            skLineSegment(sketch, "E1352", {"start": v(6.52, -25.16) * mm, "end": v(6.6, -25.3) * mm});
            skLineSegment(sketch, "E1353", {"start": v(6.6, -25.3) * mm, "end": v(6.7, -25.46) * mm});
            skLineSegment(sketch, "E1354", {"start": v(6.7, -25.46) * mm, "end": v(6.81, -25.61) * mm});
            skLineSegment(sketch, "E1355", {"start": v(6.81, -25.61) * mm, "end": v(6.92, -25.77) * mm});
            skLineSegment(sketch, "E1356", {"start": v(6.92, -25.77) * mm, "end": v(7.04, -25.93) * mm});
            skLineSegment(sketch, "E1357", {"start": v(7.04, -25.93) * mm, "end": v(7.16, -26.1) * mm});
            skLineSegment(sketch, "E1358", {"start": v(7.16, -26.1) * mm, "end": v(7.3, -26.26) * mm});
            skLineSegment(sketch, "E1359", {"start": v(7.3, -26.26) * mm, "end": v(7.43, -26.43) * mm});
            skLineSegment(sketch, "E1360", {"start": v(7.43, -26.43) * mm, "end": v(7.57, -26.6) * mm});
            skLineSegment(sketch, "E1361", {"start": v(7.57, -26.6) * mm, "end": v(7.72, -26.78) * mm});
            skLineSegment(sketch, "E1362", {"start": v(7.72, -26.78) * mm, "end": v(7.88, -26.96) * mm});
            skLineSegment(sketch, "E1363", {"start": v(7.88, -26.96) * mm, "end": v(8, -26.95) * mm});
            skLineSegment(sketch, "E1364", {"start": v(8, -26.95) * mm, "end": v(9.4, -26.63) * mm});
            skLineSegment(sketch, "E1365", {"start": v(9.4, -26.63) * mm, "end": v(9.53, -26.58) * mm});
            skLineSegment(sketch, "E1366", {"start": v(9.53, -26.58) * mm, "end": v(9.59, -26.35) * mm});
            skLineSegment(sketch, "E1367", {"start": v(9.59, -26.35) * mm, "end": v(9.65, -26.13) * mm});
            skLineSegment(sketch, "E1368", {"start": v(9.65, -26.13) * mm, "end": v(9.7, -25.9) * mm});
            skLineSegment(sketch, "E1369", {"start": v(9.7, -25.9) * mm, "end": v(9.75, -25.7) * mm});
            skLineSegment(sketch, "E1370", {"start": v(9.75, -25.7) * mm, "end": v(9.8, -25.49) * mm});
            skLineSegment(sketch, "E1371", {"start": v(9.8, -25.49) * mm, "end": v(9.83, -25.29) * mm});
            skLineSegment(sketch, "E1372", {"start": v(9.83, -25.29) * mm, "end": v(9.86, -25.09) * mm});
            skLineSegment(sketch, "E1373", {"start": v(9.86, -25.09) * mm, "end": v(9.9, -24.9) * mm});
            skLineSegment(sketch, "E1374", {"start": v(9.9, -24.9) * mm, "end": v(9.92, -24.71) * mm});
            skLineSegment(sketch, "E1375", {"start": v(9.92, -24.71) * mm, "end": v(9.94, -24.54) * mm});
            skLineSegment(sketch, "E1376", {"start": v(9.94, -24.54) * mm, "end": v(9.96, -24.36) * mm});
            skLineSegment(sketch, "E1377", {"start": v(9.96, -24.36) * mm, "end": v(9.98, -24.2) * mm});
            skLineSegment(sketch, "E1378", {"start": v(9.98, -24.2) * mm, "end": v(10, -24.04) * mm});
            skLineSegment(sketch, "E1379", {"start": v(10, -24.04) * mm, "end": v(10, -23.89) * mm});
            skLineSegment(sketch, "E1380", {"start": v(10, -23.89) * mm, "end": v(10, -23.74) * mm});
            skLineSegment(sketch, "E1381", {"start": v(10, -23.74) * mm, "end": v(10.01, -23.6) * mm});
            skLineSegment(sketch, "E1382", {"start": v(10.01, -23.6) * mm, "end": v(10.01, -23.46) * mm});
            skLineSegment(sketch, "E1383", {"start": v(10.01, -23.46) * mm, "end": v(10.01, -23.34) * mm});
            skLineSegment(sketch, "E1384", {"start": v(10.01, -23.34) * mm, "end": v(10.01, -23.22) * mm});
            skLineSegment(sketch, "E1385", {"start": v(10.01, -23.22) * mm, "end": v(10, -23.1) * mm});
            skLineSegment(sketch, "E1386", {"start": v(10, -23.1) * mm, "end": v(10, -23) * mm});
            skLineSegment(sketch, "E1387", {"start": v(10, -23) * mm, "end": v(10, -22.9) * mm});
            skLineSegment(sketch, "E1388", {"start": v(10, -22.9) * mm, "end": v(9.99, -22.8) * mm});
            skLineSegment(sketch, "E1389", {"start": v(9.99, -22.8) * mm, "end": v(9.98, -22.7) * mm});
            skLineSegment(sketch, "E1390", {"start": v(9.98, -22.7) * mm, "end": v(9.97, -22.63) * mm});
            skLineSegment(sketch, "E1391", {"start": v(9.97, -22.63) * mm, "end": v(9.96, -22.55) * mm});
            skLineSegment(sketch, "E1392", {"start": v(9.96, -22.55) * mm, "end": v(9.95, -22.49) * mm});
            skLineSegment(sketch, "E1393", {"start": v(9.95, -22.49) * mm, "end": v(9.94, -22.42) * mm});
            skLineSegment(sketch, "E1394", {"start": v(9.94, -22.42) * mm, "end": v(9.93, -22.37) * mm});
            skLineSegment(sketch, "E1395", {"start": v(9.93, -22.37) * mm, "end": v(9.92, -22.32) * mm});
            skLineSegment(sketch, "E1396", {"start": v(9.92, -22.32) * mm, "end": v(9.91, -22.28) * mm});
            skLineSegment(sketch, "E1397", {"start": v(9.91, -22.28) * mm, "end": v(9.9, -22.24) * mm});
            skLineSegment(sketch, "E1398", {"start": v(9.9, -22.24) * mm, "end": v(9.9, -22.21) * mm});
            skLineSegment(sketch, "E1399", {"start": v(9.9, -22.21) * mm, "end": v(9.9, -22.2) * mm});
            skLineSegment(sketch, "E1400", {"start": v(9.9, -22.2) * mm, "end": v(9.89, -22.17) * mm});
            skLineSegment(sketch, "E1401", {"start": v(9.89, -22.17) * mm, "end": v(9.88, -22.16) * mm});
            skLineSegment(sketch, "E1402", {"start": v(9.88, -22.16) * mm, "end": v(9.5, -21) * mm});
            skLineSegment(sketch, "E1403", {"start": v(9.5, -21) * mm, "end": v(12.17, -19.97) * mm});
            skLineSegment(sketch, "E1404", {"start": v(12.17, -19.97) * mm, "end": v(12.68, -21.08) * mm});
            skLineSegment(sketch, "E1405", {"start": v(12.68, -21.08) * mm, "end": v(12.68, -21.09) * mm});
            skLineSegment(sketch, "E1406", {"start": v(12.68, -21.09) * mm, "end": v(12.69, -21.1) * mm});
            skLineSegment(sketch, "E1407", {"start": v(12.69, -21.1) * mm, "end": v(12.7, -21.12) * mm});
            skLineSegment(sketch, "E1408", {"start": v(12.7, -21.12) * mm, "end": v(12.71, -21.15) * mm});
            skLineSegment(sketch, "E1409", {"start": v(12.71, -21.15) * mm, "end": v(12.73, -21.18) * mm});
            skLineSegment(sketch, "E1410", {"start": v(12.73, -21.18) * mm, "end": v(12.75, -21.22) * mm});
            skLineSegment(sketch, "E1411", {"start": v(12.75, -21.22) * mm, "end": v(12.78, -21.26) * mm});
            skLineSegment(sketch, "E1412", {"start": v(12.78, -21.26) * mm, "end": v(12.81, -21.3) * mm});
            skLineSegment(sketch, "E1413", {"start": v(12.81, -21.3) * mm, "end": v(12.84, -21.36) * mm});
            skLineSegment(sketch, "E1414", {"start": v(12.84, -21.36) * mm, "end": v(12.88, -21.42) * mm});
            skLineSegment(sketch, "E1415", {"start": v(12.88, -21.42) * mm, "end": v(12.93, -21.48) * mm});
            skLineSegment(sketch, "E1416", {"start": v(12.93, -21.48) * mm, "end": v(12.97, -21.55) * mm});
            skLineSegment(sketch, "E1417", {"start": v(12.97, -21.55) * mm, "end": v(13.03, -21.62) * mm});
            skLineSegment(sketch, "E1418", {"start": v(13.03, -21.62) * mm, "end": v(13.09, -21.7) * mm});
            skLineSegment(sketch, "E1419", {"start": v(13.09, -21.7) * mm, "end": v(13.15, -21.77) * mm});
            skLineSegment(sketch, "E1420", {"start": v(13.15, -21.77) * mm, "end": v(13.22, -21.85) * mm});
            skLineSegment(sketch, "E1421", {"start": v(13.22, -21.85) * mm, "end": v(13.3, -21.94) * mm});
            skLineSegment(sketch, "E1422", {"start": v(13.3, -21.94) * mm, "end": v(13.37, -22.03) * mm});
            skLineSegment(sketch, "E1423", {"start": v(13.37, -22.03) * mm, "end": v(13.46, -22.13) * mm});
            skLineSegment(sketch, "E1424", {"start": v(13.46, -22.13) * mm, "end": v(13.55, -22.22) * mm});
            skLineSegment(sketch, "E1425", {"start": v(13.55, -22.22) * mm, "end": v(13.65, -22.32) * mm});
            skLineSegment(sketch, "E1426", {"start": v(13.65, -22.32) * mm, "end": v(13.75, -22.43) * mm});
            skLineSegment(sketch, "E1427", {"start": v(13.75, -22.43) * mm, "end": v(13.86, -22.54) * mm});
            skLineSegment(sketch, "E1428", {"start": v(13.86, -22.54) * mm, "end": v(13.98, -22.64) * mm});
            skLineSegment(sketch, "E1429", {"start": v(13.98, -22.64) * mm, "end": v(14.1, -22.76) * mm});
            skLineSegment(sketch, "E1430", {"start": v(14.1, -22.76) * mm, "end": v(14.23, -22.87) * mm});
            skLineSegment(sketch, "E1431", {"start": v(14.23, -22.87) * mm, "end": v(14.37, -22.99) * mm});
            skLineSegment(sketch, "E1432", {"start": v(14.37, -22.99) * mm, "end": v(14.51, -23.1) * mm});
            skLineSegment(sketch, "E1433", {"start": v(14.51, -23.1) * mm, "end": v(14.66, -23.22) * mm});
            skLineSegment(sketch, "E1434", {"start": v(14.66, -23.22) * mm, "end": v(14.82, -23.35) * mm});
            skLineSegment(sketch, "E1435", {"start": v(14.82, -23.35) * mm, "end": v(14.99, -23.47) * mm});
            skLineSegment(sketch, "E1436", {"start": v(14.99, -23.47) * mm, "end": v(15.16, -23.6) * mm});
            skLineSegment(sketch, "E1437", {"start": v(15.16, -23.6) * mm, "end": v(15.34, -23.72) * mm});
            skLineSegment(sketch, "E1438", {"start": v(15.34, -23.72) * mm, "end": v(15.52, -23.84) * mm});
            skLineSegment(sketch, "E1439", {"start": v(15.52, -23.84) * mm, "end": v(15.72, -23.97) * mm});
            skLineSegment(sketch, "E1440", {"start": v(15.72, -23.97) * mm, "end": v(15.92, -24.1) * mm});
            skLineSegment(sketch, "E1441", {"start": v(15.92, -24.1) * mm, "end": v(16.04, -24.05) * mm});
            skLineSegment(sketch, "E1442", {"start": v(16.04, -24.05) * mm, "end": v(17.3, -23.34) * mm});
            skLineSegment(sketch, "E1443", {"start": v(17.3, -23.34) * mm, "end": v(17.4, -23.27) * mm});
            skLineSegment(sketch, "E1444", {"start": v(17.4, -23.27) * mm, "end": v(17.39, -23.03) * mm});
            skLineSegment(sketch, "E1445", {"start": v(17.39, -23.03) * mm, "end": v(17.38, -22.8) * mm});
            skLineSegment(sketch, "E1446", {"start": v(17.38, -22.8) * mm, "end": v(17.37, -22.57) * mm});
            skLineSegment(sketch, "E1447", {"start": v(17.37, -22.57) * mm, "end": v(17.36, -22.36) * mm});
            skLineSegment(sketch, "E1448", {"start": v(17.36, -22.36) * mm, "end": v(17.34, -22.14) * mm});
            skLineSegment(sketch, "E1449", {"start": v(17.34, -22.14) * mm, "end": v(17.32, -21.94) * mm});
            skLineSegment(sketch, "E1450", {"start": v(17.32, -21.94) * mm, "end": v(17.3, -21.74) * mm});
            skLineSegment(sketch, "E1451", {"start": v(17.3, -21.74) * mm, "end": v(17.27, -21.55) * mm});
            skLineSegment(sketch, "E1452", {"start": v(17.27, -21.55) * mm, "end": v(17.25, -21.37) * mm});
            skLineSegment(sketch, "E1453", {"start": v(17.25, -21.37) * mm, "end": v(17.22, -21.19) * mm});
            skLineSegment(sketch, "E1454", {"start": v(17.22, -21.19) * mm, "end": v(17.19, -21.02) * mm});
            skLineSegment(sketch, "E1455", {"start": v(17.19, -21.02) * mm, "end": v(17.15, -20.86) * mm});
            skLineSegment(sketch, "E1456", {"start": v(17.15, -20.86) * mm, "end": v(17.12, -20.7) * mm});
            skLineSegment(sketch, "E1457", {"start": v(17.12, -20.7) * mm, "end": v(17.09, -20.55) * mm});
            skLineSegment(sketch, "E1458", {"start": v(17.09, -20.55) * mm, "end": v(17.05, -20.4) * mm});
            skLineSegment(sketch, "E1459", {"start": v(17.05, -20.4) * mm, "end": v(17.02, -20.27) * mm});
            skLineSegment(sketch, "E1460", {"start": v(17.02, -20.27) * mm, "end": v(16.98, -20.14) * mm});
            skLineSegment(sketch, "E1461", {"start": v(16.98, -20.14) * mm, "end": v(16.95, -20.02) * mm});
            skLineSegment(sketch, "E1462", {"start": v(16.95, -20.02) * mm, "end": v(16.9, -19.9) * mm});
            skLineSegment(sketch, "E1463", {"start": v(16.9, -19.9) * mm, "end": v(16.87, -19.8) * mm});
            skLineSegment(sketch, "E1464", {"start": v(16.87, -19.8) * mm, "end": v(16.84, -19.7) * mm});
            skLineSegment(sketch, "E1465", {"start": v(16.84, -19.7) * mm, "end": v(16.8, -19.6) * mm});
            skLineSegment(sketch, "E1466", {"start": v(16.8, -19.6) * mm, "end": v(16.77, -19.5) * mm});
            skLineSegment(sketch, "E1467", {"start": v(16.77, -19.5) * mm, "end": v(16.74, -19.43) * mm});
            skLineSegment(sketch, "E1468", {"start": v(16.74, -19.43) * mm, "end": v(16.7, -19.35) * mm});
            skLineSegment(sketch, "E1469", {"start": v(16.7, -19.35) * mm, "end": v(16.67, -19.28) * mm});
            skLineSegment(sketch, "E1470", {"start": v(16.67, -19.28) * mm, "end": v(16.64, -19.22) * mm});
            skLineSegment(sketch, "E1471", {"start": v(16.64, -19.22) * mm, "end": v(16.62, -19.16) * mm});
            skLineSegment(sketch, "E1472", {"start": v(16.62, -19.16) * mm, "end": v(16.6, -19.11) * mm});
            skLineSegment(sketch, "E1473", {"start": v(16.6, -19.11) * mm, "end": v(16.57, -19.07) * mm});
            skLineSegment(sketch, "E1474", {"start": v(16.57, -19.07) * mm, "end": v(16.55, -19.03) * mm});
            skLineSegment(sketch, "E1475", {"start": v(16.55, -19.03) * mm, "end": v(16.53, -19) * mm});
            skLineSegment(sketch, "E1476", {"start": v(16.53, -19) * mm, "end": v(16.52, -18.97) * mm});
            skLineSegment(sketch, "E1477", {"start": v(16.52, -18.97) * mm, "end": v(16.5, -18.95) * mm});
            skLineSegment(sketch, "E1478", {"start": v(16.5, -18.95) * mm, "end": v(16.5, -18.94) * mm});
            skLineSegment(sketch, "E1479", {"start": v(16.5, -18.94) * mm, "end": v(16.5, -18.93) * mm});
            skLineSegment(sketch, "E1480", {"start": v(16.5, -18.93) * mm, "end": v(15.8, -17.92) * mm});
            skLineSegment(sketch, "E1481", {"start": v(15.8, -17.92) * mm, "end": v(18.07, -16.18) * mm});
            skLineSegment(sketch, "E1482", {"start": v(18.07, -16.18) * mm, "end": v(18.87, -17.1) * mm});
            skLineSegment(sketch, "E1483", {"start": v(18.87, -17.1) * mm, "end": v(18.87, -17.1) * mm});
            skLineSegment(sketch, "E1484", {"start": v(18.87, -17.1) * mm, "end": v(18.88, -17.12) * mm});
            skLineSegment(sketch, "E1485", {"start": v(18.88, -17.12) * mm, "end": v(18.9, -17.14) * mm});
            skLineSegment(sketch, "E1486", {"start": v(18.9, -17.14) * mm, "end": v(18.92, -17.16) * mm});
            skLineSegment(sketch, "E1487", {"start": v(18.92, -17.16) * mm, "end": v(18.95, -17.19) * mm});
            skLineSegment(sketch, "E1488", {"start": v(18.95, -17.19) * mm, "end": v(18.98, -17.21) * mm});
            skLineSegment(sketch, "E1489", {"start": v(18.98, -17.21) * mm, "end": v(19.02, -17.25) * mm});
            skLineSegment(sketch, "E1490", {"start": v(19.02, -17.25) * mm, "end": v(19.06, -17.28) * mm});
            skLineSegment(sketch, "E1491", {"start": v(19.06, -17.28) * mm, "end": v(19.1, -17.33) * mm});
            skLineSegment(sketch, "E1492", {"start": v(19.1, -17.33) * mm, "end": v(19.16, -17.37) * mm});
            skLineSegment(sketch, "E1493", {"start": v(19.16, -17.37) * mm, "end": v(19.22, -17.42) * mm});
            skLineSegment(sketch, "E1494", {"start": v(19.22, -17.42) * mm, "end": v(19.28, -17.47) * mm});
            skLineSegment(sketch, "E1495", {"start": v(19.28, -17.47) * mm, "end": v(19.35, -17.52) * mm});
            skLineSegment(sketch, "E1496", {"start": v(19.35, -17.52) * mm, "end": v(19.43, -17.57) * mm});
            skLineSegment(sketch, "E1497", {"start": v(19.43, -17.57) * mm, "end": v(19.51, -17.63) * mm});
            skLineSegment(sketch, "E1498", {"start": v(19.51, -17.63) * mm, "end": v(19.6, -17.7) * mm});
            skLineSegment(sketch, "E1499", {"start": v(19.6, -17.7) * mm, "end": v(19.7, -17.76) * mm});
            skLineSegment(sketch, "E1500", {"start": v(19.7, -17.76) * mm, "end": v(19.8, -17.82) * mm});
            skLineSegment(sketch, "E1501", {"start": v(19.8, -17.82) * mm, "end": v(19.91, -17.89) * mm});
            skLineSegment(sketch, "E1502", {"start": v(19.91, -17.89) * mm, "end": v(20.03, -17.95) * mm});
            skLineSegment(sketch, "E1503", {"start": v(20.03, -17.95) * mm, "end": v(20.15, -18.02) * mm});
            skLineSegment(sketch, "E1504", {"start": v(20.15, -18.02) * mm, "end": v(20.28, -18.1) * mm});
            skLineSegment(sketch, "E1505", {"start": v(20.28, -18.1) * mm, "end": v(20.41, -18.16) * mm});
            skLineSegment(sketch, "E1506", {"start": v(20.41, -18.16) * mm, "end": v(20.56, -18.24) * mm});
            skLineSegment(sketch, "E1507", {"start": v(20.56, -18.24) * mm, "end": v(20.7, -18.3) * mm});
            skLineSegment(sketch, "E1508", {"start": v(20.7, -18.3) * mm, "end": v(20.86, -18.38) * mm});
            skLineSegment(sketch, "E1509", {"start": v(20.86, -18.38) * mm, "end": v(21.03, -18.45) * mm});
            skLineSegment(sketch, "E1510", {"start": v(21.03, -18.45) * mm, "end": v(21.2, -18.53) * mm});
            skLineSegment(sketch, "E1511", {"start": v(21.2, -18.53) * mm, "end": v(21.38, -18.6) * mm});
            skLineSegment(sketch, "E1512", {"start": v(21.38, -18.6) * mm, "end": v(21.56, -18.67) * mm});
            skLineSegment(sketch, "E1513", {"start": v(21.56, -18.67) * mm, "end": v(21.76, -18.74) * mm});
            skLineSegment(sketch, "E1514", {"start": v(21.76, -18.74) * mm, "end": v(21.96, -18.82) * mm});
            skLineSegment(sketch, "E1515", {"start": v(21.96, -18.82) * mm, "end": v(22.16, -18.88) * mm});
            skLineSegment(sketch, "E1516", {"start": v(22.16, -18.88) * mm, "end": v(22.38, -18.95) * mm});
            skLineSegment(sketch, "E1517", {"start": v(22.38, -18.95) * mm, "end": v(22.6, -19.02) * mm});
            skLineSegment(sketch, "E1518", {"start": v(22.6, -19.02) * mm, "end": v(22.83, -19.08) * mm});
            skLineSegment(sketch, "E1519", {"start": v(22.83, -19.08) * mm, "end": v(22.93, -19) * mm});
            skLineSegment(sketch, "E1520", {"start": v(22.93, -19) * mm, "end": v(23.93, -17.97) * mm});
            skLineSegment(sketch, "E1521", {"start": v(23.93, -17.97) * mm, "end": v(24, -17.87) * mm});
            skLineSegment(sketch, "E1522", {"start": v(24, -17.87) * mm, "end": v(23.94, -17.65) * mm});
            skLineSegment(sketch, "E1523", {"start": v(23.94, -17.65) * mm, "end": v(23.86, -17.43) * mm});
            skLineSegment(sketch, "E1524", {"start": v(23.86, -17.43) * mm, "end": v(23.79, -17.21) * mm});
            skLineSegment(sketch, "E1525", {"start": v(23.79, -17.21) * mm, "end": v(23.71, -17) * mm});
            skLineSegment(sketch, "E1526", {"start": v(23.71, -17) * mm, "end": v(23.64, -16.81) * mm});
            skLineSegment(sketch, "E1527", {"start": v(23.64, -16.81) * mm, "end": v(23.56, -16.62) * mm});
            skLineSegment(sketch, "E1528", {"start": v(23.56, -16.62) * mm, "end": v(23.48, -16.44) * mm});
            skLineSegment(sketch, "E1529", {"start": v(23.48, -16.44) * mm, "end": v(23.4, -16.26) * mm});
            skLineSegment(sketch, "E1530", {"start": v(23.4, -16.26) * mm, "end": v(23.33, -16.1) * mm});
            skLineSegment(sketch, "E1531", {"start": v(23.33, -16.1) * mm, "end": v(23.25, -15.93) * mm});
            skLineSegment(sketch, "E1532", {"start": v(23.25, -15.93) * mm, "end": v(23.18, -15.77) * mm});
            skLineSegment(sketch, "E1533", {"start": v(23.18, -15.77) * mm, "end": v(23.1, -15.63) * mm});
            skLineSegment(sketch, "E1534", {"start": v(23.1, -15.63) * mm, "end": v(23.02, -15.48) * mm});
            skLineSegment(sketch, "E1535", {"start": v(23.02, -15.48) * mm, "end": v(22.95, -15.35) * mm});
            skLineSegment(sketch, "E1536", {"start": v(22.95, -15.35) * mm, "end": v(22.87, -15.22) * mm});
            skLineSegment(sketch, "E1537", {"start": v(22.87, -15.22) * mm, "end": v(22.8, -15.1) * mm});
            skLineSegment(sketch, "E1538", {"start": v(22.8, -15.1) * mm, "end": v(22.73, -14.99) * mm});
            skLineSegment(sketch, "E1539", {"start": v(22.73, -14.99) * mm, "end": v(22.66, -14.88) * mm});
            skLineSegment(sketch, "E1540", {"start": v(22.66, -14.88) * mm, "end": v(22.6, -14.78) * mm});
            skLineSegment(sketch, "E1541", {"start": v(22.6, -14.78) * mm, "end": v(22.53, -14.69) * mm});
            skLineSegment(sketch, "E1542", {"start": v(22.53, -14.69) * mm, "end": v(22.47, -14.6) * mm});
            skLineSegment(sketch, "E1543", {"start": v(22.47, -14.6) * mm, "end": v(22.4, -14.52) * mm});
            skLineSegment(sketch, "E1544", {"start": v(22.4, -14.52) * mm, "end": v(22.35, -14.44) * mm});
            skLineSegment(sketch, "E1545", {"start": v(22.35, -14.44) * mm, "end": v(22.3, -14.37) * mm});
            skLineSegment(sketch, "E1546", {"start": v(22.3, -14.37) * mm, "end": v(22.24, -14.3) * mm});
            skLineSegment(sketch, "E1547", {"start": v(22.24, -14.3) * mm, "end": v(22.2, -14.25) * mm});
            skLineSegment(sketch, "E1548", {"start": v(22.2, -14.25) * mm, "end": v(22.15, -14.2) * mm});
            skLineSegment(sketch, "E1549", {"start": v(22.15, -14.2) * mm, "end": v(22.1, -14.15) * mm});
            skLineSegment(sketch, "E1550", {"start": v(22.1, -14.15) * mm, "end": v(22.07, -14.11) * mm});
            skLineSegment(sketch, "E1551", {"start": v(22.07, -14.11) * mm, "end": v(22.03, -14.08) * mm});
            skLineSegment(sketch, "E1552", {"start": v(22.03, -14.08) * mm, "end": v(22, -14.05) * mm});
            skLineSegment(sketch, "E1553", {"start": v(22, -14.05) * mm, "end": v(21.98, -14.02) * mm});
            skLineSegment(sketch, "E1554", {"start": v(21.98, -14.02) * mm, "end": v(21.96, -14) * mm});
            skLineSegment(sketch, "E1555", {"start": v(21.96, -14) * mm, "end": v(21.94, -13.98) * mm});
            skLineSegment(sketch, "E1556", {"start": v(21.94, -13.98) * mm, "end": v(21.93, -13.97) * mm});
            skLineSegment(sketch, "E1557", {"start": v(21.93, -13.97) * mm, "end": v(21.92, -13.97) * mm});
            skLineSegment(sketch, "E1558", {"start": v(21.92, -13.97) * mm, "end": v(20.98, -13.2) * mm});
            skLineSegment(sketch, "E1559", {"start": v(20.98, -13.2) * mm, "end": v(22.66, -10.88) * mm});
            skLineSegment(sketch, "E1560", {"start": v(22.66, -10.88) * mm, "end": v(23.68, -11.54) * mm});
            skLineSegment(sketch, "E1561", {"start": v(23.68, -11.54) * mm, "end": v(23.7, -11.55) * mm});
            skLineSegment(sketch, "E1562", {"start": v(23.7, -11.55) * mm, "end": v(23.7, -11.56) * mm});
            skLineSegment(sketch, "E1563", {"start": v(23.7, -11.56) * mm, "end": v(23.73, -11.57) * mm});
            skLineSegment(sketch, "E1564", {"start": v(23.73, -11.57) * mm, "end": v(23.75, -11.58) * mm});
            skLineSegment(sketch, "E1565", {"start": v(23.75, -11.58) * mm, "end": v(23.79, -11.6) * mm});
            skLineSegment(sketch, "E1566", {"start": v(23.79, -11.6) * mm, "end": v(23.82, -11.62) * mm});
            skLineSegment(sketch, "E1567", {"start": v(23.82, -11.62) * mm, "end": v(23.87, -11.64) * mm});
            skLineSegment(sketch, "E1568", {"start": v(23.87, -11.64) * mm, "end": v(23.92, -11.66) * mm});
            skLineSegment(sketch, "E1569", {"start": v(23.92, -11.66) * mm, "end": v(23.98, -11.69) * mm});
            skLineSegment(sketch, "E1570", {"start": v(23.98, -11.69) * mm, "end": v(24.04, -11.72) * mm});
            skLineSegment(sketch, "E1571", {"start": v(24.04, -11.72) * mm, "end": v(24.1, -11.74) * mm});
            skLineSegment(sketch, "E1572", {"start": v(24.1, -11.74) * mm, "end": v(24.19, -11.77) * mm});
            skLineSegment(sketch, "E1573", {"start": v(24.19, -11.77) * mm, "end": v(24.27, -11.8) * mm});
            skLineSegment(sketch, "E1574", {"start": v(24.27, -11.8) * mm, "end": v(24.36, -11.84) * mm});
            skLineSegment(sketch, "E1575", {"start": v(24.36, -11.84) * mm, "end": v(24.45, -11.87) * mm});
            skLineSegment(sketch, "E1576", {"start": v(24.45, -11.87) * mm, "end": v(24.56, -11.9) * mm});
            skLineSegment(sketch, "E1577", {"start": v(24.56, -11.9) * mm, "end": v(24.67, -11.93) * mm});
            skLineSegment(sketch, "E1578", {"start": v(24.67, -11.93) * mm, "end": v(24.78, -11.97) * mm});
            skLineSegment(sketch, "E1579", {"start": v(24.78, -11.97) * mm, "end": v(24.9, -12) * mm});
            skLineSegment(sketch, "E1580", {"start": v(24.9, -12) * mm, "end": v(25.04, -12.03) * mm});
            skLineSegment(sketch, "E1581", {"start": v(25.04, -12.03) * mm, "end": v(25.17, -12.06) * mm});
            skLineSegment(sketch, "E1582", {"start": v(25.17, -12.06) * mm, "end": v(25.32, -12.1) * mm});
            skLineSegment(sketch, "E1583", {"start": v(25.32, -12.1) * mm, "end": v(25.47, -12.13) * mm});
            skLineSegment(sketch, "E1584", {"start": v(25.47, -12.13) * mm, "end": v(25.63, -12.15) * mm});
            skLineSegment(sketch, "E1585", {"start": v(25.63, -12.15) * mm, "end": v(25.79, -12.18) * mm});
            skLineSegment(sketch, "E1586", {"start": v(25.79, -12.18) * mm, "end": v(25.96, -12.2) * mm});
            skLineSegment(sketch, "E1587", {"start": v(25.96, -12.2) * mm, "end": v(26.14, -12.23) * mm});
            skLineSegment(sketch, "E1588", {"start": v(26.14, -12.23) * mm, "end": v(26.32, -12.25) * mm});
            skLineSegment(sketch, "E1589", {"start": v(26.32, -12.25) * mm, "end": v(26.52, -12.27) * mm});
            skLineSegment(sketch, "E1590", {"start": v(26.52, -12.27) * mm, "end": v(26.71, -12.29) * mm});
            skLineSegment(sketch, "E1591", {"start": v(26.71, -12.29) * mm, "end": v(26.92, -12.3) * mm});
            skLineSegment(sketch, "E1592", {"start": v(26.92, -12.3) * mm, "end": v(27.13, -12.32) * mm});
            skLineSegment(sketch, "E1593", {"start": v(27.13, -12.32) * mm, "end": v(27.35, -12.32) * mm});
            skLineSegment(sketch, "E1594", {"start": v(27.35, -12.32) * mm, "end": v(27.57, -12.33) * mm});
            skLineSegment(sketch, "E1595", {"start": v(27.57, -12.33) * mm, "end": v(27.8, -12.33) * mm});
            skLineSegment(sketch, "E1596", {"start": v(27.8, -12.33) * mm, "end": v(28.04, -12.33) * mm});
            skLineSegment(sketch, "E1597", {"start": v(28.04, -12.33) * mm, "end": v(28.12, -12.23) * mm});
            skLineSegment(sketch, "E1598", {"start": v(28.12, -12.23) * mm, "end": v(28.79, -10.95) * mm});
            skLineSegment(sketch, "E1599", {"start": v(28.79, -10.95) * mm, "end": v(28.83, -10.83) * mm});
            skLineSegment(sketch, "E1600", {"start": v(28.83, -10.83) * mm, "end": v(28.7, -10.64) * mm});
            skLineSegment(sketch, "E1601", {"start": v(28.7, -10.64) * mm, "end": v(28.57, -10.45) * mm});
            skLineSegment(sketch, "E1602", {"start": v(28.57, -10.45) * mm, "end": v(28.44, -10.26) * mm});
            skLineSegment(sketch, "E1603", {"start": v(28.44, -10.26) * mm, "end": v(28.3, -10.09) * mm});
            skLineSegment(sketch, "E1604", {"start": v(28.3, -10.09) * mm, "end": v(28.18, -9.92) * mm});
            skLineSegment(sketch, "E1605", {"start": v(28.18, -9.92) * mm, "end": v(28.05, -9.76) * mm});
            skLineSegment(sketch, "E1606", {"start": v(28.05, -9.76) * mm, "end": v(27.93, -9.6) * mm});
            skLineSegment(sketch, "E1607", {"start": v(27.93, -9.6) * mm, "end": v(27.8, -9.45) * mm});
            skLineSegment(sketch, "E1608", {"start": v(27.8, -9.45) * mm, "end": v(27.68, -9.31) * mm});
            skLineSegment(sketch, "E1609", {"start": v(27.68, -9.31) * mm, "end": v(27.56, -9.18) * mm});
            skLineSegment(sketch, "E1610", {"start": v(27.56, -9.18) * mm, "end": v(27.44, -9.05) * mm});
            skLineSegment(sketch, "E1611", {"start": v(27.44, -9.05) * mm, "end": v(27.33, -8.93) * mm});
            skLineSegment(sketch, "E1612", {"start": v(27.33, -8.93) * mm, "end": v(27.22, -8.82) * mm});
            skLineSegment(sketch, "E1613", {"start": v(27.22, -8.82) * mm, "end": v(27.1, -8.71) * mm});
            skLineSegment(sketch, "E1614", {"start": v(27.1, -8.71) * mm, "end": v(27, -8.61) * mm});
            skLineSegment(sketch, "E1615", {"start": v(27, -8.61) * mm, "end": v(26.9, -8.52) * mm});
            skLineSegment(sketch, "E1616", {"start": v(26.9, -8.52) * mm, "end": v(26.8, -8.43) * mm});
            skLineSegment(sketch, "E1617", {"start": v(26.8, -8.43) * mm, "end": v(26.7, -8.34) * mm});
            skLineSegment(sketch, "E1618", {"start": v(26.7, -8.34) * mm, "end": v(26.6, -8.27) * mm});
            skLineSegment(sketch, "E1619", {"start": v(26.6, -8.27) * mm, "end": v(26.52, -8.2) * mm});
            skLineSegment(sketch, "E1620", {"start": v(26.52, -8.2) * mm, "end": v(26.43, -8.13) * mm});
            skLineSegment(sketch, "E1621", {"start": v(26.43, -8.13) * mm, "end": v(26.35, -8.07) * mm});
            skLineSegment(sketch, "E1622", {"start": v(26.35, -8.07) * mm, "end": v(26.28, -8) * mm});
            skLineSegment(sketch, "E1623", {"start": v(26.28, -8) * mm, "end": v(26.2, -7.96) * mm});
            skLineSegment(sketch, "E1624", {"start": v(26.2, -7.96) * mm, "end": v(26.14, -7.91) * mm});
            skLineSegment(sketch, "E1625", {"start": v(26.14, -7.91) * mm, "end": v(26.07, -7.87) * mm});
            skLineSegment(sketch, "E1626", {"start": v(26.07, -7.87) * mm, "end": v(26.02, -7.83) * mm});
            skLineSegment(sketch, "E1627", {"start": v(26.02, -7.83) * mm, "end": v(25.96, -7.8) * mm});
            skLineSegment(sketch, "E1628", {"start": v(25.96, -7.8) * mm, "end": v(25.91, -7.77) * mm});
            skLineSegment(sketch, "E1629", {"start": v(25.91, -7.77) * mm, "end": v(25.87, -7.75) * mm});
            skLineSegment(sketch, "E1630", {"start": v(25.87, -7.75) * mm, "end": v(25.83, -7.73) * mm});
            skLineSegment(sketch, "E1631", {"start": v(25.83, -7.73) * mm, "end": v(25.8, -7.7) * mm});
            skLineSegment(sketch, "E1632", {"start": v(25.8, -7.7) * mm, "end": v(25.78, -7.7) * mm});
            skLineSegment(sketch, "E1633", {"start": v(25.78, -7.7) * mm, "end": v(25.75, -7.68) * mm});
            skLineSegment(sketch, "E1634", {"start": v(25.75, -7.68) * mm, "end": v(25.74, -7.68) * mm});
            skLineSegment(sketch, "E1635", {"start": v(25.74, -7.68) * mm, "end": v(25.73, -7.67) * mm});
            skLineSegment(sketch, "E1636", {"start": v(25.73, -7.67) * mm, "end": v(24.6, -7.2) * mm});
            skLineSegment(sketch, "E1637", {"start": v(24.6, -7.2) * mm, "end": v(25.57, -4.5) * mm});
            skLineSegment(sketch, "E1638", {"start": v(25.57, -4.5) * mm, "end": v(26.74, -4.85) * mm});
            skLineSegment(sketch, "E1639", {"start": v(26.74, -4.85) * mm, "end": v(26.75, -4.85) * mm});
            skLineSegment(sketch, "E1640", {"start": v(26.75, -4.85) * mm, "end": v(26.77, -4.86) * mm});
            skLineSegment(sketch, "E1641", {"start": v(26.77, -4.86) * mm, "end": v(26.79, -4.86) * mm});
            skLineSegment(sketch, "E1642", {"start": v(26.79, -4.86) * mm, "end": v(26.82, -4.87) * mm});
            skLineSegment(sketch, "E1643", {"start": v(26.82, -4.87) * mm, "end": v(26.85, -4.88) * mm});
            skLineSegment(sketch, "E1644", {"start": v(26.85, -4.88) * mm, "end": v(26.9, -4.88) * mm});
            skLineSegment(sketch, "E1645", {"start": v(26.9, -4.88) * mm, "end": v(26.94, -4.9) * mm});
            skLineSegment(sketch, "E1646", {"start": v(26.94, -4.9) * mm, "end": v(27, -4.9) * mm});
            skLineSegment(sketch, "E1647", {"start": v(27, -4.9) * mm, "end": v(27.06, -4.9) * mm});
            skLineSegment(sketch, "E1648", {"start": v(27.06, -4.9) * mm, "end": v(27.13, -4.92) * mm});
            skLineSegment(sketch, "E1649", {"start": v(27.13, -4.92) * mm, "end": v(27.2, -4.92) * mm});
            skLineSegment(sketch, "E1650", {"start": v(27.2, -4.92) * mm, "end": v(27.29, -4.93) * mm});
            skLineSegment(sketch, "E1651", {"start": v(27.29, -4.93) * mm, "end": v(27.37, -4.94) * mm});
            skLineSegment(sketch, "E1652", {"start": v(27.37, -4.94) * mm, "end": v(27.47, -4.94) * mm});
            skLineSegment(sketch, "E1653", {"start": v(27.47, -4.94) * mm, "end": v(27.57, -4.95) * mm});
            skLineSegment(sketch, "E1654", {"start": v(27.57, -4.95) * mm, "end": v(27.68, -4.95) * mm});
            skLineSegment(sketch, "E1655", {"start": v(27.68, -4.95) * mm, "end": v(27.8, -4.95) * mm});
            skLineSegment(sketch, "E1656", {"start": v(27.8, -4.95) * mm, "end": v(27.91, -4.95) * mm});
            skLineSegment(sketch, "E1657", {"start": v(27.91, -4.95) * mm, "end": v(28.04, -4.95) * mm});
            skLineSegment(sketch, "E1658", {"start": v(28.04, -4.95) * mm, "end": v(28.18, -4.94) * mm});
            skLineSegment(sketch, "E1659", {"start": v(28.18, -4.94) * mm, "end": v(28.32, -4.93) * mm});
            skLineSegment(sketch, "E1660", {"start": v(28.32, -4.93) * mm, "end": v(28.46, -4.92) * mm});
            skLineSegment(sketch, "E1661", {"start": v(28.46, -4.92) * mm, "end": v(28.62, -4.9) * mm});
            skLineSegment(sketch, "E1662", {"start": v(28.62, -4.9) * mm, "end": v(28.78, -4.9) * mm});
            skLineSegment(sketch, "E1663", {"start": v(28.78, -4.9) * mm, "end": v(28.94, -4.87) * mm});
            skLineSegment(sketch, "E1664", {"start": v(28.94, -4.87) * mm, "end": v(29.11, -4.85) * mm});
            skLineSegment(sketch, "E1665", {"start": v(29.11, -4.85) * mm, "end": v(29.29, -4.82) * mm});
            skLineSegment(sketch, "E1666", {"start": v(29.29, -4.82) * mm, "end": v(29.47, -4.79) * mm});
            skLineSegment(sketch, "E1667", {"start": v(29.47, -4.79) * mm, "end": v(29.66, -4.75) * mm});
            skLineSegment(sketch, "E1668", {"start": v(29.66, -4.75) * mm, "end": v(29.86, -4.71) * mm});
            skLineSegment(sketch, "E1669", {"start": v(29.86, -4.71) * mm, "end": v(30.06, -4.67) * mm});
            skLineSegment(sketch, "E1670", {"start": v(30.06, -4.67) * mm, "end": v(30.26, -4.62) * mm});
            skLineSegment(sketch, "E1671", {"start": v(30.26, -4.62) * mm, "end": v(30.48, -4.57) * mm});
            skLineSegment(sketch, "E1672", {"start": v(30.48, -4.57) * mm, "end": v(30.7, -4.5) * mm});
            skLineSegment(sketch, "E1673", {"start": v(30.7, -4.5) * mm, "end": v(30.92, -4.45) * mm});
            skLineSegment(sketch, "E1674", {"start": v(30.92, -4.45) * mm, "end": v(31.14, -4.38) * mm});
            skLineSegment(sketch, "E1675", {"start": v(31.14, -4.38) * mm, "end": v(31.19, -4.26) * mm});
            skLineSegment(sketch, "E1676", {"start": v(31.19, -4.26) * mm, "end": v(31.47, -2.85) * mm});
            skLineSegment(sketch, "E1677", {"start": v(31.47, -2.85) * mm, "end": v(31.48, -2.72) * mm});
            skLineSegment(sketch, "E1678", {"start": v(31.48, -2.72) * mm, "end": v(31.3, -2.57) * mm});
            skLineSegment(sketch, "E1679", {"start": v(31.3, -2.57) * mm, "end": v(31.12, -2.42) * mm});
            skLineSegment(sketch, "E1680", {"start": v(31.12, -2.42) * mm, "end": v(30.94, -2.28) * mm});
            skLineSegment(sketch, "E1681", {"start": v(30.94, -2.28) * mm, "end": v(30.77, -2.15) * mm});
            skLineSegment(sketch, "E1682", {"start": v(30.77, -2.15) * mm, "end": v(30.6, -2.03) * mm});
            skLineSegment(sketch, "E1683", {"start": v(30.6, -2.03) * mm, "end": v(30.43, -1.9) * mm});
            skLineSegment(sketch, "E1684", {"start": v(30.43, -1.9) * mm, "end": v(30.26, -1.8) * mm});
            skLineSegment(sketch, "E1685", {"start": v(30.26, -1.8) * mm, "end": v(30.1, -1.69) * mm});
            skLineSegment(sketch, "E1686", {"start": v(30.1, -1.69) * mm, "end": v(29.95, -1.59) * mm});
            skLineSegment(sketch, "E1687", {"start": v(29.95, -1.59) * mm, "end": v(29.8, -1.5) * mm});
            skLineSegment(sketch, "E1688", {"start": v(29.8, -1.5) * mm, "end": v(29.65, -1.4) * mm});
            skLineSegment(sketch, "E1689", {"start": v(29.65, -1.4) * mm, "end": v(29.5, -1.32) * mm});
            skLineSegment(sketch, "E1690", {"start": v(29.5, -1.32) * mm, "end": v(29.36, -1.24) * mm});
            skLineSegment(sketch, "E1691", {"start": v(29.36, -1.24) * mm, "end": v(29.23, -1.17) * mm});
            skLineSegment(sketch, "E1692", {"start": v(29.23, -1.17) * mm, "end": v(29.1, -1.1) * mm});
            skLineSegment(sketch, "E1693", {"start": v(29.1, -1.1) * mm, "end": v(28.97, -1.04) * mm});
            skLineSegment(sketch, "E1694", {"start": v(28.97, -1.04) * mm, "end": v(28.85, -0.98) * mm});
            skLineSegment(sketch, "E1695", {"start": v(28.85, -0.98) * mm, "end": v(28.73, -0.93) * mm});
            skLineSegment(sketch, "E1696", {"start": v(28.73, -0.93) * mm, "end": v(28.62, -0.88) * mm});
            skLineSegment(sketch, "E1697", {"start": v(28.62, -0.88) * mm, "end": v(28.52, -0.84) * mm});
            skLineSegment(sketch, "E1698", {"start": v(28.52, -0.84) * mm, "end": v(28.42, -0.8) * mm});
            skLineSegment(sketch, "E1699", {"start": v(28.42, -0.8) * mm, "end": v(28.32, -0.76) * mm});
            skLineSegment(sketch, "E1700", {"start": v(28.32, -0.76) * mm, "end": v(28.23, -0.73) * mm});
            skLineSegment(sketch, "E1701", {"start": v(28.23, -0.73) * mm, "end": v(28.15, -0.7) * mm});
            skLineSegment(sketch, "E1702", {"start": v(28.15, -0.7) * mm, "end": v(28.07, -0.68) * mm});
            skLineSegment(sketch, "E1703", {"start": v(28.07, -0.68) * mm, "end": v(28, -0.65) * mm});
            skLineSegment(sketch, "E1704", {"start": v(28, -0.65) * mm, "end": v(27.93, -0.63) * mm});
            skLineSegment(sketch, "E1705", {"start": v(27.93, -0.63) * mm, "end": v(27.87, -0.62) * mm});
            skLineSegment(sketch, "E1706", {"start": v(27.87, -0.62) * mm, "end": v(27.82, -0.6) * mm});
            skLineSegment(sketch, "E1707", {"start": v(27.82, -0.6) * mm, "end": v(27.77, -0.6) * mm});
            skLineSegment(sketch, "E1708", {"start": v(27.77, -0.6) * mm, "end": v(27.73, -0.58) * mm});
            skLineSegment(sketch, "E1709", {"start": v(27.73, -0.58) * mm, "end": v(27.7, -0.58) * mm});
            skLineSegment(sketch, "E1710", {"start": v(27.7, -0.58) * mm, "end": v(27.66, -0.57) * mm});
            skLineSegment(sketch, "E1711", {"start": v(27.66, -0.57) * mm, "end": v(27.64, -0.57) * mm});
            skLineSegment(sketch, "E1712", {"start": v(27.64, -0.57) * mm, "end": v(27.62, -0.56) * mm});
            skLineSegment(sketch, "E1713", {"start": v(27.62, -0.56) * mm, "end": v(27.61, -0.56) * mm});
            skLineSegment(sketch, "E1714", {"start": v(27.61, -0.56) * mm, "end": v(26.4, -0.42) * mm});
            skLineSegment(sketch, "E1715", {"start": v(26.4, -0.42) * mm, "end": v(26.57, 2.43) * mm});
            skFitSpline(sketch, "E1716", {"points": [v(30.32, 4.76) * mm, v(30.32, 5.3) * mm, v(29.88, 5.74) * mm, v(29.34, 5.74) * mm, v(28.8, 5.74) * mm, v(28.36, 5.3) * mm, v(28.36, 4.76) * mm, v(28.36, 4.22) * mm, v(28.8, 3.78) * mm, v(29.34, 3.78) * mm, v(29.88, 3.78) * mm, v(30.32, 4.22) * mm, v(30.32, 4.76) * mm]});
            skCircle(sketch, "E1717", {"center": v(2.2, 2.25) * mm, "radius": 2.5 * mm});
            skSolve(sketch);
        }
        {
            var Q0;
            Q0=makeQuery(id+"F0.imprint","IMPRINT",FACE,{"disambiguationData":[TD([[makeQuery(id+"F0.imprint","IMPRINT",EDGE,{"derivedFrom":sQuery(id+"F0.wireOp",EDGE,"E0")}),1.0]])]});
            extrude(context, id + "F1", {"entities" : qUnion([Q0]), "depth" : 5 * mm, "offsetDistance" : 25 * mm});
        }
    });
